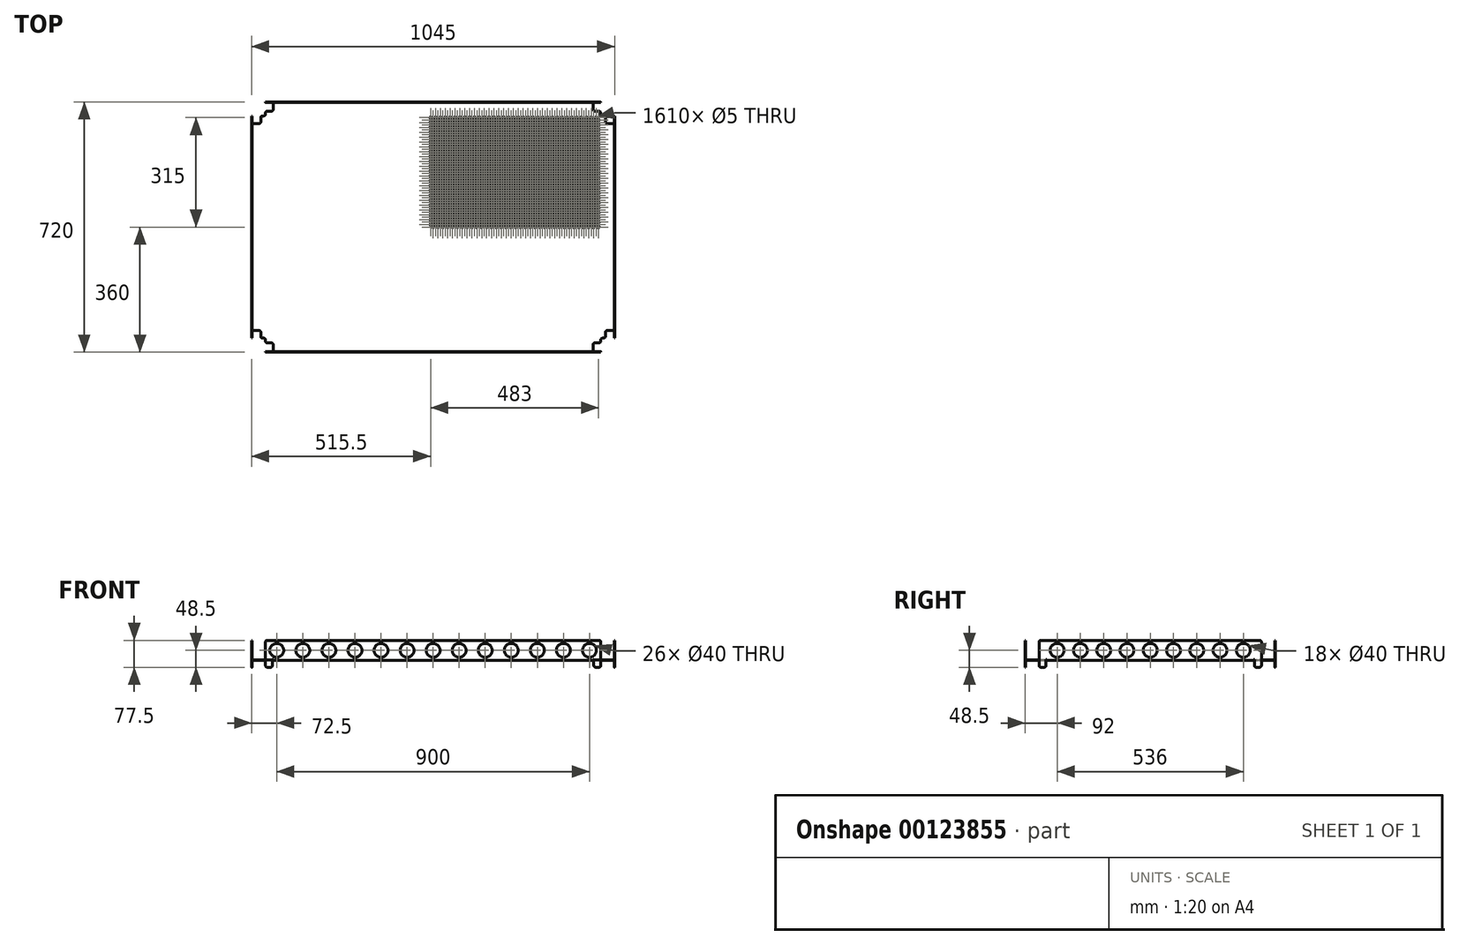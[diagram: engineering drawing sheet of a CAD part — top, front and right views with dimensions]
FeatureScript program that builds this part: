
annotation { "Feature Type Name" : "Feature", "Feature Type Description" : "" }
export const myFeature = defineFeature(function(context is Context, id is Id, definition is map)
    precondition{}
    {
        {
            var Q0;
            Q0=qCreatedBy(makeId("Front.planeOp"),FACE);
            var sketch = newSketch(context, id + "F0", { "sketchPlane" : qUnion([Q0])});
            skLineSegment(sketch, "E0", {"start": v(-520.5, 0) * mm, "end": v(520.5, 0) * mm});
            skLineSegment(sketch, "E1", {"start": v(-522.5, 2) * mm, "end": v(-522.5, 58) * mm});
            skLineSegment(sketch, "E2", {"start": v(0, 0) * mm, "end": v(0, 134.53) * mm, "construction": true});
            skLineSegment(sketch, "E3.MirrorCS", {"start": v(522.5, 2) * mm, "end": v(522.5, 58) * mm});
            skLineSegment(sketch, "E4.0", {"start": v(-521, 2.5) * mm, "end": v(-521, 58) * mm});
            skLineSegment(sketch, "E4.1", {"start": v(-520, 1.5) * mm, "end": v(520, 1.5) * mm});
            skLineSegment(sketch, "E4.2", {"start": v(521, 2.5) * mm, "end": v(521, 58) * mm});
            skLineSegment(sketch, "E5", {"start": v(-522.5, 58) * mm, "end": v(-521, 58) * mm});
            skLineSegment(sketch, "E6", {"start": v(521, 58) * mm, "end": v(522.5, 58) * mm});
            skPoint(sketch, "E7.visualSharp", {"position": v(521, 1.5) * mm});
            skArc(sketch, "E7.filletArc", {"start": v(520, 1.5) * mm, "mid": v(520.7, 1.8) * mm, "end": v(521, 2.5) * mm});
            skPoint(sketch, "E8.visualSharp", {"position": v(522.5, 0) * mm});
            skArc(sketch, "E8.filletArc", {"start": v(520.5, 0) * mm, "mid": v(521.91, 0.59) * mm, "end": v(522.5, 2) * mm});
            skPoint(sketch, "E9.visualSharp", {"position": v(-521, 1.5) * mm});
            skArc(sketch, "E9.filletArc", {"start": v(-521, 2.5) * mm, "mid": v(-520.7, 1.8) * mm, "end": v(-520, 1.5) * mm});
            skPoint(sketch, "E10.visualSharp", {"position": v(-522.5, 0) * mm});
            skArc(sketch, "E10.filletArc", {"start": v(-522.5, 2) * mm, "mid": v(-521.91, 0.59) * mm, "end": v(-520.5, 0) * mm});
            skSolve(sketch);
        }
        {
            var Q0;
            Q0 = qSketchRegion(id + "F0", true);
            extrude(context, id + "F1", {"entities" : qUnion([Q0]), "depth" : 360 * mm, "hasSecondDirection" : true, "secondDirectionOppositeDirection" : true, "secondDirectionDepth" : 360 * mm});
        }
        {
            var Q0;
            Q0=makeQuery(id+"F1.opExtrude","SWEPT_FACE",FACE,{"disambiguationData":[OSD([sQuery(id+"F0.wireOp",EDGE,"E4.2")])]});
            var sketch = newSketch(context, id + "F2", { "sketchPlane" : qUnion([Q0])});
            skLineSegment(sketch, "E11.bottom", {"start": v(-360, 58) * mm, "end": v(-358.5, 58) * mm});
            skLineSegment(sketch, "E11.top", {"start": v(-360, 0) * mm, "end": v(-358.5, 0) * mm});
            skLineSegment(sketch, "E11.left", {"start": v(-360, 58) * mm, "end": v(-360, 0) * mm});
            skLineSegment(sketch, "E11.right", {"start": v(-358.5, 58) * mm, "end": v(-358.5, 0) * mm});
            skLineSegment(sketch, "E12.bottom", {"start": v(360, 58) * mm, "end": v(358.5, 58) * mm});
            skLineSegment(sketch, "E12.top", {"start": v(360, 0) * mm, "end": v(358.5, 0) * mm});
            skLineSegment(sketch, "E12.left", {"start": v(360, 58) * mm, "end": v(360, 0) * mm});
            skLineSegment(sketch, "E12.right", {"start": v(358.5, 58) * mm, "end": v(358.5, 0) * mm});
            skSolve(sketch);
        }
        {
            var Q0;
            Q0 = qSketchRegion(id + "F2", true);
            var Q1;
            Q1=makeQuery(id+"F1.opExtrude","SWEPT_FACE",FACE,{"disambiguationData":[OSD([sQuery(id+"F0.wireOp",EDGE,"E4.0")])]});
            extrude(context, id + "F3", {"entities" : qUnion([Q0]), "operationType" : NewBodyOperationType.ADD, "endBound" : BoundingType.UP_TO_SURFACE, "endBoundEntityFace" : qUnion([Q1]), "depth" : 25 * mm});
        }
        {
            var Q0;
            Q0=makeQuery(id+"F1.opExtrude","CAP_EDGE",EDGE,{"disambiguationData":[OSD([sQuery(id+"F0.wireOp",EDGE,"E0")])],"isStart":true});
            var Q1;
            Q1=makeQuery(id+"F1.opExtrude","CAP_EDGE",EDGE,{"disambiguationData":[OSD([sQuery(id+"F0.wireOp",EDGE,"E0")])],"isStart":false});
            fillet(context, id + "F4", {"entities" : qUnion([Q0, Q1]), "radius" : 2 * mm, "tangentPropagation" : true, "allowEdgeOverflow" : false});
        }
        {
            var Q0;
            Q0=makeQuery(id+"F3.boolean.opBoolean","INTERSECT",EDGE,{"derivedFrom":[makeQuery(id+"F1.opExtrude","SWEPT_FACE",FACE,{"disambiguationData":[OSD([sQuery(id+"F0.wireOp",EDGE,"E4.1")])]}),makeQuery(id+"F3.opExtrude","SWEPT_FACE",FACE,{"disambiguationData":[OSD([sQuery(id+"F2.wireOp",EDGE,"E11.right")])]})]});
            var Q1;
            Q1=makeQuery(id+"F3.boolean.opBoolean","INTERSECT",EDGE,{"derivedFrom":[makeQuery(id+"F1.opExtrude","SWEPT_FACE",FACE,{"disambiguationData":[OSD([sQuery(id+"F0.wireOp",EDGE,"E4.1")])]}),makeQuery(id+"F3.opExtrude","SWEPT_FACE",FACE,{"disambiguationData":[OSD([sQuery(id+"F2.wireOp",EDGE,"E12.right")])]})]});
            fillet(context, id + "F5", {"entities" : qUnion([Q0, Q1]), "radius" : 1 * mm, "tangentPropagation" : true, "allowEdgeOverflow" : false});
        }
        {
            var Q0;
            Q0=makeQuery(id+"F3.boolean.opBoolean","MERGE",FACE,{"derivedFrom":[makeQuery(id+"F1.opExtrude","SWEPT_FACE",FACE,{"disambiguationData":[OSD([sQuery(id+"F0.wireOp",EDGE,"E0")])]}),makeQuery(id+"F3.opExtrude","SWEPT_FACE",FACE,{"disambiguationData":[OSD([sQuery(id+"F2.wireOp",EDGE,"E11.top")])]}),makeQuery(id+"F3.opExtrude","SWEPT_FACE",FACE,{"disambiguationData":[OSD([sQuery(id+"F2.wireOp",EDGE,"E12.top")])]})]});
            var sketch = newSketch(context, id + "F6", { "sketchPlane" : qUnion([Q0])});
            skLineSegment(sketch, "E13.bottom", {"start": v(487.5, -320) * mm, "end": v(522.5, -320) * mm});
            skLineSegment(sketch, "E13.top", {"start": v(482.5, -360) * mm, "end": v(522.5, -360) * mm});
            skLineSegment(sketch, "E13.left", {"start": v(482.5, -325) * mm, "end": v(482.5, -360) * mm});
            skLineSegment(sketch, "E13.right", {"start": v(522.5, -320) * mm, "end": v(522.5, -360) * mm});
            skPoint(sketch, "E14.visualSharp", {"position": v(482.5, -320) * mm});
            skArc(sketch, "E14.filletArc", {"start": v(487.5, -320) * mm, "mid": v(483.96, -321.46) * mm, "end": v(482.5, -325) * mm});
            skLineSegment(sketch, "E15", {"start": v(0, 0) * mm, "end": v(0, -371.02) * mm, "construction": true});
            skLineSegment(sketch, "E16", {"start": v(0, 0) * mm, "end": v(599.15, 0) * mm, "construction": true});
            skArc(sketch, "E17.MirrorCS", {"start": v(-487.5, -320) * mm, "mid": v(-483.96, -321.46) * mm, "end": v(-482.5, -325) * mm});
            skLineSegment(sketch, "E18.MirrorCS", {"start": v(-487.5, -320) * mm, "end": v(-522.5, -320) * mm});
            skLineSegment(sketch, "E19.MirrorCS", {"start": v(-482.5, -360) * mm, "end": v(-522.5, -360) * mm});
            skLineSegment(sketch, "E20.MirrorCS", {"start": v(-482.5, -325) * mm, "end": v(-482.5, -360) * mm});
            skLineSegment(sketch, "E21.MirrorCS", {"start": v(-522.5, -320) * mm, "end": v(-522.5, -360) * mm});
            skPoint(sketch, "E22.MirrorP", {"position": v(-482.5, -320) * mm});
            skArc(sketch, "E23.MirrorCS", {"start": v(-487.5, 320) * mm, "mid": v(-483.96, 321.46) * mm, "end": v(-482.5, 325) * mm});
            skArc(sketch, "E24.MirrorCS", {"start": v(487.5, 320) * mm, "mid": v(483.96, 321.46) * mm, "end": v(482.5, 325) * mm});
            skLineSegment(sketch, "E25.MirrorCS", {"start": v(-522.5, 320) * mm, "end": v(-522.5, 360) * mm});
            skLineSegment(sketch, "E26.MirrorCS", {"start": v(-482.5, 325) * mm, "end": v(-482.5, 360) * mm});
            skLineSegment(sketch, "E27.MirrorCS", {"start": v(-482.5, 360) * mm, "end": v(-522.5, 360) * mm});
            skLineSegment(sketch, "E28.MirrorCS", {"start": v(-487.5, 320) * mm, "end": v(-522.5, 320) * mm});
            skPoint(sketch, "E29.MirrorP", {"position": v(482.5, 320) * mm});
            skPoint(sketch, "E30.MirrorP", {"position": v(-482.5, 320) * mm});
            skLineSegment(sketch, "E31.MirrorCS", {"start": v(0, 0) * mm, "end": v(0, 371.02) * mm, "construction": true});
            skLineSegment(sketch, "E32.MirrorCS", {"start": v(522.5, 320) * mm, "end": v(522.5, 360) * mm});
            skLineSegment(sketch, "E33.MirrorCS", {"start": v(482.5, 325) * mm, "end": v(482.5, 360) * mm});
            skLineSegment(sketch, "E34.MirrorCS", {"start": v(482.5, 360) * mm, "end": v(522.5, 360) * mm});
            skLineSegment(sketch, "E35.MirrorCS", {"start": v(487.5, 320) * mm, "end": v(522.5, 320) * mm});
            skLineSegment(sketch, "E36", {"start": v(15.17, -320) * mm, "end": v(-45.75, -320) * mm, "construction": true});
            skLineSegment(sketch, "E37", {"start": v(482.5, -65.6) * mm, "end": v(482.5, 37.37) * mm, "construction": true});
            skCircle(sketch, "E38", {"center": v(0, 0) * mm, "radius": 2.5 * mm});
            skLineSegment(sketch, "E39.bottom", {"start": v(0, 0) * mm, "end": v(-7, 0) * mm, "construction": true});
            skLineSegment(sketch, "E39.top", {"start": v(0, -7) * mm, "end": v(-7, -7) * mm, "construction": true});
            skLineSegment(sketch, "E39.left", {"start": v(0, 0) * mm, "end": v(0, -7) * mm, "construction": true});
            skLineSegment(sketch, "E39.right", {"start": v(-7, 0) * mm, "end": v(-7, -7) * mm, "construction": true});
            skCircle(sketch, "E40", {"center": v(-7, -7) * mm, "radius": 2.5 * mm});
            skCircle(sketch, "E41.0.1.0", {"center": v(-7, -21) * mm, "radius": 2.5 * mm});
            skCircle(sketch, "E41.0.1.1", {"center": v(0, -14) * mm, "radius": 2.5 * mm});
            skCircle(sketch, "E41.0.2.0", {"center": v(-7, -35) * mm, "radius": 2.5 * mm});
            skCircle(sketch, "E41.0.2.1", {"center": v(0, -28) * mm, "radius": 2.5 * mm});
            skCircle(sketch, "E41.0.3.0", {"center": v(-7, -49) * mm, "radius": 2.5 * mm});
            skCircle(sketch, "E41.0.3.1", {"center": v(0, -42) * mm, "radius": 2.5 * mm});
            skCircle(sketch, "E41.0.4.0", {"center": v(-7, -63) * mm, "radius": 2.5 * mm});
            skCircle(sketch, "E41.0.4.1", {"center": v(0, -56) * mm, "radius": 2.5 * mm});
            skCircle(sketch, "E41.0.5.0", {"center": v(-7, -77) * mm, "radius": 2.5 * mm});
            skCircle(sketch, "E41.0.5.1", {"center": v(0, -70) * mm, "radius": 2.5 * mm});
            skCircle(sketch, "E41.0.6.0", {"center": v(-7, -91) * mm, "radius": 2.5 * mm});
            skCircle(sketch, "E41.0.6.1", {"center": v(0, -84) * mm, "radius": 2.5 * mm});
            skCircle(sketch, "E41.0.7.0", {"center": v(-7, -105) * mm, "radius": 2.5 * mm});
            skCircle(sketch, "E41.0.7.1", {"center": v(0, -98) * mm, "radius": 2.5 * mm});
            skCircle(sketch, "E41.0.8.0", {"center": v(-7, -119) * mm, "radius": 2.5 * mm});
            skCircle(sketch, "E41.0.8.1", {"center": v(0, -112) * mm, "radius": 2.5 * mm});
            skCircle(sketch, "E41.0.9.0", {"center": v(-7, -133) * mm, "radius": 2.5 * mm});
            skCircle(sketch, "E41.0.9.1", {"center": v(0, -126) * mm, "radius": 2.5 * mm});
            skCircle(sketch, "E41.0.10.0", {"center": v(-7, -147) * mm, "radius": 2.5 * mm});
            skCircle(sketch, "E41.0.10.1", {"center": v(0, -140) * mm, "radius": 2.5 * mm});
            skCircle(sketch, "E41.0.11.0", {"center": v(-7, -161) * mm, "radius": 2.5 * mm});
            skCircle(sketch, "E41.0.11.1", {"center": v(0, -154) * mm, "radius": 2.5 * mm});
            skCircle(sketch, "E41.0.12.0", {"center": v(-7, -175) * mm, "radius": 2.5 * mm});
            skCircle(sketch, "E41.0.12.1", {"center": v(0, -168) * mm, "radius": 2.5 * mm});
            skCircle(sketch, "E41.0.13.0", {"center": v(-7, -189) * mm, "radius": 2.5 * mm});
            skCircle(sketch, "E41.0.13.1", {"center": v(0, -182) * mm, "radius": 2.5 * mm});
            skCircle(sketch, "E41.0.14.0", {"center": v(-7, -203) * mm, "radius": 2.5 * mm});
            skCircle(sketch, "E41.0.14.1", {"center": v(0, -196) * mm, "radius": 2.5 * mm});
            skCircle(sketch, "E41.0.15.0", {"center": v(-7, -217) * mm, "radius": 2.5 * mm});
            skCircle(sketch, "E41.0.15.1", {"center": v(0, -210) * mm, "radius": 2.5 * mm});
            skCircle(sketch, "E41.0.16.0", {"center": v(-7, -231) * mm, "radius": 2.5 * mm});
            skCircle(sketch, "E41.0.16.1", {"center": v(0, -224) * mm, "radius": 2.5 * mm});
            skCircle(sketch, "E41.0.17.0", {"center": v(-7, -245) * mm, "radius": 2.5 * mm});
            skCircle(sketch, "E41.0.17.1", {"center": v(0, -238) * mm, "radius": 2.5 * mm});
            skCircle(sketch, "E41.0.18.0", {"center": v(-7, -259) * mm, "radius": 2.5 * mm});
            skCircle(sketch, "E41.0.18.1", {"center": v(0, -252) * mm, "radius": 2.5 * mm});
            skCircle(sketch, "E41.0.19.0", {"center": v(-7, -273) * mm, "radius": 2.5 * mm});
            skCircle(sketch, "E41.0.19.1", {"center": v(0, -266) * mm, "radius": 2.5 * mm});
            skCircle(sketch, "E41.1.0.0", {"center": v(7, -7) * mm, "radius": 2.5 * mm});
            skCircle(sketch, "E41.1.0.1", {"center": v(14, 0) * mm, "radius": 2.5 * mm});
            skCircle(sketch, "E41.1.1.0", {"center": v(7, -21) * mm, "radius": 2.5 * mm});
            skCircle(sketch, "E41.1.1.1", {"center": v(14, -14) * mm, "radius": 2.5 * mm});
            skCircle(sketch, "E41.1.2.0", {"center": v(7, -35) * mm, "radius": 2.5 * mm});
            skCircle(sketch, "E41.1.2.1", {"center": v(14, -28) * mm, "radius": 2.5 * mm});
            skCircle(sketch, "E41.1.3.0", {"center": v(7, -49) * mm, "radius": 2.5 * mm});
            skCircle(sketch, "E41.1.3.1", {"center": v(14, -42) * mm, "radius": 2.5 * mm});
            skCircle(sketch, "E41.1.4.0", {"center": v(7, -63) * mm, "radius": 2.5 * mm});
            skCircle(sketch, "E41.1.4.1", {"center": v(14, -56) * mm, "radius": 2.5 * mm});
            skCircle(sketch, "E41.1.5.0", {"center": v(7, -77) * mm, "radius": 2.5 * mm});
            skCircle(sketch, "E41.1.5.1", {"center": v(14, -70) * mm, "radius": 2.5 * mm});
            skCircle(sketch, "E41.1.6.0", {"center": v(7, -91) * mm, "radius": 2.5 * mm});
            skCircle(sketch, "E41.1.6.1", {"center": v(14, -84) * mm, "radius": 2.5 * mm});
            skCircle(sketch, "E41.1.7.0", {"center": v(7, -105) * mm, "radius": 2.5 * mm});
            skCircle(sketch, "E41.1.7.1", {"center": v(14, -98) * mm, "radius": 2.5 * mm});
            skCircle(sketch, "E41.1.8.0", {"center": v(7, -119) * mm, "radius": 2.5 * mm});
            skCircle(sketch, "E41.1.8.1", {"center": v(14, -112) * mm, "radius": 2.5 * mm});
            skCircle(sketch, "E41.1.9.0", {"center": v(7, -133) * mm, "radius": 2.5 * mm});
            skCircle(sketch, "E41.1.9.1", {"center": v(14, -126) * mm, "radius": 2.5 * mm});
            skCircle(sketch, "E41.1.10.0", {"center": v(7, -147) * mm, "radius": 2.5 * mm});
            skCircle(sketch, "E41.1.10.1", {"center": v(14, -140) * mm, "radius": 2.5 * mm});
            skCircle(sketch, "E41.1.11.0", {"center": v(7, -161) * mm, "radius": 2.5 * mm});
            skCircle(sketch, "E41.1.11.1", {"center": v(14, -154) * mm, "radius": 2.5 * mm});
            skCircle(sketch, "E41.1.12.0", {"center": v(7, -175) * mm, "radius": 2.5 * mm});
            skCircle(sketch, "E41.1.12.1", {"center": v(14, -168) * mm, "radius": 2.5 * mm});
            skCircle(sketch, "E41.1.13.0", {"center": v(7, -189) * mm, "radius": 2.5 * mm});
            skCircle(sketch, "E41.1.13.1", {"center": v(14, -182) * mm, "radius": 2.5 * mm});
            skCircle(sketch, "E41.1.14.0", {"center": v(7, -203) * mm, "radius": 2.5 * mm});
            skCircle(sketch, "E41.1.14.1", {"center": v(14, -196) * mm, "radius": 2.5 * mm});
            skCircle(sketch, "E41.1.15.0", {"center": v(7, -217) * mm, "radius": 2.5 * mm});
            skCircle(sketch, "E41.1.15.1", {"center": v(14, -210) * mm, "radius": 2.5 * mm});
            skCircle(sketch, "E41.1.16.0", {"center": v(7, -231) * mm, "radius": 2.5 * mm});
            skCircle(sketch, "E41.1.16.1", {"center": v(14, -224) * mm, "radius": 2.5 * mm});
            skCircle(sketch, "E41.1.17.0", {"center": v(7, -245) * mm, "radius": 2.5 * mm});
            skCircle(sketch, "E41.1.17.1", {"center": v(14, -238) * mm, "radius": 2.5 * mm});
            skCircle(sketch, "E41.1.18.0", {"center": v(7, -259) * mm, "radius": 2.5 * mm});
            skCircle(sketch, "E41.1.18.1", {"center": v(14, -252) * mm, "radius": 2.5 * mm});
            skCircle(sketch, "E41.1.19.0", {"center": v(7, -273) * mm, "radius": 2.5 * mm});
            skCircle(sketch, "E41.1.19.1", {"center": v(14, -266) * mm, "radius": 2.5 * mm});
            skCircle(sketch, "E41.2.0.0", {"center": v(21, -7) * mm, "radius": 2.5 * mm});
            skCircle(sketch, "E41.2.0.1", {"center": v(28, 0) * mm, "radius": 2.5 * mm});
            skCircle(sketch, "E41.2.1.0", {"center": v(21, -21) * mm, "radius": 2.5 * mm});
            skCircle(sketch, "E41.2.1.1", {"center": v(28, -14) * mm, "radius": 2.5 * mm});
            skCircle(sketch, "E41.2.2.0", {"center": v(21, -35) * mm, "radius": 2.5 * mm});
            skCircle(sketch, "E41.2.2.1", {"center": v(28, -28) * mm, "radius": 2.5 * mm});
            skCircle(sketch, "E41.2.3.0", {"center": v(21, -49) * mm, "radius": 2.5 * mm});
            skCircle(sketch, "E41.2.3.1", {"center": v(28, -42) * mm, "radius": 2.5 * mm});
            skCircle(sketch, "E41.2.4.0", {"center": v(21, -63) * mm, "radius": 2.5 * mm});
            skCircle(sketch, "E41.2.4.1", {"center": v(28, -56) * mm, "radius": 2.5 * mm});
            skCircle(sketch, "E41.2.5.0", {"center": v(21, -77) * mm, "radius": 2.5 * mm});
            skCircle(sketch, "E41.2.5.1", {"center": v(28, -70) * mm, "radius": 2.5 * mm});
            skCircle(sketch, "E41.2.6.0", {"center": v(21, -91) * mm, "radius": 2.5 * mm});
            skCircle(sketch, "E41.2.6.1", {"center": v(28, -84) * mm, "radius": 2.5 * mm});
            skCircle(sketch, "E41.2.7.0", {"center": v(21, -105) * mm, "radius": 2.5 * mm});
            skCircle(sketch, "E41.2.7.1", {"center": v(28, -98) * mm, "radius": 2.5 * mm});
            skCircle(sketch, "E41.2.8.0", {"center": v(21, -119) * mm, "radius": 2.5 * mm});
            skCircle(sketch, "E41.2.8.1", {"center": v(28, -112) * mm, "radius": 2.5 * mm});
            skCircle(sketch, "E41.2.9.0", {"center": v(21, -133) * mm, "radius": 2.5 * mm});
            skCircle(sketch, "E41.2.9.1", {"center": v(28, -126) * mm, "radius": 2.5 * mm});
            skCircle(sketch, "E41.2.10.0", {"center": v(21, -147) * mm, "radius": 2.5 * mm});
            skCircle(sketch, "E41.2.10.1", {"center": v(28, -140) * mm, "radius": 2.5 * mm});
            skCircle(sketch, "E41.2.11.0", {"center": v(21, -161) * mm, "radius": 2.5 * mm});
            skCircle(sketch, "E41.2.11.1", {"center": v(28, -154) * mm, "radius": 2.5 * mm});
            skCircle(sketch, "E41.2.12.0", {"center": v(21, -175) * mm, "radius": 2.5 * mm});
            skCircle(sketch, "E41.2.12.1", {"center": v(28, -168) * mm, "radius": 2.5 * mm});
            skCircle(sketch, "E41.2.13.0", {"center": v(21, -189) * mm, "radius": 2.5 * mm});
            skCircle(sketch, "E41.2.13.1", {"center": v(28, -182) * mm, "radius": 2.5 * mm});
            skCircle(sketch, "E41.2.14.0", {"center": v(21, -203) * mm, "radius": 2.5 * mm});
            skCircle(sketch, "E41.2.14.1", {"center": v(28, -196) * mm, "radius": 2.5 * mm});
            skCircle(sketch, "E41.2.15.0", {"center": v(21, -217) * mm, "radius": 2.5 * mm});
            skCircle(sketch, "E41.2.15.1", {"center": v(28, -210) * mm, "radius": 2.5 * mm});
            skCircle(sketch, "E41.2.16.0", {"center": v(21, -231) * mm, "radius": 2.5 * mm});
            skCircle(sketch, "E41.2.16.1", {"center": v(28, -224) * mm, "radius": 2.5 * mm});
            skCircle(sketch, "E41.2.17.0", {"center": v(21, -245) * mm, "radius": 2.5 * mm});
            skCircle(sketch, "E41.2.17.1", {"center": v(28, -238) * mm, "radius": 2.5 * mm});
            skCircle(sketch, "E41.2.18.0", {"center": v(21, -259) * mm, "radius": 2.5 * mm});
            skCircle(sketch, "E41.2.18.1", {"center": v(28, -252) * mm, "radius": 2.5 * mm});
            skCircle(sketch, "E41.2.19.0", {"center": v(21, -273) * mm, "radius": 2.5 * mm});
            skCircle(sketch, "E41.2.19.1", {"center": v(28, -266) * mm, "radius": 2.5 * mm});
            skCircle(sketch, "E41.3.0.0", {"center": v(35, -7) * mm, "radius": 2.5 * mm});
            skCircle(sketch, "E41.3.0.1", {"center": v(42, 0) * mm, "radius": 2.5 * mm});
            skCircle(sketch, "E41.3.1.0", {"center": v(35, -21) * mm, "radius": 2.5 * mm});
            skCircle(sketch, "E41.3.1.1", {"center": v(42, -14) * mm, "radius": 2.5 * mm});
            skCircle(sketch, "E41.3.2.0", {"center": v(35, -35) * mm, "radius": 2.5 * mm});
            skCircle(sketch, "E41.3.2.1", {"center": v(42, -28) * mm, "radius": 2.5 * mm});
            skCircle(sketch, "E41.3.3.0", {"center": v(35, -49) * mm, "radius": 2.5 * mm});
            skCircle(sketch, "E41.3.3.1", {"center": v(42, -42) * mm, "radius": 2.5 * mm});
            skCircle(sketch, "E41.3.4.0", {"center": v(35, -63) * mm, "radius": 2.5 * mm});
            skCircle(sketch, "E41.3.4.1", {"center": v(42, -56) * mm, "radius": 2.5 * mm});
            skCircle(sketch, "E41.3.5.0", {"center": v(35, -77) * mm, "radius": 2.5 * mm});
            skCircle(sketch, "E41.3.5.1", {"center": v(42, -70) * mm, "radius": 2.5 * mm});
            skCircle(sketch, "E41.3.6.0", {"center": v(35, -91) * mm, "radius": 2.5 * mm});
            skCircle(sketch, "E41.3.6.1", {"center": v(42, -84) * mm, "radius": 2.5 * mm});
            skCircle(sketch, "E41.3.7.0", {"center": v(35, -105) * mm, "radius": 2.5 * mm});
            skCircle(sketch, "E41.3.7.1", {"center": v(42, -98) * mm, "radius": 2.5 * mm});
            skCircle(sketch, "E41.3.8.0", {"center": v(35, -119) * mm, "radius": 2.5 * mm});
            skCircle(sketch, "E41.3.8.1", {"center": v(42, -112) * mm, "radius": 2.5 * mm});
            skCircle(sketch, "E41.3.9.0", {"center": v(35, -133) * mm, "radius": 2.5 * mm});
            skCircle(sketch, "E41.3.9.1", {"center": v(42, -126) * mm, "radius": 2.5 * mm});
            skCircle(sketch, "E41.3.10.0", {"center": v(35, -147) * mm, "radius": 2.5 * mm});
            skCircle(sketch, "E41.3.10.1", {"center": v(42, -140) * mm, "radius": 2.5 * mm});
            skCircle(sketch, "E41.3.11.0", {"center": v(35, -161) * mm, "radius": 2.5 * mm});
            skCircle(sketch, "E41.3.11.1", {"center": v(42, -154) * mm, "radius": 2.5 * mm});
            skCircle(sketch, "E41.3.12.0", {"center": v(35, -175) * mm, "radius": 2.5 * mm});
            skCircle(sketch, "E41.3.12.1", {"center": v(42, -168) * mm, "radius": 2.5 * mm});
            skCircle(sketch, "E41.3.13.0", {"center": v(35, -189) * mm, "radius": 2.5 * mm});
            skCircle(sketch, "E41.3.13.1", {"center": v(42, -182) * mm, "radius": 2.5 * mm});
            skCircle(sketch, "E41.3.14.0", {"center": v(35, -203) * mm, "radius": 2.5 * mm});
            skCircle(sketch, "E41.3.14.1", {"center": v(42, -196) * mm, "radius": 2.5 * mm});
            skCircle(sketch, "E41.3.15.0", {"center": v(35, -217) * mm, "radius": 2.5 * mm});
            skCircle(sketch, "E41.3.15.1", {"center": v(42, -210) * mm, "radius": 2.5 * mm});
            skCircle(sketch, "E41.3.16.0", {"center": v(35, -231) * mm, "radius": 2.5 * mm});
            skCircle(sketch, "E41.3.16.1", {"center": v(42, -224) * mm, "radius": 2.5 * mm});
            skCircle(sketch, "E41.3.17.0", {"center": v(35, -245) * mm, "radius": 2.5 * mm});
            skCircle(sketch, "E41.3.17.1", {"center": v(42, -238) * mm, "radius": 2.5 * mm});
            skCircle(sketch, "E41.3.18.0", {"center": v(35, -259) * mm, "radius": 2.5 * mm});
            skCircle(sketch, "E41.3.18.1", {"center": v(42, -252) * mm, "radius": 2.5 * mm});
            skCircle(sketch, "E41.3.19.0", {"center": v(35, -273) * mm, "radius": 2.5 * mm});
            skCircle(sketch, "E41.3.19.1", {"center": v(42, -266) * mm, "radius": 2.5 * mm});
            skCircle(sketch, "E41.4.0.0", {"center": v(49, -7) * mm, "radius": 2.5 * mm});
            skCircle(sketch, "E41.4.0.1", {"center": v(56, 0) * mm, "radius": 2.5 * mm});
            skCircle(sketch, "E41.4.1.0", {"center": v(49, -21) * mm, "radius": 2.5 * mm});
            skCircle(sketch, "E41.4.1.1", {"center": v(56, -14) * mm, "radius": 2.5 * mm});
            skCircle(sketch, "E41.4.2.0", {"center": v(49, -35) * mm, "radius": 2.5 * mm});
            skCircle(sketch, "E41.4.2.1", {"center": v(56, -28) * mm, "radius": 2.5 * mm});
            skCircle(sketch, "E41.4.3.0", {"center": v(49, -49) * mm, "radius": 2.5 * mm});
            skCircle(sketch, "E41.4.3.1", {"center": v(56, -42) * mm, "radius": 2.5 * mm});
            skCircle(sketch, "E41.4.4.0", {"center": v(49, -63) * mm, "radius": 2.5 * mm});
            skCircle(sketch, "E41.4.4.1", {"center": v(56, -56) * mm, "radius": 2.5 * mm});
            skCircle(sketch, "E41.4.5.0", {"center": v(49, -77) * mm, "radius": 2.5 * mm});
            skCircle(sketch, "E41.4.5.1", {"center": v(56, -70) * mm, "radius": 2.5 * mm});
            skCircle(sketch, "E41.4.6.0", {"center": v(49, -91) * mm, "radius": 2.5 * mm});
            skCircle(sketch, "E41.4.6.1", {"center": v(56, -84) * mm, "radius": 2.5 * mm});
            skCircle(sketch, "E41.4.7.0", {"center": v(49, -105) * mm, "radius": 2.5 * mm});
            skCircle(sketch, "E41.4.7.1", {"center": v(56, -98) * mm, "radius": 2.5 * mm});
            skCircle(sketch, "E41.4.8.0", {"center": v(49, -119) * mm, "radius": 2.5 * mm});
            skCircle(sketch, "E41.4.8.1", {"center": v(56, -112) * mm, "radius": 2.5 * mm});
            skCircle(sketch, "E41.4.9.0", {"center": v(49, -133) * mm, "radius": 2.5 * mm});
            skCircle(sketch, "E41.4.9.1", {"center": v(56, -126) * mm, "radius": 2.5 * mm});
            skCircle(sketch, "E41.4.10.0", {"center": v(49, -147) * mm, "radius": 2.5 * mm});
            skCircle(sketch, "E41.4.10.1", {"center": v(56, -140) * mm, "radius": 2.5 * mm});
            skCircle(sketch, "E41.4.11.0", {"center": v(49, -161) * mm, "radius": 2.5 * mm});
            skCircle(sketch, "E41.4.11.1", {"center": v(56, -154) * mm, "radius": 2.5 * mm});
            skCircle(sketch, "E41.4.12.0", {"center": v(49, -175) * mm, "radius": 2.5 * mm});
            skCircle(sketch, "E41.4.12.1", {"center": v(56, -168) * mm, "radius": 2.5 * mm});
            skCircle(sketch, "E41.4.13.0", {"center": v(49, -189) * mm, "radius": 2.5 * mm});
            skCircle(sketch, "E41.4.13.1", {"center": v(56, -182) * mm, "radius": 2.5 * mm});
            skCircle(sketch, "E41.4.14.0", {"center": v(49, -203) * mm, "radius": 2.5 * mm});
            skCircle(sketch, "E41.4.14.1", {"center": v(56, -196) * mm, "radius": 2.5 * mm});
            skCircle(sketch, "E41.4.15.0", {"center": v(49, -217) * mm, "radius": 2.5 * mm});
            skCircle(sketch, "E41.4.15.1", {"center": v(56, -210) * mm, "radius": 2.5 * mm});
            skCircle(sketch, "E41.4.16.0", {"center": v(49, -231) * mm, "radius": 2.5 * mm});
            skCircle(sketch, "E41.4.16.1", {"center": v(56, -224) * mm, "radius": 2.5 * mm});
            skCircle(sketch, "E41.4.17.0", {"center": v(49, -245) * mm, "radius": 2.5 * mm});
            skCircle(sketch, "E41.4.17.1", {"center": v(56, -238) * mm, "radius": 2.5 * mm});
            skCircle(sketch, "E41.4.18.0", {"center": v(49, -259) * mm, "radius": 2.5 * mm});
            skCircle(sketch, "E41.4.18.1", {"center": v(56, -252) * mm, "radius": 2.5 * mm});
            skCircle(sketch, "E41.4.19.0", {"center": v(49, -273) * mm, "radius": 2.5 * mm});
            skCircle(sketch, "E41.4.19.1", {"center": v(56, -266) * mm, "radius": 2.5 * mm});
            skCircle(sketch, "E41.5.0.0", {"center": v(63, -7) * mm, "radius": 2.5 * mm});
            skCircle(sketch, "E41.5.0.1", {"center": v(70, 0) * mm, "radius": 2.5 * mm});
            skCircle(sketch, "E41.5.1.0", {"center": v(63, -21) * mm, "radius": 2.5 * mm});
            skCircle(sketch, "E41.5.1.1", {"center": v(70, -14) * mm, "radius": 2.5 * mm});
            skCircle(sketch, "E41.5.2.0", {"center": v(63, -35) * mm, "radius": 2.5 * mm});
            skCircle(sketch, "E41.5.2.1", {"center": v(70, -28) * mm, "radius": 2.5 * mm});
            skCircle(sketch, "E41.5.3.0", {"center": v(63, -49) * mm, "radius": 2.5 * mm});
            skCircle(sketch, "E41.5.3.1", {"center": v(70, -42) * mm, "radius": 2.5 * mm});
            skCircle(sketch, "E41.5.4.0", {"center": v(63, -63) * mm, "radius": 2.5 * mm});
            skCircle(sketch, "E41.5.4.1", {"center": v(70, -56) * mm, "radius": 2.5 * mm});
            skCircle(sketch, "E41.5.5.0", {"center": v(63, -77) * mm, "radius": 2.5 * mm});
            skCircle(sketch, "E41.5.5.1", {"center": v(70, -70) * mm, "radius": 2.5 * mm});
            skCircle(sketch, "E41.5.6.0", {"center": v(63, -91) * mm, "radius": 2.5 * mm});
            skCircle(sketch, "E41.5.6.1", {"center": v(70, -84) * mm, "radius": 2.5 * mm});
            skCircle(sketch, "E41.5.7.0", {"center": v(63, -105) * mm, "radius": 2.5 * mm});
            skCircle(sketch, "E41.5.7.1", {"center": v(70, -98) * mm, "radius": 2.5 * mm});
            skCircle(sketch, "E41.5.8.0", {"center": v(63, -119) * mm, "radius": 2.5 * mm});
            skCircle(sketch, "E41.5.8.1", {"center": v(70, -112) * mm, "radius": 2.5 * mm});
            skCircle(sketch, "E41.5.9.0", {"center": v(63, -133) * mm, "radius": 2.5 * mm});
            skCircle(sketch, "E41.5.9.1", {"center": v(70, -126) * mm, "radius": 2.5 * mm});
            skCircle(sketch, "E41.5.10.0", {"center": v(63, -147) * mm, "radius": 2.5 * mm});
            skCircle(sketch, "E41.5.10.1", {"center": v(70, -140) * mm, "radius": 2.5 * mm});
            skCircle(sketch, "E41.5.11.0", {"center": v(63, -161) * mm, "radius": 2.5 * mm});
            skCircle(sketch, "E41.5.11.1", {"center": v(70, -154) * mm, "radius": 2.5 * mm});
            skCircle(sketch, "E41.5.12.0", {"center": v(63, -175) * mm, "radius": 2.5 * mm});
            skCircle(sketch, "E41.5.12.1", {"center": v(70, -168) * mm, "radius": 2.5 * mm});
            skCircle(sketch, "E41.5.13.0", {"center": v(63, -189) * mm, "radius": 2.5 * mm});
            skCircle(sketch, "E41.5.13.1", {"center": v(70, -182) * mm, "radius": 2.5 * mm});
            skCircle(sketch, "E41.5.14.0", {"center": v(63, -203) * mm, "radius": 2.5 * mm});
            skCircle(sketch, "E41.5.14.1", {"center": v(70, -196) * mm, "radius": 2.5 * mm});
            skCircle(sketch, "E41.5.15.0", {"center": v(63, -217) * mm, "radius": 2.5 * mm});
            skCircle(sketch, "E41.5.15.1", {"center": v(70, -210) * mm, "radius": 2.5 * mm});
            skCircle(sketch, "E41.5.16.0", {"center": v(63, -231) * mm, "radius": 2.5 * mm});
            skCircle(sketch, "E41.5.16.1", {"center": v(70, -224) * mm, "radius": 2.5 * mm});
            skCircle(sketch, "E41.5.17.0", {"center": v(63, -245) * mm, "radius": 2.5 * mm});
            skCircle(sketch, "E41.5.17.1", {"center": v(70, -238) * mm, "radius": 2.5 * mm});
            skCircle(sketch, "E41.5.18.0", {"center": v(63, -259) * mm, "radius": 2.5 * mm});
            skCircle(sketch, "E41.5.18.1", {"center": v(70, -252) * mm, "radius": 2.5 * mm});
            skCircle(sketch, "E41.5.19.0", {"center": v(63, -273) * mm, "radius": 2.5 * mm});
            skCircle(sketch, "E41.5.19.1", {"center": v(70, -266) * mm, "radius": 2.5 * mm});
            skCircle(sketch, "E41.6.0.0", {"center": v(77, -7) * mm, "radius": 2.5 * mm});
            skCircle(sketch, "E41.6.0.1", {"center": v(84, 0) * mm, "radius": 2.5 * mm});
            skCircle(sketch, "E41.6.1.0", {"center": v(77, -21) * mm, "radius": 2.5 * mm});
            skCircle(sketch, "E41.6.1.1", {"center": v(84, -14) * mm, "radius": 2.5 * mm});
            skCircle(sketch, "E41.6.2.0", {"center": v(77, -35) * mm, "radius": 2.5 * mm});
            skCircle(sketch, "E41.6.2.1", {"center": v(84, -28) * mm, "radius": 2.5 * mm});
            skCircle(sketch, "E41.6.3.0", {"center": v(77, -49) * mm, "radius": 2.5 * mm});
            skCircle(sketch, "E41.6.3.1", {"center": v(84, -42) * mm, "radius": 2.5 * mm});
            skCircle(sketch, "E41.6.4.0", {"center": v(77, -63) * mm, "radius": 2.5 * mm});
            skCircle(sketch, "E41.6.4.1", {"center": v(84, -56) * mm, "radius": 2.5 * mm});
            skCircle(sketch, "E41.6.5.0", {"center": v(77, -77) * mm, "radius": 2.5 * mm});
            skCircle(sketch, "E41.6.5.1", {"center": v(84, -70) * mm, "radius": 2.5 * mm});
            skCircle(sketch, "E41.6.6.0", {"center": v(77, -91) * mm, "radius": 2.5 * mm});
            skCircle(sketch, "E41.6.6.1", {"center": v(84, -84) * mm, "radius": 2.5 * mm});
            skCircle(sketch, "E41.6.7.0", {"center": v(77, -105) * mm, "radius": 2.5 * mm});
            skCircle(sketch, "E41.6.7.1", {"center": v(84, -98) * mm, "radius": 2.5 * mm});
            skCircle(sketch, "E41.6.8.0", {"center": v(77, -119) * mm, "radius": 2.5 * mm});
            skCircle(sketch, "E41.6.8.1", {"center": v(84, -112) * mm, "radius": 2.5 * mm});
            skCircle(sketch, "E41.6.9.0", {"center": v(77, -133) * mm, "radius": 2.5 * mm});
            skCircle(sketch, "E41.6.9.1", {"center": v(84, -126) * mm, "radius": 2.5 * mm});
            skCircle(sketch, "E41.6.10.0", {"center": v(77, -147) * mm, "radius": 2.5 * mm});
            skCircle(sketch, "E41.6.10.1", {"center": v(84, -140) * mm, "radius": 2.5 * mm});
            skCircle(sketch, "E41.6.11.0", {"center": v(77, -161) * mm, "radius": 2.5 * mm});
            skCircle(sketch, "E41.6.11.1", {"center": v(84, -154) * mm, "radius": 2.5 * mm});
            skCircle(sketch, "E41.6.12.0", {"center": v(77, -175) * mm, "radius": 2.5 * mm});
            skCircle(sketch, "E41.6.12.1", {"center": v(84, -168) * mm, "radius": 2.5 * mm});
            skCircle(sketch, "E41.6.13.0", {"center": v(77, -189) * mm, "radius": 2.5 * mm});
            skCircle(sketch, "E41.6.13.1", {"center": v(84, -182) * mm, "radius": 2.5 * mm});
            skCircle(sketch, "E41.6.14.0", {"center": v(77, -203) * mm, "radius": 2.5 * mm});
            skCircle(sketch, "E41.6.14.1", {"center": v(84, -196) * mm, "radius": 2.5 * mm});
            skCircle(sketch, "E41.6.15.0", {"center": v(77, -217) * mm, "radius": 2.5 * mm});
            skCircle(sketch, "E41.6.15.1", {"center": v(84, -210) * mm, "radius": 2.5 * mm});
            skCircle(sketch, "E41.6.16.0", {"center": v(77, -231) * mm, "radius": 2.5 * mm});
            skCircle(sketch, "E41.6.16.1", {"center": v(84, -224) * mm, "radius": 2.5 * mm});
            skCircle(sketch, "E41.6.17.0", {"center": v(77, -245) * mm, "radius": 2.5 * mm});
            skCircle(sketch, "E41.6.17.1", {"center": v(84, -238) * mm, "radius": 2.5 * mm});
            skCircle(sketch, "E41.6.18.0", {"center": v(77, -259) * mm, "radius": 2.5 * mm});
            skCircle(sketch, "E41.6.18.1", {"center": v(84, -252) * mm, "radius": 2.5 * mm});
            skCircle(sketch, "E41.6.19.0", {"center": v(77, -273) * mm, "radius": 2.5 * mm});
            skCircle(sketch, "E41.6.19.1", {"center": v(84, -266) * mm, "radius": 2.5 * mm});
            skCircle(sketch, "E41.7.0.0", {"center": v(91, -7) * mm, "radius": 2.5 * mm});
            skCircle(sketch, "E41.7.0.1", {"center": v(98, 0) * mm, "radius": 2.5 * mm});
            skCircle(sketch, "E41.7.1.0", {"center": v(91, -21) * mm, "radius": 2.5 * mm});
            skCircle(sketch, "E41.7.1.1", {"center": v(98, -14) * mm, "radius": 2.5 * mm});
            skCircle(sketch, "E41.7.2.0", {"center": v(91, -35) * mm, "radius": 2.5 * mm});
            skCircle(sketch, "E41.7.2.1", {"center": v(98, -28) * mm, "radius": 2.5 * mm});
            skCircle(sketch, "E41.7.3.0", {"center": v(91, -49) * mm, "radius": 2.5 * mm});
            skCircle(sketch, "E41.7.3.1", {"center": v(98, -42) * mm, "radius": 2.5 * mm});
            skCircle(sketch, "E41.7.4.0", {"center": v(91, -63) * mm, "radius": 2.5 * mm});
            skCircle(sketch, "E41.7.4.1", {"center": v(98, -56) * mm, "radius": 2.5 * mm});
            skCircle(sketch, "E41.7.5.0", {"center": v(91, -77) * mm, "radius": 2.5 * mm});
            skCircle(sketch, "E41.7.5.1", {"center": v(98, -70) * mm, "radius": 2.5 * mm});
            skCircle(sketch, "E41.7.6.0", {"center": v(91, -91) * mm, "radius": 2.5 * mm});
            skCircle(sketch, "E41.7.6.1", {"center": v(98, -84) * mm, "radius": 2.5 * mm});
            skCircle(sketch, "E41.7.7.0", {"center": v(91, -105) * mm, "radius": 2.5 * mm});
            skCircle(sketch, "E41.7.7.1", {"center": v(98, -98) * mm, "radius": 2.5 * mm});
            skCircle(sketch, "E41.7.8.0", {"center": v(91, -119) * mm, "radius": 2.5 * mm});
            skCircle(sketch, "E41.7.8.1", {"center": v(98, -112) * mm, "radius": 2.5 * mm});
            skCircle(sketch, "E41.7.9.0", {"center": v(91, -133) * mm, "radius": 2.5 * mm});
            skCircle(sketch, "E41.7.9.1", {"center": v(98, -126) * mm, "radius": 2.5 * mm});
            skCircle(sketch, "E41.7.10.0", {"center": v(91, -147) * mm, "radius": 2.5 * mm});
            skCircle(sketch, "E41.7.10.1", {"center": v(98, -140) * mm, "radius": 2.5 * mm});
            skCircle(sketch, "E41.7.11.0", {"center": v(91, -161) * mm, "radius": 2.5 * mm});
            skCircle(sketch, "E41.7.11.1", {"center": v(98, -154) * mm, "radius": 2.5 * mm});
            skCircle(sketch, "E41.7.12.0", {"center": v(91, -175) * mm, "radius": 2.5 * mm});
            skCircle(sketch, "E41.7.12.1", {"center": v(98, -168) * mm, "radius": 2.5 * mm});
            skCircle(sketch, "E41.7.13.0", {"center": v(91, -189) * mm, "radius": 2.5 * mm});
            skCircle(sketch, "E41.7.13.1", {"center": v(98, -182) * mm, "radius": 2.5 * mm});
            skCircle(sketch, "E41.7.14.0", {"center": v(91, -203) * mm, "radius": 2.5 * mm});
            skCircle(sketch, "E41.7.14.1", {"center": v(98, -196) * mm, "radius": 2.5 * mm});
            skCircle(sketch, "E41.7.15.0", {"center": v(91, -217) * mm, "radius": 2.5 * mm});
            skCircle(sketch, "E41.7.15.1", {"center": v(98, -210) * mm, "radius": 2.5 * mm});
            skCircle(sketch, "E41.7.16.0", {"center": v(91, -231) * mm, "radius": 2.5 * mm});
            skCircle(sketch, "E41.7.16.1", {"center": v(98, -224) * mm, "radius": 2.5 * mm});
            skCircle(sketch, "E41.7.17.0", {"center": v(91, -245) * mm, "radius": 2.5 * mm});
            skCircle(sketch, "E41.7.17.1", {"center": v(98, -238) * mm, "radius": 2.5 * mm});
            skCircle(sketch, "E41.7.18.0", {"center": v(91, -259) * mm, "radius": 2.5 * mm});
            skCircle(sketch, "E41.7.18.1", {"center": v(98, -252) * mm, "radius": 2.5 * mm});
            skCircle(sketch, "E41.7.19.0", {"center": v(91, -273) * mm, "radius": 2.5 * mm});
            skCircle(sketch, "E41.7.19.1", {"center": v(98, -266) * mm, "radius": 2.5 * mm});
            skCircle(sketch, "E41.8.0.0", {"center": v(105, -7) * mm, "radius": 2.5 * mm});
            skCircle(sketch, "E41.8.0.1", {"center": v(112, 0) * mm, "radius": 2.5 * mm});
            skCircle(sketch, "E41.8.1.0", {"center": v(105, -21) * mm, "radius": 2.5 * mm});
            skCircle(sketch, "E41.8.1.1", {"center": v(112, -14) * mm, "radius": 2.5 * mm});
            skCircle(sketch, "E41.8.2.0", {"center": v(105, -35) * mm, "radius": 2.5 * mm});
            skCircle(sketch, "E41.8.2.1", {"center": v(112, -28) * mm, "radius": 2.5 * mm});
            skCircle(sketch, "E41.8.3.0", {"center": v(105, -49) * mm, "radius": 2.5 * mm});
            skCircle(sketch, "E41.8.3.1", {"center": v(112, -42) * mm, "radius": 2.5 * mm});
            skCircle(sketch, "E41.8.4.0", {"center": v(105, -63) * mm, "radius": 2.5 * mm});
            skCircle(sketch, "E41.8.4.1", {"center": v(112, -56) * mm, "radius": 2.5 * mm});
            skCircle(sketch, "E41.8.5.0", {"center": v(105, -77) * mm, "radius": 2.5 * mm});
            skCircle(sketch, "E41.8.5.1", {"center": v(112, -70) * mm, "radius": 2.5 * mm});
            skCircle(sketch, "E41.8.6.0", {"center": v(105, -91) * mm, "radius": 2.5 * mm});
            skCircle(sketch, "E41.8.6.1", {"center": v(112, -84) * mm, "radius": 2.5 * mm});
            skCircle(sketch, "E41.8.7.0", {"center": v(105, -105) * mm, "radius": 2.5 * mm});
            skCircle(sketch, "E41.8.7.1", {"center": v(112, -98) * mm, "radius": 2.5 * mm});
            skCircle(sketch, "E41.8.8.0", {"center": v(105, -119) * mm, "radius": 2.5 * mm});
            skCircle(sketch, "E41.8.8.1", {"center": v(112, -112) * mm, "radius": 2.5 * mm});
            skCircle(sketch, "E41.8.9.0", {"center": v(105, -133) * mm, "radius": 2.5 * mm});
            skCircle(sketch, "E41.8.9.1", {"center": v(112, -126) * mm, "radius": 2.5 * mm});
            skCircle(sketch, "E41.8.10.0", {"center": v(105, -147) * mm, "radius": 2.5 * mm});
            skCircle(sketch, "E41.8.10.1", {"center": v(112, -140) * mm, "radius": 2.5 * mm});
            skCircle(sketch, "E41.8.11.0", {"center": v(105, -161) * mm, "radius": 2.5 * mm});
            skCircle(sketch, "E41.8.11.1", {"center": v(112, -154) * mm, "radius": 2.5 * mm});
            skCircle(sketch, "E41.8.12.0", {"center": v(105, -175) * mm, "radius": 2.5 * mm});
            skCircle(sketch, "E41.8.12.1", {"center": v(112, -168) * mm, "radius": 2.5 * mm});
            skCircle(sketch, "E41.8.13.0", {"center": v(105, -189) * mm, "radius": 2.5 * mm});
            skCircle(sketch, "E41.8.13.1", {"center": v(112, -182) * mm, "radius": 2.5 * mm});
            skCircle(sketch, "E41.8.14.0", {"center": v(105, -203) * mm, "radius": 2.5 * mm});
            skCircle(sketch, "E41.8.14.1", {"center": v(112, -196) * mm, "radius": 2.5 * mm});
            skCircle(sketch, "E41.8.15.0", {"center": v(105, -217) * mm, "radius": 2.5 * mm});
            skCircle(sketch, "E41.8.15.1", {"center": v(112, -210) * mm, "radius": 2.5 * mm});
            skCircle(sketch, "E41.8.16.0", {"center": v(105, -231) * mm, "radius": 2.5 * mm});
            skCircle(sketch, "E41.8.16.1", {"center": v(112, -224) * mm, "radius": 2.5 * mm});
            skCircle(sketch, "E41.8.17.0", {"center": v(105, -245) * mm, "radius": 2.5 * mm});
            skCircle(sketch, "E41.8.17.1", {"center": v(112, -238) * mm, "radius": 2.5 * mm});
            skCircle(sketch, "E41.8.18.0", {"center": v(105, -259) * mm, "radius": 2.5 * mm});
            skCircle(sketch, "E41.8.18.1", {"center": v(112, -252) * mm, "radius": 2.5 * mm});
            skCircle(sketch, "E41.8.19.0", {"center": v(105, -273) * mm, "radius": 2.5 * mm});
            skCircle(sketch, "E41.8.19.1", {"center": v(112, -266) * mm, "radius": 2.5 * mm});
            skCircle(sketch, "E41.9.0.0", {"center": v(119, -7) * mm, "radius": 2.5 * mm});
            skCircle(sketch, "E41.9.0.1", {"center": v(126, 0) * mm, "radius": 2.5 * mm});
            skCircle(sketch, "E41.9.1.0", {"center": v(119, -21) * mm, "radius": 2.5 * mm});
            skCircle(sketch, "E41.9.1.1", {"center": v(126, -14) * mm, "radius": 2.5 * mm});
            skCircle(sketch, "E41.9.2.0", {"center": v(119, -35) * mm, "radius": 2.5 * mm});
            skCircle(sketch, "E41.9.2.1", {"center": v(126, -28) * mm, "radius": 2.5 * mm});
            skCircle(sketch, "E41.9.3.0", {"center": v(119, -49) * mm, "radius": 2.5 * mm});
            skCircle(sketch, "E41.9.3.1", {"center": v(126, -42) * mm, "radius": 2.5 * mm});
            skCircle(sketch, "E41.9.4.0", {"center": v(119, -63) * mm, "radius": 2.5 * mm});
            skCircle(sketch, "E41.9.4.1", {"center": v(126, -56) * mm, "radius": 2.5 * mm});
            skCircle(sketch, "E41.9.5.0", {"center": v(119, -77) * mm, "radius": 2.5 * mm});
            skCircle(sketch, "E41.9.5.1", {"center": v(126, -70) * mm, "radius": 2.5 * mm});
            skCircle(sketch, "E41.9.6.0", {"center": v(119, -91) * mm, "radius": 2.5 * mm});
            skCircle(sketch, "E41.9.6.1", {"center": v(126, -84) * mm, "radius": 2.5 * mm});
            skCircle(sketch, "E41.9.7.0", {"center": v(119, -105) * mm, "radius": 2.5 * mm});
            skCircle(sketch, "E41.9.7.1", {"center": v(126, -98) * mm, "radius": 2.5 * mm});
            skCircle(sketch, "E41.9.8.0", {"center": v(119, -119) * mm, "radius": 2.5 * mm});
            skCircle(sketch, "E41.9.8.1", {"center": v(126, -112) * mm, "radius": 2.5 * mm});
            skCircle(sketch, "E41.9.9.0", {"center": v(119, -133) * mm, "radius": 2.5 * mm});
            skCircle(sketch, "E41.9.9.1", {"center": v(126, -126) * mm, "radius": 2.5 * mm});
            skCircle(sketch, "E41.9.10.0", {"center": v(119, -147) * mm, "radius": 2.5 * mm});
            skCircle(sketch, "E41.9.10.1", {"center": v(126, -140) * mm, "radius": 2.5 * mm});
            skCircle(sketch, "E41.9.11.0", {"center": v(119, -161) * mm, "radius": 2.5 * mm});
            skCircle(sketch, "E41.9.11.1", {"center": v(126, -154) * mm, "radius": 2.5 * mm});
            skCircle(sketch, "E41.9.12.0", {"center": v(119, -175) * mm, "radius": 2.5 * mm});
            skCircle(sketch, "E41.9.12.1", {"center": v(126, -168) * mm, "radius": 2.5 * mm});
            skCircle(sketch, "E41.9.13.0", {"center": v(119, -189) * mm, "radius": 2.5 * mm});
            skCircle(sketch, "E41.9.13.1", {"center": v(126, -182) * mm, "radius": 2.5 * mm});
            skCircle(sketch, "E41.9.14.0", {"center": v(119, -203) * mm, "radius": 2.5 * mm});
            skCircle(sketch, "E41.9.14.1", {"center": v(126, -196) * mm, "radius": 2.5 * mm});
            skCircle(sketch, "E41.9.15.0", {"center": v(119, -217) * mm, "radius": 2.5 * mm});
            skCircle(sketch, "E41.9.15.1", {"center": v(126, -210) * mm, "radius": 2.5 * mm});
            skCircle(sketch, "E41.9.16.0", {"center": v(119, -231) * mm, "radius": 2.5 * mm});
            skCircle(sketch, "E41.9.16.1", {"center": v(126, -224) * mm, "radius": 2.5 * mm});
            skCircle(sketch, "E41.9.17.0", {"center": v(119, -245) * mm, "radius": 2.5 * mm});
            skCircle(sketch, "E41.9.17.1", {"center": v(126, -238) * mm, "radius": 2.5 * mm});
            skCircle(sketch, "E41.9.18.0", {"center": v(119, -259) * mm, "radius": 2.5 * mm});
            skCircle(sketch, "E41.9.18.1", {"center": v(126, -252) * mm, "radius": 2.5 * mm});
            skCircle(sketch, "E41.9.19.0", {"center": v(119, -273) * mm, "radius": 2.5 * mm});
            skCircle(sketch, "E41.9.19.1", {"center": v(126, -266) * mm, "radius": 2.5 * mm});
            skCircle(sketch, "E41.10.0.0", {"center": v(133, -7) * mm, "radius": 2.5 * mm});
            skCircle(sketch, "E41.10.0.1", {"center": v(140, 0) * mm, "radius": 2.5 * mm});
            skCircle(sketch, "E41.10.1.0", {"center": v(133, -21) * mm, "radius": 2.5 * mm});
            skCircle(sketch, "E41.10.1.1", {"center": v(140, -14) * mm, "radius": 2.5 * mm});
            skCircle(sketch, "E41.10.2.0", {"center": v(133, -35) * mm, "radius": 2.5 * mm});
            skCircle(sketch, "E41.10.2.1", {"center": v(140, -28) * mm, "radius": 2.5 * mm});
            skCircle(sketch, "E41.10.3.0", {"center": v(133, -49) * mm, "radius": 2.5 * mm});
            skCircle(sketch, "E41.10.3.1", {"center": v(140, -42) * mm, "radius": 2.5 * mm});
            skCircle(sketch, "E41.10.4.0", {"center": v(133, -63) * mm, "radius": 2.5 * mm});
            skCircle(sketch, "E41.10.4.1", {"center": v(140, -56) * mm, "radius": 2.5 * mm});
            skCircle(sketch, "E41.10.5.0", {"center": v(133, -77) * mm, "radius": 2.5 * mm});
            skCircle(sketch, "E41.10.5.1", {"center": v(140, -70) * mm, "radius": 2.5 * mm});
            skCircle(sketch, "E41.10.6.0", {"center": v(133, -91) * mm, "radius": 2.5 * mm});
            skCircle(sketch, "E41.10.6.1", {"center": v(140, -84) * mm, "radius": 2.5 * mm});
            skCircle(sketch, "E41.10.7.0", {"center": v(133, -105) * mm, "radius": 2.5 * mm});
            skCircle(sketch, "E41.10.7.1", {"center": v(140, -98) * mm, "radius": 2.5 * mm});
            skCircle(sketch, "E41.10.8.0", {"center": v(133, -119) * mm, "radius": 2.5 * mm});
            skCircle(sketch, "E41.10.8.1", {"center": v(140, -112) * mm, "radius": 2.5 * mm});
            skCircle(sketch, "E41.10.9.0", {"center": v(133, -133) * mm, "radius": 2.5 * mm});
            skCircle(sketch, "E41.10.9.1", {"center": v(140, -126) * mm, "radius": 2.5 * mm});
            skCircle(sketch, "E41.10.10.0", {"center": v(133, -147) * mm, "radius": 2.5 * mm});
            skCircle(sketch, "E41.10.10.1", {"center": v(140, -140) * mm, "radius": 2.5 * mm});
            skCircle(sketch, "E41.10.11.0", {"center": v(133, -161) * mm, "radius": 2.5 * mm});
            skCircle(sketch, "E41.10.11.1", {"center": v(140, -154) * mm, "radius": 2.5 * mm});
            skCircle(sketch, "E41.10.12.0", {"center": v(133, -175) * mm, "radius": 2.5 * mm});
            skCircle(sketch, "E41.10.12.1", {"center": v(140, -168) * mm, "radius": 2.5 * mm});
            skCircle(sketch, "E41.10.13.0", {"center": v(133, -189) * mm, "radius": 2.5 * mm});
            skCircle(sketch, "E41.10.13.1", {"center": v(140, -182) * mm, "radius": 2.5 * mm});
            skCircle(sketch, "E41.10.14.0", {"center": v(133, -203) * mm, "radius": 2.5 * mm});
            skCircle(sketch, "E41.10.14.1", {"center": v(140, -196) * mm, "radius": 2.5 * mm});
            skCircle(sketch, "E41.10.15.0", {"center": v(133, -217) * mm, "radius": 2.5 * mm});
            skCircle(sketch, "E41.10.15.1", {"center": v(140, -210) * mm, "radius": 2.5 * mm});
            skCircle(sketch, "E41.10.16.0", {"center": v(133, -231) * mm, "radius": 2.5 * mm});
            skCircle(sketch, "E41.10.16.1", {"center": v(140, -224) * mm, "radius": 2.5 * mm});
            skCircle(sketch, "E41.10.17.0", {"center": v(133, -245) * mm, "radius": 2.5 * mm});
            skCircle(sketch, "E41.10.17.1", {"center": v(140, -238) * mm, "radius": 2.5 * mm});
            skCircle(sketch, "E41.10.18.0", {"center": v(133, -259) * mm, "radius": 2.5 * mm});
            skCircle(sketch, "E41.10.18.1", {"center": v(140, -252) * mm, "radius": 2.5 * mm});
            skCircle(sketch, "E41.10.19.0", {"center": v(133, -273) * mm, "radius": 2.5 * mm});
            skCircle(sketch, "E41.10.19.1", {"center": v(140, -266) * mm, "radius": 2.5 * mm});
            skCircle(sketch, "E41.11.0.0", {"center": v(147, -7) * mm, "radius": 2.5 * mm});
            skCircle(sketch, "E41.11.0.1", {"center": v(154, 0) * mm, "radius": 2.5 * mm});
            skCircle(sketch, "E41.11.1.0", {"center": v(147, -21) * mm, "radius": 2.5 * mm});
            skCircle(sketch, "E41.11.1.1", {"center": v(154, -14) * mm, "radius": 2.5 * mm});
            skCircle(sketch, "E41.11.2.0", {"center": v(147, -35) * mm, "radius": 2.5 * mm});
            skCircle(sketch, "E41.11.2.1", {"center": v(154, -28) * mm, "radius": 2.5 * mm});
            skCircle(sketch, "E41.11.3.0", {"center": v(147, -49) * mm, "radius": 2.5 * mm});
            skCircle(sketch, "E41.11.3.1", {"center": v(154, -42) * mm, "radius": 2.5 * mm});
            skCircle(sketch, "E41.11.4.0", {"center": v(147, -63) * mm, "radius": 2.5 * mm});
            skCircle(sketch, "E41.11.4.1", {"center": v(154, -56) * mm, "radius": 2.5 * mm});
            skCircle(sketch, "E41.11.5.0", {"center": v(147, -77) * mm, "radius": 2.5 * mm});
            skCircle(sketch, "E41.11.5.1", {"center": v(154, -70) * mm, "radius": 2.5 * mm});
            skCircle(sketch, "E41.11.6.0", {"center": v(147, -91) * mm, "radius": 2.5 * mm});
            skCircle(sketch, "E41.11.6.1", {"center": v(154, -84) * mm, "radius": 2.5 * mm});
            skCircle(sketch, "E41.11.7.0", {"center": v(147, -105) * mm, "radius": 2.5 * mm});
            skCircle(sketch, "E41.11.7.1", {"center": v(154, -98) * mm, "radius": 2.5 * mm});
            skCircle(sketch, "E41.11.8.0", {"center": v(147, -119) * mm, "radius": 2.5 * mm});
            skCircle(sketch, "E41.11.8.1", {"center": v(154, -112) * mm, "radius": 2.5 * mm});
            skCircle(sketch, "E41.11.9.0", {"center": v(147, -133) * mm, "radius": 2.5 * mm});
            skCircle(sketch, "E41.11.9.1", {"center": v(154, -126) * mm, "radius": 2.5 * mm});
            skCircle(sketch, "E41.11.10.0", {"center": v(147, -147) * mm, "radius": 2.5 * mm});
            skCircle(sketch, "E41.11.10.1", {"center": v(154, -140) * mm, "radius": 2.5 * mm});
            skCircle(sketch, "E41.11.11.0", {"center": v(147, -161) * mm, "radius": 2.5 * mm});
            skCircle(sketch, "E41.11.11.1", {"center": v(154, -154) * mm, "radius": 2.5 * mm});
            skCircle(sketch, "E41.11.12.0", {"center": v(147, -175) * mm, "radius": 2.5 * mm});
            skCircle(sketch, "E41.11.12.1", {"center": v(154, -168) * mm, "radius": 2.5 * mm});
            skCircle(sketch, "E41.11.13.0", {"center": v(147, -189) * mm, "radius": 2.5 * mm});
            skCircle(sketch, "E41.11.13.1", {"center": v(154, -182) * mm, "radius": 2.5 * mm});
            skCircle(sketch, "E41.11.14.0", {"center": v(147, -203) * mm, "radius": 2.5 * mm});
            skCircle(sketch, "E41.11.14.1", {"center": v(154, -196) * mm, "radius": 2.5 * mm});
            skCircle(sketch, "E41.11.15.0", {"center": v(147, -217) * mm, "radius": 2.5 * mm});
            skCircle(sketch, "E41.11.15.1", {"center": v(154, -210) * mm, "radius": 2.5 * mm});
            skCircle(sketch, "E41.11.16.0", {"center": v(147, -231) * mm, "radius": 2.5 * mm});
            skCircle(sketch, "E41.11.16.1", {"center": v(154, -224) * mm, "radius": 2.5 * mm});
            skCircle(sketch, "E41.11.17.0", {"center": v(147, -245) * mm, "radius": 2.5 * mm});
            skCircle(sketch, "E41.11.17.1", {"center": v(154, -238) * mm, "radius": 2.5 * mm});
            skCircle(sketch, "E41.11.18.0", {"center": v(147, -259) * mm, "radius": 2.5 * mm});
            skCircle(sketch, "E41.11.18.1", {"center": v(154, -252) * mm, "radius": 2.5 * mm});
            skCircle(sketch, "E41.11.19.0", {"center": v(147, -273) * mm, "radius": 2.5 * mm});
            skCircle(sketch, "E41.11.19.1", {"center": v(154, -266) * mm, "radius": 2.5 * mm});
            skCircle(sketch, "E41.12.0.0", {"center": v(161, -7) * mm, "radius": 2.5 * mm});
            skCircle(sketch, "E41.12.0.1", {"center": v(168, 0) * mm, "radius": 2.5 * mm});
            skCircle(sketch, "E41.12.1.0", {"center": v(161, -21) * mm, "radius": 2.5 * mm});
            skCircle(sketch, "E41.12.1.1", {"center": v(168, -14) * mm, "radius": 2.5 * mm});
            skCircle(sketch, "E41.12.2.0", {"center": v(161, -35) * mm, "radius": 2.5 * mm});
            skCircle(sketch, "E41.12.2.1", {"center": v(168, -28) * mm, "radius": 2.5 * mm});
            skCircle(sketch, "E41.12.3.0", {"center": v(161, -49) * mm, "radius": 2.5 * mm});
            skCircle(sketch, "E41.12.3.1", {"center": v(168, -42) * mm, "radius": 2.5 * mm});
            skCircle(sketch, "E41.12.4.0", {"center": v(161, -63) * mm, "radius": 2.5 * mm});
            skCircle(sketch, "E41.12.4.1", {"center": v(168, -56) * mm, "radius": 2.5 * mm});
            skCircle(sketch, "E41.12.5.0", {"center": v(161, -77) * mm, "radius": 2.5 * mm});
            skCircle(sketch, "E41.12.5.1", {"center": v(168, -70) * mm, "radius": 2.5 * mm});
            skCircle(sketch, "E41.12.6.0", {"center": v(161, -91) * mm, "radius": 2.5 * mm});
            skCircle(sketch, "E41.12.6.1", {"center": v(168, -84) * mm, "radius": 2.5 * mm});
            skCircle(sketch, "E41.12.7.0", {"center": v(161, -105) * mm, "radius": 2.5 * mm});
            skCircle(sketch, "E41.12.7.1", {"center": v(168, -98) * mm, "radius": 2.5 * mm});
            skCircle(sketch, "E41.12.8.0", {"center": v(161, -119) * mm, "radius": 2.5 * mm});
            skCircle(sketch, "E41.12.8.1", {"center": v(168, -112) * mm, "radius": 2.5 * mm});
            skCircle(sketch, "E41.12.9.0", {"center": v(161, -133) * mm, "radius": 2.5 * mm});
            skCircle(sketch, "E41.12.9.1", {"center": v(168, -126) * mm, "radius": 2.5 * mm});
            skCircle(sketch, "E41.12.10.0", {"center": v(161, -147) * mm, "radius": 2.5 * mm});
            skCircle(sketch, "E41.12.10.1", {"center": v(168, -140) * mm, "radius": 2.5 * mm});
            skCircle(sketch, "E41.12.11.0", {"center": v(161, -161) * mm, "radius": 2.5 * mm});
            skCircle(sketch, "E41.12.11.1", {"center": v(168, -154) * mm, "radius": 2.5 * mm});
            skCircle(sketch, "E41.12.12.0", {"center": v(161, -175) * mm, "radius": 2.5 * mm});
            skCircle(sketch, "E41.12.12.1", {"center": v(168, -168) * mm, "radius": 2.5 * mm});
            skCircle(sketch, "E41.12.13.0", {"center": v(161, -189) * mm, "radius": 2.5 * mm});
            skCircle(sketch, "E41.12.13.1", {"center": v(168, -182) * mm, "radius": 2.5 * mm});
            skCircle(sketch, "E41.12.14.0", {"center": v(161, -203) * mm, "radius": 2.5 * mm});
            skCircle(sketch, "E41.12.14.1", {"center": v(168, -196) * mm, "radius": 2.5 * mm});
            skCircle(sketch, "E41.12.15.0", {"center": v(161, -217) * mm, "radius": 2.5 * mm});
            skCircle(sketch, "E41.12.15.1", {"center": v(168, -210) * mm, "radius": 2.5 * mm});
            skCircle(sketch, "E41.12.16.0", {"center": v(161, -231) * mm, "radius": 2.5 * mm});
            skCircle(sketch, "E41.12.16.1", {"center": v(168, -224) * mm, "radius": 2.5 * mm});
            skCircle(sketch, "E41.12.17.0", {"center": v(161, -245) * mm, "radius": 2.5 * mm});
            skCircle(sketch, "E41.12.17.1", {"center": v(168, -238) * mm, "radius": 2.5 * mm});
            skCircle(sketch, "E41.12.18.0", {"center": v(161, -259) * mm, "radius": 2.5 * mm});
            skCircle(sketch, "E41.12.18.1", {"center": v(168, -252) * mm, "radius": 2.5 * mm});
            skCircle(sketch, "E41.12.19.0", {"center": v(161, -273) * mm, "radius": 2.5 * mm});
            skCircle(sketch, "E41.12.19.1", {"center": v(168, -266) * mm, "radius": 2.5 * mm});
            skCircle(sketch, "E41.13.0.0", {"center": v(175, -7) * mm, "radius": 2.5 * mm});
            skCircle(sketch, "E41.13.0.1", {"center": v(182, 0) * mm, "radius": 2.5 * mm});
            skCircle(sketch, "E41.13.1.0", {"center": v(175, -21) * mm, "radius": 2.5 * mm});
            skCircle(sketch, "E41.13.1.1", {"center": v(182, -14) * mm, "radius": 2.5 * mm});
            skCircle(sketch, "E41.13.2.0", {"center": v(175, -35) * mm, "radius": 2.5 * mm});
            skCircle(sketch, "E41.13.2.1", {"center": v(182, -28) * mm, "radius": 2.5 * mm});
            skCircle(sketch, "E41.13.3.0", {"center": v(175, -49) * mm, "radius": 2.5 * mm});
            skCircle(sketch, "E41.13.3.1", {"center": v(182, -42) * mm, "radius": 2.5 * mm});
            skCircle(sketch, "E41.13.4.0", {"center": v(175, -63) * mm, "radius": 2.5 * mm});
            skCircle(sketch, "E41.13.4.1", {"center": v(182, -56) * mm, "radius": 2.5 * mm});
            skCircle(sketch, "E41.13.5.0", {"center": v(175, -77) * mm, "radius": 2.5 * mm});
            skCircle(sketch, "E41.13.5.1", {"center": v(182, -70) * mm, "radius": 2.5 * mm});
            skCircle(sketch, "E41.13.6.0", {"center": v(175, -91) * mm, "radius": 2.5 * mm});
            skCircle(sketch, "E41.13.6.1", {"center": v(182, -84) * mm, "radius": 2.5 * mm});
            skCircle(sketch, "E41.13.7.0", {"center": v(175, -105) * mm, "radius": 2.5 * mm});
            skCircle(sketch, "E41.13.7.1", {"center": v(182, -98) * mm, "radius": 2.5 * mm});
            skCircle(sketch, "E41.13.8.0", {"center": v(175, -119) * mm, "radius": 2.5 * mm});
            skCircle(sketch, "E41.13.8.1", {"center": v(182, -112) * mm, "radius": 2.5 * mm});
            skCircle(sketch, "E41.13.9.0", {"center": v(175, -133) * mm, "radius": 2.5 * mm});
            skCircle(sketch, "E41.13.9.1", {"center": v(182, -126) * mm, "radius": 2.5 * mm});
            skCircle(sketch, "E41.13.10.0", {"center": v(175, -147) * mm, "radius": 2.5 * mm});
            skCircle(sketch, "E41.13.10.1", {"center": v(182, -140) * mm, "radius": 2.5 * mm});
            skCircle(sketch, "E41.13.11.0", {"center": v(175, -161) * mm, "radius": 2.5 * mm});
            skCircle(sketch, "E41.13.11.1", {"center": v(182, -154) * mm, "radius": 2.5 * mm});
            skCircle(sketch, "E41.13.12.0", {"center": v(175, -175) * mm, "radius": 2.5 * mm});
            skCircle(sketch, "E41.13.12.1", {"center": v(182, -168) * mm, "radius": 2.5 * mm});
            skCircle(sketch, "E41.13.13.0", {"center": v(175, -189) * mm, "radius": 2.5 * mm});
            skCircle(sketch, "E41.13.13.1", {"center": v(182, -182) * mm, "radius": 2.5 * mm});
            skCircle(sketch, "E41.13.14.0", {"center": v(175, -203) * mm, "radius": 2.5 * mm});
            skCircle(sketch, "E41.13.14.1", {"center": v(182, -196) * mm, "radius": 2.5 * mm});
            skCircle(sketch, "E41.13.15.0", {"center": v(175, -217) * mm, "radius": 2.5 * mm});
            skCircle(sketch, "E41.13.15.1", {"center": v(182, -210) * mm, "radius": 2.5 * mm});
            skCircle(sketch, "E41.13.16.0", {"center": v(175, -231) * mm, "radius": 2.5 * mm});
            skCircle(sketch, "E41.13.16.1", {"center": v(182, -224) * mm, "radius": 2.5 * mm});
            skCircle(sketch, "E41.13.17.0", {"center": v(175, -245) * mm, "radius": 2.5 * mm});
            skCircle(sketch, "E41.13.17.1", {"center": v(182, -238) * mm, "radius": 2.5 * mm});
            skCircle(sketch, "E41.13.18.0", {"center": v(175, -259) * mm, "radius": 2.5 * mm});
            skCircle(sketch, "E41.13.18.1", {"center": v(182, -252) * mm, "radius": 2.5 * mm});
            skCircle(sketch, "E41.13.19.0", {"center": v(175, -273) * mm, "radius": 2.5 * mm});
            skCircle(sketch, "E41.13.19.1", {"center": v(182, -266) * mm, "radius": 2.5 * mm});
            skCircle(sketch, "E41.14.0.0", {"center": v(189, -7) * mm, "radius": 2.5 * mm});
            skCircle(sketch, "E41.14.0.1", {"center": v(196, 0) * mm, "radius": 2.5 * mm});
            skCircle(sketch, "E41.14.1.0", {"center": v(189, -21) * mm, "radius": 2.5 * mm});
            skCircle(sketch, "E41.14.1.1", {"center": v(196, -14) * mm, "radius": 2.5 * mm});
            skCircle(sketch, "E41.14.2.0", {"center": v(189, -35) * mm, "radius": 2.5 * mm});
            skCircle(sketch, "E41.14.2.1", {"center": v(196, -28) * mm, "radius": 2.5 * mm});
            skCircle(sketch, "E41.14.3.0", {"center": v(189, -49) * mm, "radius": 2.5 * mm});
            skCircle(sketch, "E41.14.3.1", {"center": v(196, -42) * mm, "radius": 2.5 * mm});
            skCircle(sketch, "E41.14.4.0", {"center": v(189, -63) * mm, "radius": 2.5 * mm});
            skCircle(sketch, "E41.14.4.1", {"center": v(196, -56) * mm, "radius": 2.5 * mm});
            skCircle(sketch, "E41.14.5.0", {"center": v(189, -77) * mm, "radius": 2.5 * mm});
            skCircle(sketch, "E41.14.5.1", {"center": v(196, -70) * mm, "radius": 2.5 * mm});
            skCircle(sketch, "E41.14.6.0", {"center": v(189, -91) * mm, "radius": 2.5 * mm});
            skCircle(sketch, "E41.14.6.1", {"center": v(196, -84) * mm, "radius": 2.5 * mm});
            skCircle(sketch, "E41.14.7.0", {"center": v(189, -105) * mm, "radius": 2.5 * mm});
            skCircle(sketch, "E41.14.7.1", {"center": v(196, -98) * mm, "radius": 2.5 * mm});
            skCircle(sketch, "E41.14.8.0", {"center": v(189, -119) * mm, "radius": 2.5 * mm});
            skCircle(sketch, "E41.14.8.1", {"center": v(196, -112) * mm, "radius": 2.5 * mm});
            skCircle(sketch, "E41.14.9.0", {"center": v(189, -133) * mm, "radius": 2.5 * mm});
            skCircle(sketch, "E41.14.9.1", {"center": v(196, -126) * mm, "radius": 2.5 * mm});
            skCircle(sketch, "E41.14.10.0", {"center": v(189, -147) * mm, "radius": 2.5 * mm});
            skCircle(sketch, "E41.14.10.1", {"center": v(196, -140) * mm, "radius": 2.5 * mm});
            skCircle(sketch, "E41.14.11.0", {"center": v(189, -161) * mm, "radius": 2.5 * mm});
            skCircle(sketch, "E41.14.11.1", {"center": v(196, -154) * mm, "radius": 2.5 * mm});
            skCircle(sketch, "E41.14.12.0", {"center": v(189, -175) * mm, "radius": 2.5 * mm});
            skCircle(sketch, "E41.14.12.1", {"center": v(196, -168) * mm, "radius": 2.5 * mm});
            skCircle(sketch, "E41.14.13.0", {"center": v(189, -189) * mm, "radius": 2.5 * mm});
            skCircle(sketch, "E41.14.13.1", {"center": v(196, -182) * mm, "radius": 2.5 * mm});
            skCircle(sketch, "E41.14.14.0", {"center": v(189, -203) * mm, "radius": 2.5 * mm});
            skCircle(sketch, "E41.14.14.1", {"center": v(196, -196) * mm, "radius": 2.5 * mm});
            skCircle(sketch, "E41.14.15.0", {"center": v(189, -217) * mm, "radius": 2.5 * mm});
            skCircle(sketch, "E41.14.15.1", {"center": v(196, -210) * mm, "radius": 2.5 * mm});
            skCircle(sketch, "E41.14.16.0", {"center": v(189, -231) * mm, "radius": 2.5 * mm});
            skCircle(sketch, "E41.14.16.1", {"center": v(196, -224) * mm, "radius": 2.5 * mm});
            skCircle(sketch, "E41.14.17.0", {"center": v(189, -245) * mm, "radius": 2.5 * mm});
            skCircle(sketch, "E41.14.17.1", {"center": v(196, -238) * mm, "radius": 2.5 * mm});
            skCircle(sketch, "E41.14.18.0", {"center": v(189, -259) * mm, "radius": 2.5 * mm});
            skCircle(sketch, "E41.14.18.1", {"center": v(196, -252) * mm, "radius": 2.5 * mm});
            skCircle(sketch, "E41.14.19.0", {"center": v(189, -273) * mm, "radius": 2.5 * mm});
            skCircle(sketch, "E41.14.19.1", {"center": v(196, -266) * mm, "radius": 2.5 * mm});
            skCircle(sketch, "E41.15.0.0", {"center": v(203, -7) * mm, "radius": 2.5 * mm});
            skCircle(sketch, "E41.15.0.1", {"center": v(210, 0) * mm, "radius": 2.5 * mm});
            skCircle(sketch, "E41.15.1.0", {"center": v(203, -21) * mm, "radius": 2.5 * mm});
            skCircle(sketch, "E41.15.1.1", {"center": v(210, -14) * mm, "radius": 2.5 * mm});
            skCircle(sketch, "E41.15.2.0", {"center": v(203, -35) * mm, "radius": 2.5 * mm});
            skCircle(sketch, "E41.15.2.1", {"center": v(210, -28) * mm, "radius": 2.5 * mm});
            skCircle(sketch, "E41.15.3.0", {"center": v(203, -49) * mm, "radius": 2.5 * mm});
            skCircle(sketch, "E41.15.3.1", {"center": v(210, -42) * mm, "radius": 2.5 * mm});
            skCircle(sketch, "E41.15.4.0", {"center": v(203, -63) * mm, "radius": 2.5 * mm});
            skCircle(sketch, "E41.15.4.1", {"center": v(210, -56) * mm, "radius": 2.5 * mm});
            skCircle(sketch, "E41.15.5.0", {"center": v(203, -77) * mm, "radius": 2.5 * mm});
            skCircle(sketch, "E41.15.5.1", {"center": v(210, -70) * mm, "radius": 2.5 * mm});
            skCircle(sketch, "E41.15.6.0", {"center": v(203, -91) * mm, "radius": 2.5 * mm});
            skCircle(sketch, "E41.15.6.1", {"center": v(210, -84) * mm, "radius": 2.5 * mm});
            skCircle(sketch, "E41.15.7.0", {"center": v(203, -105) * mm, "radius": 2.5 * mm});
            skCircle(sketch, "E41.15.7.1", {"center": v(210, -98) * mm, "radius": 2.5 * mm});
            skCircle(sketch, "E41.15.8.0", {"center": v(203, -119) * mm, "radius": 2.5 * mm});
            skCircle(sketch, "E41.15.8.1", {"center": v(210, -112) * mm, "radius": 2.5 * mm});
            skCircle(sketch, "E41.15.9.0", {"center": v(203, -133) * mm, "radius": 2.5 * mm});
            skCircle(sketch, "E41.15.9.1", {"center": v(210, -126) * mm, "radius": 2.5 * mm});
            skCircle(sketch, "E41.15.10.0", {"center": v(203, -147) * mm, "radius": 2.5 * mm});
            skCircle(sketch, "E41.15.10.1", {"center": v(210, -140) * mm, "radius": 2.5 * mm});
            skCircle(sketch, "E41.15.11.0", {"center": v(203, -161) * mm, "radius": 2.5 * mm});
            skCircle(sketch, "E41.15.11.1", {"center": v(210, -154) * mm, "radius": 2.5 * mm});
            skCircle(sketch, "E41.15.12.0", {"center": v(203, -175) * mm, "radius": 2.5 * mm});
            skCircle(sketch, "E41.15.12.1", {"center": v(210, -168) * mm, "radius": 2.5 * mm});
            skCircle(sketch, "E41.15.13.0", {"center": v(203, -189) * mm, "radius": 2.5 * mm});
            skCircle(sketch, "E41.15.13.1", {"center": v(210, -182) * mm, "radius": 2.5 * mm});
            skCircle(sketch, "E41.15.14.0", {"center": v(203, -203) * mm, "radius": 2.5 * mm});
            skCircle(sketch, "E41.15.14.1", {"center": v(210, -196) * mm, "radius": 2.5 * mm});
            skCircle(sketch, "E41.15.15.0", {"center": v(203, -217) * mm, "radius": 2.5 * mm});
            skCircle(sketch, "E41.15.15.1", {"center": v(210, -210) * mm, "radius": 2.5 * mm});
            skCircle(sketch, "E41.15.16.0", {"center": v(203, -231) * mm, "radius": 2.5 * mm});
            skCircle(sketch, "E41.15.16.1", {"center": v(210, -224) * mm, "radius": 2.5 * mm});
            skCircle(sketch, "E41.15.17.0", {"center": v(203, -245) * mm, "radius": 2.5 * mm});
            skCircle(sketch, "E41.15.17.1", {"center": v(210, -238) * mm, "radius": 2.5 * mm});
            skCircle(sketch, "E41.15.18.0", {"center": v(203, -259) * mm, "radius": 2.5 * mm});
            skCircle(sketch, "E41.15.18.1", {"center": v(210, -252) * mm, "radius": 2.5 * mm});
            skCircle(sketch, "E41.15.19.0", {"center": v(203, -273) * mm, "radius": 2.5 * mm});
            skCircle(sketch, "E41.15.19.1", {"center": v(210, -266) * mm, "radius": 2.5 * mm});
            skCircle(sketch, "E41.16.0.0", {"center": v(217, -7) * mm, "radius": 2.5 * mm});
            skCircle(sketch, "E41.16.0.1", {"center": v(224, 0) * mm, "radius": 2.5 * mm});
            skCircle(sketch, "E41.16.1.0", {"center": v(217, -21) * mm, "radius": 2.5 * mm});
            skCircle(sketch, "E41.16.1.1", {"center": v(224, -14) * mm, "radius": 2.5 * mm});
            skCircle(sketch, "E41.16.2.0", {"center": v(217, -35) * mm, "radius": 2.5 * mm});
            skCircle(sketch, "E41.16.2.1", {"center": v(224, -28) * mm, "radius": 2.5 * mm});
            skCircle(sketch, "E41.16.3.0", {"center": v(217, -49) * mm, "radius": 2.5 * mm});
            skCircle(sketch, "E41.16.3.1", {"center": v(224, -42) * mm, "radius": 2.5 * mm});
            skCircle(sketch, "E41.16.4.0", {"center": v(217, -63) * mm, "radius": 2.5 * mm});
            skCircle(sketch, "E41.16.4.1", {"center": v(224, -56) * mm, "radius": 2.5 * mm});
            skCircle(sketch, "E41.16.5.0", {"center": v(217, -77) * mm, "radius": 2.5 * mm});
            skCircle(sketch, "E41.16.5.1", {"center": v(224, -70) * mm, "radius": 2.5 * mm});
            skCircle(sketch, "E41.16.6.0", {"center": v(217, -91) * mm, "radius": 2.5 * mm});
            skCircle(sketch, "E41.16.6.1", {"center": v(224, -84) * mm, "radius": 2.5 * mm});
            skCircle(sketch, "E41.16.7.0", {"center": v(217, -105) * mm, "radius": 2.5 * mm});
            skCircle(sketch, "E41.16.7.1", {"center": v(224, -98) * mm, "radius": 2.5 * mm});
            skCircle(sketch, "E41.16.8.0", {"center": v(217, -119) * mm, "radius": 2.5 * mm});
            skCircle(sketch, "E41.16.8.1", {"center": v(224, -112) * mm, "radius": 2.5 * mm});
            skCircle(sketch, "E41.16.9.0", {"center": v(217, -133) * mm, "radius": 2.5 * mm});
            skCircle(sketch, "E41.16.9.1", {"center": v(224, -126) * mm, "radius": 2.5 * mm});
            skCircle(sketch, "E41.16.10.0", {"center": v(217, -147) * mm, "radius": 2.5 * mm});
            skCircle(sketch, "E41.16.10.1", {"center": v(224, -140) * mm, "radius": 2.5 * mm});
            skCircle(sketch, "E41.16.11.0", {"center": v(217, -161) * mm, "radius": 2.5 * mm});
            skCircle(sketch, "E41.16.11.1", {"center": v(224, -154) * mm, "radius": 2.5 * mm});
            skCircle(sketch, "E41.16.12.0", {"center": v(217, -175) * mm, "radius": 2.5 * mm});
            skCircle(sketch, "E41.16.12.1", {"center": v(224, -168) * mm, "radius": 2.5 * mm});
            skCircle(sketch, "E41.16.13.0", {"center": v(217, -189) * mm, "radius": 2.5 * mm});
            skCircle(sketch, "E41.16.13.1", {"center": v(224, -182) * mm, "radius": 2.5 * mm});
            skCircle(sketch, "E41.16.14.0", {"center": v(217, -203) * mm, "radius": 2.5 * mm});
            skCircle(sketch, "E41.16.14.1", {"center": v(224, -196) * mm, "radius": 2.5 * mm});
            skCircle(sketch, "E41.16.15.0", {"center": v(217, -217) * mm, "radius": 2.5 * mm});
            skCircle(sketch, "E41.16.15.1", {"center": v(224, -210) * mm, "radius": 2.5 * mm});
            skCircle(sketch, "E41.16.16.0", {"center": v(217, -231) * mm, "radius": 2.5 * mm});
            skCircle(sketch, "E41.16.16.1", {"center": v(224, -224) * mm, "radius": 2.5 * mm});
            skCircle(sketch, "E41.16.17.0", {"center": v(217, -245) * mm, "radius": 2.5 * mm});
            skCircle(sketch, "E41.16.17.1", {"center": v(224, -238) * mm, "radius": 2.5 * mm});
            skCircle(sketch, "E41.16.18.0", {"center": v(217, -259) * mm, "radius": 2.5 * mm});
            skCircle(sketch, "E41.16.18.1", {"center": v(224, -252) * mm, "radius": 2.5 * mm});
            skCircle(sketch, "E41.16.19.0", {"center": v(217, -273) * mm, "radius": 2.5 * mm});
            skCircle(sketch, "E41.16.19.1", {"center": v(224, -266) * mm, "radius": 2.5 * mm});
            skCircle(sketch, "E41.17.0.0", {"center": v(231, -7) * mm, "radius": 2.5 * mm});
            skCircle(sketch, "E41.17.0.1", {"center": v(238, 0) * mm, "radius": 2.5 * mm});
            skCircle(sketch, "E41.17.1.0", {"center": v(231, -21) * mm, "radius": 2.5 * mm});
            skCircle(sketch, "E41.17.1.1", {"center": v(238, -14) * mm, "radius": 2.5 * mm});
            skCircle(sketch, "E41.17.2.0", {"center": v(231, -35) * mm, "radius": 2.5 * mm});
            skCircle(sketch, "E41.17.2.1", {"center": v(238, -28) * mm, "radius": 2.5 * mm});
            skCircle(sketch, "E41.17.3.0", {"center": v(231, -49) * mm, "radius": 2.5 * mm});
            skCircle(sketch, "E41.17.3.1", {"center": v(238, -42) * mm, "radius": 2.5 * mm});
            skCircle(sketch, "E41.17.4.0", {"center": v(231, -63) * mm, "radius": 2.5 * mm});
            skCircle(sketch, "E41.17.4.1", {"center": v(238, -56) * mm, "radius": 2.5 * mm});
            skCircle(sketch, "E41.17.5.0", {"center": v(231, -77) * mm, "radius": 2.5 * mm});
            skCircle(sketch, "E41.17.5.1", {"center": v(238, -70) * mm, "radius": 2.5 * mm});
            skCircle(sketch, "E41.17.6.0", {"center": v(231, -91) * mm, "radius": 2.5 * mm});
            skCircle(sketch, "E41.17.6.1", {"center": v(238, -84) * mm, "radius": 2.5 * mm});
            skCircle(sketch, "E41.17.7.0", {"center": v(231, -105) * mm, "radius": 2.5 * mm});
            skCircle(sketch, "E41.17.7.1", {"center": v(238, -98) * mm, "radius": 2.5 * mm});
            skCircle(sketch, "E41.17.8.0", {"center": v(231, -119) * mm, "radius": 2.5 * mm});
            skCircle(sketch, "E41.17.8.1", {"center": v(238, -112) * mm, "radius": 2.5 * mm});
            skCircle(sketch, "E41.17.9.0", {"center": v(231, -133) * mm, "radius": 2.5 * mm});
            skCircle(sketch, "E41.17.9.1", {"center": v(238, -126) * mm, "radius": 2.5 * mm});
            skCircle(sketch, "E41.17.10.0", {"center": v(231, -147) * mm, "radius": 2.5 * mm});
            skCircle(sketch, "E41.17.10.1", {"center": v(238, -140) * mm, "radius": 2.5 * mm});
            skCircle(sketch, "E41.17.11.0", {"center": v(231, -161) * mm, "radius": 2.5 * mm});
            skCircle(sketch, "E41.17.11.1", {"center": v(238, -154) * mm, "radius": 2.5 * mm});
            skCircle(sketch, "E41.17.12.0", {"center": v(231, -175) * mm, "radius": 2.5 * mm});
            skCircle(sketch, "E41.17.12.1", {"center": v(238, -168) * mm, "radius": 2.5 * mm});
            skCircle(sketch, "E41.17.13.0", {"center": v(231, -189) * mm, "radius": 2.5 * mm});
            skCircle(sketch, "E41.17.13.1", {"center": v(238, -182) * mm, "radius": 2.5 * mm});
            skCircle(sketch, "E41.17.14.0", {"center": v(231, -203) * mm, "radius": 2.5 * mm});
            skCircle(sketch, "E41.17.14.1", {"center": v(238, -196) * mm, "radius": 2.5 * mm});
            skCircle(sketch, "E41.17.15.0", {"center": v(231, -217) * mm, "radius": 2.5 * mm});
            skCircle(sketch, "E41.17.15.1", {"center": v(238, -210) * mm, "radius": 2.5 * mm});
            skCircle(sketch, "E41.17.16.0", {"center": v(231, -231) * mm, "radius": 2.5 * mm});
            skCircle(sketch, "E41.17.16.1", {"center": v(238, -224) * mm, "radius": 2.5 * mm});
            skCircle(sketch, "E41.17.17.0", {"center": v(231, -245) * mm, "radius": 2.5 * mm});
            skCircle(sketch, "E41.17.17.1", {"center": v(238, -238) * mm, "radius": 2.5 * mm});
            skCircle(sketch, "E41.17.18.0", {"center": v(231, -259) * mm, "radius": 2.5 * mm});
            skCircle(sketch, "E41.17.18.1", {"center": v(238, -252) * mm, "radius": 2.5 * mm});
            skCircle(sketch, "E41.17.19.0", {"center": v(231, -273) * mm, "radius": 2.5 * mm});
            skCircle(sketch, "E41.17.19.1", {"center": v(238, -266) * mm, "radius": 2.5 * mm});
            skCircle(sketch, "E41.18.0.0", {"center": v(245, -7) * mm, "radius": 2.5 * mm});
            skCircle(sketch, "E41.18.0.1", {"center": v(252, 0) * mm, "radius": 2.5 * mm});
            skCircle(sketch, "E41.18.1.0", {"center": v(245, -21) * mm, "radius": 2.5 * mm});
            skCircle(sketch, "E41.18.1.1", {"center": v(252, -14) * mm, "radius": 2.5 * mm});
            skCircle(sketch, "E41.18.2.0", {"center": v(245, -35) * mm, "radius": 2.5 * mm});
            skCircle(sketch, "E41.18.2.1", {"center": v(252, -28) * mm, "radius": 2.5 * mm});
            skCircle(sketch, "E41.18.3.0", {"center": v(245, -49) * mm, "radius": 2.5 * mm});
            skCircle(sketch, "E41.18.3.1", {"center": v(252, -42) * mm, "radius": 2.5 * mm});
            skCircle(sketch, "E41.18.4.0", {"center": v(245, -63) * mm, "radius": 2.5 * mm});
            skCircle(sketch, "E41.18.4.1", {"center": v(252, -56) * mm, "radius": 2.5 * mm});
            skCircle(sketch, "E41.18.5.0", {"center": v(245, -77) * mm, "radius": 2.5 * mm});
            skCircle(sketch, "E41.18.5.1", {"center": v(252, -70) * mm, "radius": 2.5 * mm});
            skCircle(sketch, "E41.18.6.0", {"center": v(245, -91) * mm, "radius": 2.5 * mm});
            skCircle(sketch, "E41.18.6.1", {"center": v(252, -84) * mm, "radius": 2.5 * mm});
            skCircle(sketch, "E41.18.7.0", {"center": v(245, -105) * mm, "radius": 2.5 * mm});
            skCircle(sketch, "E41.18.7.1", {"center": v(252, -98) * mm, "radius": 2.5 * mm});
            skCircle(sketch, "E41.18.8.0", {"center": v(245, -119) * mm, "radius": 2.5 * mm});
            skCircle(sketch, "E41.18.8.1", {"center": v(252, -112) * mm, "radius": 2.5 * mm});
            skCircle(sketch, "E41.18.9.0", {"center": v(245, -133) * mm, "radius": 2.5 * mm});
            skCircle(sketch, "E41.18.9.1", {"center": v(252, -126) * mm, "radius": 2.5 * mm});
            skCircle(sketch, "E41.18.10.0", {"center": v(245, -147) * mm, "radius": 2.5 * mm});
            skCircle(sketch, "E41.18.10.1", {"center": v(252, -140) * mm, "radius": 2.5 * mm});
            skCircle(sketch, "E41.18.11.0", {"center": v(245, -161) * mm, "radius": 2.5 * mm});
            skCircle(sketch, "E41.18.11.1", {"center": v(252, -154) * mm, "radius": 2.5 * mm});
            skCircle(sketch, "E41.18.12.0", {"center": v(245, -175) * mm, "radius": 2.5 * mm});
            skCircle(sketch, "E41.18.12.1", {"center": v(252, -168) * mm, "radius": 2.5 * mm});
            skCircle(sketch, "E41.18.13.0", {"center": v(245, -189) * mm, "radius": 2.5 * mm});
            skCircle(sketch, "E41.18.13.1", {"center": v(252, -182) * mm, "radius": 2.5 * mm});
            skCircle(sketch, "E41.18.14.0", {"center": v(245, -203) * mm, "radius": 2.5 * mm});
            skCircle(sketch, "E41.18.14.1", {"center": v(252, -196) * mm, "radius": 2.5 * mm});
            skCircle(sketch, "E41.18.15.0", {"center": v(245, -217) * mm, "radius": 2.5 * mm});
            skCircle(sketch, "E41.18.15.1", {"center": v(252, -210) * mm, "radius": 2.5 * mm});
            skCircle(sketch, "E41.18.16.0", {"center": v(245, -231) * mm, "radius": 2.5 * mm});
            skCircle(sketch, "E41.18.16.1", {"center": v(252, -224) * mm, "radius": 2.5 * mm});
            skCircle(sketch, "E41.18.17.0", {"center": v(245, -245) * mm, "radius": 2.5 * mm});
            skCircle(sketch, "E41.18.17.1", {"center": v(252, -238) * mm, "radius": 2.5 * mm});
            skCircle(sketch, "E41.18.18.0", {"center": v(245, -259) * mm, "radius": 2.5 * mm});
            skCircle(sketch, "E41.18.18.1", {"center": v(252, -252) * mm, "radius": 2.5 * mm});
            skCircle(sketch, "E41.18.19.0", {"center": v(245, -273) * mm, "radius": 2.5 * mm});
            skCircle(sketch, "E41.18.19.1", {"center": v(252, -266) * mm, "radius": 2.5 * mm});
            skCircle(sketch, "E41.19.0.0", {"center": v(259, -7) * mm, "radius": 2.5 * mm});
            skCircle(sketch, "E41.19.0.1", {"center": v(266, 0) * mm, "radius": 2.5 * mm});
            skCircle(sketch, "E41.19.1.0", {"center": v(259, -21) * mm, "radius": 2.5 * mm});
            skCircle(sketch, "E41.19.1.1", {"center": v(266, -14) * mm, "radius": 2.5 * mm});
            skCircle(sketch, "E41.19.2.0", {"center": v(259, -35) * mm, "radius": 2.5 * mm});
            skCircle(sketch, "E41.19.2.1", {"center": v(266, -28) * mm, "radius": 2.5 * mm});
            skCircle(sketch, "E41.19.3.0", {"center": v(259, -49) * mm, "radius": 2.5 * mm});
            skCircle(sketch, "E41.19.3.1", {"center": v(266, -42) * mm, "radius": 2.5 * mm});
            skCircle(sketch, "E41.19.4.0", {"center": v(259, -63) * mm, "radius": 2.5 * mm});
            skCircle(sketch, "E41.19.4.1", {"center": v(266, -56) * mm, "radius": 2.5 * mm});
            skCircle(sketch, "E41.19.5.0", {"center": v(259, -77) * mm, "radius": 2.5 * mm});
            skCircle(sketch, "E41.19.5.1", {"center": v(266, -70) * mm, "radius": 2.5 * mm});
            skCircle(sketch, "E41.19.6.0", {"center": v(259, -91) * mm, "radius": 2.5 * mm});
            skCircle(sketch, "E41.19.6.1", {"center": v(266, -84) * mm, "radius": 2.5 * mm});
            skCircle(sketch, "E41.19.7.0", {"center": v(259, -105) * mm, "radius": 2.5 * mm});
            skCircle(sketch, "E41.19.7.1", {"center": v(266, -98) * mm, "radius": 2.5 * mm});
            skCircle(sketch, "E41.19.8.0", {"center": v(259, -119) * mm, "radius": 2.5 * mm});
            skCircle(sketch, "E41.19.8.1", {"center": v(266, -112) * mm, "radius": 2.5 * mm});
            skCircle(sketch, "E41.19.9.0", {"center": v(259, -133) * mm, "radius": 2.5 * mm});
            skCircle(sketch, "E41.19.9.1", {"center": v(266, -126) * mm, "radius": 2.5 * mm});
            skCircle(sketch, "E41.19.10.0", {"center": v(259, -147) * mm, "radius": 2.5 * mm});
            skCircle(sketch, "E41.19.10.1", {"center": v(266, -140) * mm, "radius": 2.5 * mm});
            skCircle(sketch, "E41.19.11.0", {"center": v(259, -161) * mm, "radius": 2.5 * mm});
            skCircle(sketch, "E41.19.11.1", {"center": v(266, -154) * mm, "radius": 2.5 * mm});
            skCircle(sketch, "E41.19.12.0", {"center": v(259, -175) * mm, "radius": 2.5 * mm});
            skCircle(sketch, "E41.19.12.1", {"center": v(266, -168) * mm, "radius": 2.5 * mm});
            skCircle(sketch, "E41.19.13.0", {"center": v(259, -189) * mm, "radius": 2.5 * mm});
            skCircle(sketch, "E41.19.13.1", {"center": v(266, -182) * mm, "radius": 2.5 * mm});
            skCircle(sketch, "E41.19.14.0", {"center": v(259, -203) * mm, "radius": 2.5 * mm});
            skCircle(sketch, "E41.19.14.1", {"center": v(266, -196) * mm, "radius": 2.5 * mm});
            skCircle(sketch, "E41.19.15.0", {"center": v(259, -217) * mm, "radius": 2.5 * mm});
            skCircle(sketch, "E41.19.15.1", {"center": v(266, -210) * mm, "radius": 2.5 * mm});
            skCircle(sketch, "E41.19.16.0", {"center": v(259, -231) * mm, "radius": 2.5 * mm});
            skCircle(sketch, "E41.19.16.1", {"center": v(266, -224) * mm, "radius": 2.5 * mm});
            skCircle(sketch, "E41.19.17.0", {"center": v(259, -245) * mm, "radius": 2.5 * mm});
            skCircle(sketch, "E41.19.17.1", {"center": v(266, -238) * mm, "radius": 2.5 * mm});
            skCircle(sketch, "E41.19.18.0", {"center": v(259, -259) * mm, "radius": 2.5 * mm});
            skCircle(sketch, "E41.19.18.1", {"center": v(266, -252) * mm, "radius": 2.5 * mm});
            skCircle(sketch, "E41.19.19.0", {"center": v(259, -273) * mm, "radius": 2.5 * mm});
            skCircle(sketch, "E41.19.19.1", {"center": v(266, -266) * mm, "radius": 2.5 * mm});
            skCircle(sketch, "E41.20.0.0", {"center": v(273, -7) * mm, "radius": 2.5 * mm});
            skCircle(sketch, "E41.20.0.1", {"center": v(280, 0) * mm, "radius": 2.5 * mm});
            skCircle(sketch, "E41.20.1.0", {"center": v(273, -21) * mm, "radius": 2.5 * mm});
            skCircle(sketch, "E41.20.1.1", {"center": v(280, -14) * mm, "radius": 2.5 * mm});
            skCircle(sketch, "E41.20.2.0", {"center": v(273, -35) * mm, "radius": 2.5 * mm});
            skCircle(sketch, "E41.20.2.1", {"center": v(280, -28) * mm, "radius": 2.5 * mm});
            skCircle(sketch, "E41.20.3.0", {"center": v(273, -49) * mm, "radius": 2.5 * mm});
            skCircle(sketch, "E41.20.3.1", {"center": v(280, -42) * mm, "radius": 2.5 * mm});
            skCircle(sketch, "E41.20.4.0", {"center": v(273, -63) * mm, "radius": 2.5 * mm});
            skCircle(sketch, "E41.20.4.1", {"center": v(280, -56) * mm, "radius": 2.5 * mm});
            skCircle(sketch, "E41.20.5.0", {"center": v(273, -77) * mm, "radius": 2.5 * mm});
            skCircle(sketch, "E41.20.5.1", {"center": v(280, -70) * mm, "radius": 2.5 * mm});
            skCircle(sketch, "E41.20.6.0", {"center": v(273, -91) * mm, "radius": 2.5 * mm});
            skCircle(sketch, "E41.20.6.1", {"center": v(280, -84) * mm, "radius": 2.5 * mm});
            skCircle(sketch, "E41.20.7.0", {"center": v(273, -105) * mm, "radius": 2.5 * mm});
            skCircle(sketch, "E41.20.7.1", {"center": v(280, -98) * mm, "radius": 2.5 * mm});
            skCircle(sketch, "E41.20.8.0", {"center": v(273, -119) * mm, "radius": 2.5 * mm});
            skCircle(sketch, "E41.20.8.1", {"center": v(280, -112) * mm, "radius": 2.5 * mm});
            skCircle(sketch, "E41.20.9.0", {"center": v(273, -133) * mm, "radius": 2.5 * mm});
            skCircle(sketch, "E41.20.9.1", {"center": v(280, -126) * mm, "radius": 2.5 * mm});
            skCircle(sketch, "E41.20.10.0", {"center": v(273, -147) * mm, "radius": 2.5 * mm});
            skCircle(sketch, "E41.20.10.1", {"center": v(280, -140) * mm, "radius": 2.5 * mm});
            skCircle(sketch, "E41.20.11.0", {"center": v(273, -161) * mm, "radius": 2.5 * mm});
            skCircle(sketch, "E41.20.11.1", {"center": v(280, -154) * mm, "radius": 2.5 * mm});
            skCircle(sketch, "E41.20.12.0", {"center": v(273, -175) * mm, "radius": 2.5 * mm});
            skCircle(sketch, "E41.20.12.1", {"center": v(280, -168) * mm, "radius": 2.5 * mm});
            skCircle(sketch, "E41.20.13.0", {"center": v(273, -189) * mm, "radius": 2.5 * mm});
            skCircle(sketch, "E41.20.13.1", {"center": v(280, -182) * mm, "radius": 2.5 * mm});
            skCircle(sketch, "E41.20.14.0", {"center": v(273, -203) * mm, "radius": 2.5 * mm});
            skCircle(sketch, "E41.20.14.1", {"center": v(280, -196) * mm, "radius": 2.5 * mm});
            skCircle(sketch, "E41.20.15.0", {"center": v(273, -217) * mm, "radius": 2.5 * mm});
            skCircle(sketch, "E41.20.15.1", {"center": v(280, -210) * mm, "radius": 2.5 * mm});
            skCircle(sketch, "E41.20.16.0", {"center": v(273, -231) * mm, "radius": 2.5 * mm});
            skCircle(sketch, "E41.20.16.1", {"center": v(280, -224) * mm, "radius": 2.5 * mm});
            skCircle(sketch, "E41.20.17.0", {"center": v(273, -245) * mm, "radius": 2.5 * mm});
            skCircle(sketch, "E41.20.17.1", {"center": v(280, -238) * mm, "radius": 2.5 * mm});
            skCircle(sketch, "E41.20.18.0", {"center": v(273, -259) * mm, "radius": 2.5 * mm});
            skCircle(sketch, "E41.20.18.1", {"center": v(280, -252) * mm, "radius": 2.5 * mm});
            skCircle(sketch, "E41.20.19.0", {"center": v(273, -273) * mm, "radius": 2.5 * mm});
            skCircle(sketch, "E41.20.19.1", {"center": v(280, -266) * mm, "radius": 2.5 * mm});
            skCircle(sketch, "E41.21.0.0", {"center": v(287, -7) * mm, "radius": 2.5 * mm});
            skCircle(sketch, "E41.21.0.1", {"center": v(294, 0) * mm, "radius": 2.5 * mm});
            skCircle(sketch, "E41.21.1.0", {"center": v(287, -21) * mm, "radius": 2.5 * mm});
            skCircle(sketch, "E41.21.1.1", {"center": v(294, -14) * mm, "radius": 2.5 * mm});
            skCircle(sketch, "E41.21.2.0", {"center": v(287, -35) * mm, "radius": 2.5 * mm});
            skCircle(sketch, "E41.21.2.1", {"center": v(294, -28) * mm, "radius": 2.5 * mm});
            skCircle(sketch, "E41.21.3.0", {"center": v(287, -49) * mm, "radius": 2.5 * mm});
            skCircle(sketch, "E41.21.3.1", {"center": v(294, -42) * mm, "radius": 2.5 * mm});
            skCircle(sketch, "E41.21.4.0", {"center": v(287, -63) * mm, "radius": 2.5 * mm});
            skCircle(sketch, "E41.21.4.1", {"center": v(294, -56) * mm, "radius": 2.5 * mm});
            skCircle(sketch, "E41.21.5.0", {"center": v(287, -77) * mm, "radius": 2.5 * mm});
            skCircle(sketch, "E41.21.5.1", {"center": v(294, -70) * mm, "radius": 2.5 * mm});
            skCircle(sketch, "E41.21.6.0", {"center": v(287, -91) * mm, "radius": 2.5 * mm});
            skCircle(sketch, "E41.21.6.1", {"center": v(294, -84) * mm, "radius": 2.5 * mm});
            skCircle(sketch, "E41.21.7.0", {"center": v(287, -105) * mm, "radius": 2.5 * mm});
            skCircle(sketch, "E41.21.7.1", {"center": v(294, -98) * mm, "radius": 2.5 * mm});
            skCircle(sketch, "E41.21.8.0", {"center": v(287, -119) * mm, "radius": 2.5 * mm});
            skCircle(sketch, "E41.21.8.1", {"center": v(294, -112) * mm, "radius": 2.5 * mm});
            skCircle(sketch, "E41.21.9.0", {"center": v(287, -133) * mm, "radius": 2.5 * mm});
            skCircle(sketch, "E41.21.9.1", {"center": v(294, -126) * mm, "radius": 2.5 * mm});
            skCircle(sketch, "E41.21.10.0", {"center": v(287, -147) * mm, "radius": 2.5 * mm});
            skCircle(sketch, "E41.21.10.1", {"center": v(294, -140) * mm, "radius": 2.5 * mm});
            skCircle(sketch, "E41.21.11.0", {"center": v(287, -161) * mm, "radius": 2.5 * mm});
            skCircle(sketch, "E41.21.11.1", {"center": v(294, -154) * mm, "radius": 2.5 * mm});
            skCircle(sketch, "E41.21.12.0", {"center": v(287, -175) * mm, "radius": 2.5 * mm});
            skCircle(sketch, "E41.21.12.1", {"center": v(294, -168) * mm, "radius": 2.5 * mm});
            skCircle(sketch, "E41.21.13.0", {"center": v(287, -189) * mm, "radius": 2.5 * mm});
            skCircle(sketch, "E41.21.13.1", {"center": v(294, -182) * mm, "radius": 2.5 * mm});
            skCircle(sketch, "E41.21.14.0", {"center": v(287, -203) * mm, "radius": 2.5 * mm});
            skCircle(sketch, "E41.21.14.1", {"center": v(294, -196) * mm, "radius": 2.5 * mm});
            skCircle(sketch, "E41.21.15.0", {"center": v(287, -217) * mm, "radius": 2.5 * mm});
            skCircle(sketch, "E41.21.15.1", {"center": v(294, -210) * mm, "radius": 2.5 * mm});
            skCircle(sketch, "E41.21.16.0", {"center": v(287, -231) * mm, "radius": 2.5 * mm});
            skCircle(sketch, "E41.21.16.1", {"center": v(294, -224) * mm, "radius": 2.5 * mm});
            skCircle(sketch, "E41.21.17.0", {"center": v(287, -245) * mm, "radius": 2.5 * mm});
            skCircle(sketch, "E41.21.17.1", {"center": v(294, -238) * mm, "radius": 2.5 * mm});
            skCircle(sketch, "E41.21.18.0", {"center": v(287, -259) * mm, "radius": 2.5 * mm});
            skCircle(sketch, "E41.21.18.1", {"center": v(294, -252) * mm, "radius": 2.5 * mm});
            skCircle(sketch, "E41.21.19.0", {"center": v(287, -273) * mm, "radius": 2.5 * mm});
            skCircle(sketch, "E41.21.19.1", {"center": v(294, -266) * mm, "radius": 2.5 * mm});
            skCircle(sketch, "E41.22.0.0", {"center": v(301, -7) * mm, "radius": 2.5 * mm});
            skCircle(sketch, "E41.22.0.1", {"center": v(308, 0) * mm, "radius": 2.5 * mm});
            skCircle(sketch, "E41.22.1.0", {"center": v(301, -21) * mm, "radius": 2.5 * mm});
            skCircle(sketch, "E41.22.1.1", {"center": v(308, -14) * mm, "radius": 2.5 * mm});
            skCircle(sketch, "E41.22.2.0", {"center": v(301, -35) * mm, "radius": 2.5 * mm});
            skCircle(sketch, "E41.22.2.1", {"center": v(308, -28) * mm, "radius": 2.5 * mm});
            skCircle(sketch, "E41.22.3.0", {"center": v(301, -49) * mm, "radius": 2.5 * mm});
            skCircle(sketch, "E41.22.3.1", {"center": v(308, -42) * mm, "radius": 2.5 * mm});
            skCircle(sketch, "E41.22.4.0", {"center": v(301, -63) * mm, "radius": 2.5 * mm});
            skCircle(sketch, "E41.22.4.1", {"center": v(308, -56) * mm, "radius": 2.5 * mm});
            skCircle(sketch, "E41.22.5.0", {"center": v(301, -77) * mm, "radius": 2.5 * mm});
            skCircle(sketch, "E41.22.5.1", {"center": v(308, -70) * mm, "radius": 2.5 * mm});
            skCircle(sketch, "E41.22.6.0", {"center": v(301, -91) * mm, "radius": 2.5 * mm});
            skCircle(sketch, "E41.22.6.1", {"center": v(308, -84) * mm, "radius": 2.5 * mm});
            skCircle(sketch, "E41.22.7.0", {"center": v(301, -105) * mm, "radius": 2.5 * mm});
            skCircle(sketch, "E41.22.7.1", {"center": v(308, -98) * mm, "radius": 2.5 * mm});
            skCircle(sketch, "E41.22.8.0", {"center": v(301, -119) * mm, "radius": 2.5 * mm});
            skCircle(sketch, "E41.22.8.1", {"center": v(308, -112) * mm, "radius": 2.5 * mm});
            skCircle(sketch, "E41.22.9.0", {"center": v(301, -133) * mm, "radius": 2.5 * mm});
            skCircle(sketch, "E41.22.9.1", {"center": v(308, -126) * mm, "radius": 2.5 * mm});
            skCircle(sketch, "E41.22.10.0", {"center": v(301, -147) * mm, "radius": 2.5 * mm});
            skCircle(sketch, "E41.22.10.1", {"center": v(308, -140) * mm, "radius": 2.5 * mm});
            skCircle(sketch, "E41.22.11.0", {"center": v(301, -161) * mm, "radius": 2.5 * mm});
            skCircle(sketch, "E41.22.11.1", {"center": v(308, -154) * mm, "radius": 2.5 * mm});
            skCircle(sketch, "E41.22.12.0", {"center": v(301, -175) * mm, "radius": 2.5 * mm});
            skCircle(sketch, "E41.22.12.1", {"center": v(308, -168) * mm, "radius": 2.5 * mm});
            skCircle(sketch, "E41.22.13.0", {"center": v(301, -189) * mm, "radius": 2.5 * mm});
            skCircle(sketch, "E41.22.13.1", {"center": v(308, -182) * mm, "radius": 2.5 * mm});
            skCircle(sketch, "E41.22.14.0", {"center": v(301, -203) * mm, "radius": 2.5 * mm});
            skCircle(sketch, "E41.22.14.1", {"center": v(308, -196) * mm, "radius": 2.5 * mm});
            skCircle(sketch, "E41.22.15.0", {"center": v(301, -217) * mm, "radius": 2.5 * mm});
            skCircle(sketch, "E41.22.15.1", {"center": v(308, -210) * mm, "radius": 2.5 * mm});
            skCircle(sketch, "E41.22.16.0", {"center": v(301, -231) * mm, "radius": 2.5 * mm});
            skCircle(sketch, "E41.22.16.1", {"center": v(308, -224) * mm, "radius": 2.5 * mm});
            skCircle(sketch, "E41.22.17.0", {"center": v(301, -245) * mm, "radius": 2.5 * mm});
            skCircle(sketch, "E41.22.17.1", {"center": v(308, -238) * mm, "radius": 2.5 * mm});
            skCircle(sketch, "E41.22.18.0", {"center": v(301, -259) * mm, "radius": 2.5 * mm});
            skCircle(sketch, "E41.22.18.1", {"center": v(308, -252) * mm, "radius": 2.5 * mm});
            skCircle(sketch, "E41.22.19.0", {"center": v(301, -273) * mm, "radius": 2.5 * mm});
            skCircle(sketch, "E41.22.19.1", {"center": v(308, -266) * mm, "radius": 2.5 * mm});
            skCircle(sketch, "E41.23.0.0", {"center": v(315, -7) * mm, "radius": 2.5 * mm});
            skCircle(sketch, "E41.23.0.1", {"center": v(322, 0) * mm, "radius": 2.5 * mm});
            skCircle(sketch, "E41.23.1.0", {"center": v(315, -21) * mm, "radius": 2.5 * mm});
            skCircle(sketch, "E41.23.1.1", {"center": v(322, -14) * mm, "radius": 2.5 * mm});
            skCircle(sketch, "E41.23.2.0", {"center": v(315, -35) * mm, "radius": 2.5 * mm});
            skCircle(sketch, "E41.23.2.1", {"center": v(322, -28) * mm, "radius": 2.5 * mm});
            skCircle(sketch, "E41.23.3.0", {"center": v(315, -49) * mm, "radius": 2.5 * mm});
            skCircle(sketch, "E41.23.3.1", {"center": v(322, -42) * mm, "radius": 2.5 * mm});
            skCircle(sketch, "E41.23.4.0", {"center": v(315, -63) * mm, "radius": 2.5 * mm});
            skCircle(sketch, "E41.23.4.1", {"center": v(322, -56) * mm, "radius": 2.5 * mm});
            skCircle(sketch, "E41.23.5.0", {"center": v(315, -77) * mm, "radius": 2.5 * mm});
            skCircle(sketch, "E41.23.5.1", {"center": v(322, -70) * mm, "radius": 2.5 * mm});
            skCircle(sketch, "E41.23.6.0", {"center": v(315, -91) * mm, "radius": 2.5 * mm});
            skCircle(sketch, "E41.23.6.1", {"center": v(322, -84) * mm, "radius": 2.5 * mm});
            skCircle(sketch, "E41.23.7.0", {"center": v(315, -105) * mm, "radius": 2.5 * mm});
            skCircle(sketch, "E41.23.7.1", {"center": v(322, -98) * mm, "radius": 2.5 * mm});
            skCircle(sketch, "E41.23.8.0", {"center": v(315, -119) * mm, "radius": 2.5 * mm});
            skCircle(sketch, "E41.23.8.1", {"center": v(322, -112) * mm, "radius": 2.5 * mm});
            skCircle(sketch, "E41.23.9.0", {"center": v(315, -133) * mm, "radius": 2.5 * mm});
            skCircle(sketch, "E41.23.9.1", {"center": v(322, -126) * mm, "radius": 2.5 * mm});
            skCircle(sketch, "E41.23.10.0", {"center": v(315, -147) * mm, "radius": 2.5 * mm});
            skCircle(sketch, "E41.23.10.1", {"center": v(322, -140) * mm, "radius": 2.5 * mm});
            skCircle(sketch, "E41.23.11.0", {"center": v(315, -161) * mm, "radius": 2.5 * mm});
            skCircle(sketch, "E41.23.11.1", {"center": v(322, -154) * mm, "radius": 2.5 * mm});
            skCircle(sketch, "E41.23.12.0", {"center": v(315, -175) * mm, "radius": 2.5 * mm});
            skCircle(sketch, "E41.23.12.1", {"center": v(322, -168) * mm, "radius": 2.5 * mm});
            skCircle(sketch, "E41.23.13.0", {"center": v(315, -189) * mm, "radius": 2.5 * mm});
            skCircle(sketch, "E41.23.13.1", {"center": v(322, -182) * mm, "radius": 2.5 * mm});
            skCircle(sketch, "E41.23.14.0", {"center": v(315, -203) * mm, "radius": 2.5 * mm});
            skCircle(sketch, "E41.23.14.1", {"center": v(322, -196) * mm, "radius": 2.5 * mm});
            skCircle(sketch, "E41.23.15.0", {"center": v(315, -217) * mm, "radius": 2.5 * mm});
            skCircle(sketch, "E41.23.15.1", {"center": v(322, -210) * mm, "radius": 2.5 * mm});
            skCircle(sketch, "E41.23.16.0", {"center": v(315, -231) * mm, "radius": 2.5 * mm});
            skCircle(sketch, "E41.23.16.1", {"center": v(322, -224) * mm, "radius": 2.5 * mm});
            skCircle(sketch, "E41.23.17.0", {"center": v(315, -245) * mm, "radius": 2.5 * mm});
            skCircle(sketch, "E41.23.17.1", {"center": v(322, -238) * mm, "radius": 2.5 * mm});
            skCircle(sketch, "E41.23.18.0", {"center": v(315, -259) * mm, "radius": 2.5 * mm});
            skCircle(sketch, "E41.23.18.1", {"center": v(322, -252) * mm, "radius": 2.5 * mm});
            skCircle(sketch, "E41.23.19.0", {"center": v(315, -273) * mm, "radius": 2.5 * mm});
            skCircle(sketch, "E41.23.19.1", {"center": v(322, -266) * mm, "radius": 2.5 * mm});
            skCircle(sketch, "E41.24.0.0", {"center": v(329, -7) * mm, "radius": 2.5 * mm});
            skCircle(sketch, "E41.24.0.1", {"center": v(336, 0) * mm, "radius": 2.5 * mm});
            skCircle(sketch, "E41.24.1.0", {"center": v(329, -21) * mm, "radius": 2.5 * mm});
            skCircle(sketch, "E41.24.1.1", {"center": v(336, -14) * mm, "radius": 2.5 * mm});
            skCircle(sketch, "E41.24.2.0", {"center": v(329, -35) * mm, "radius": 2.5 * mm});
            skCircle(sketch, "E41.24.2.1", {"center": v(336, -28) * mm, "radius": 2.5 * mm});
            skCircle(sketch, "E41.24.3.0", {"center": v(329, -49) * mm, "radius": 2.5 * mm});
            skCircle(sketch, "E41.24.3.1", {"center": v(336, -42) * mm, "radius": 2.5 * mm});
            skCircle(sketch, "E41.24.4.0", {"center": v(329, -63) * mm, "radius": 2.5 * mm});
            skCircle(sketch, "E41.24.4.1", {"center": v(336, -56) * mm, "radius": 2.5 * mm});
            skCircle(sketch, "E41.24.5.0", {"center": v(329, -77) * mm, "radius": 2.5 * mm});
            skCircle(sketch, "E41.24.5.1", {"center": v(336, -70) * mm, "radius": 2.5 * mm});
            skCircle(sketch, "E41.24.6.0", {"center": v(329, -91) * mm, "radius": 2.5 * mm});
            skCircle(sketch, "E41.24.6.1", {"center": v(336, -84) * mm, "radius": 2.5 * mm});
            skCircle(sketch, "E41.24.7.0", {"center": v(329, -105) * mm, "radius": 2.5 * mm});
            skCircle(sketch, "E41.24.7.1", {"center": v(336, -98) * mm, "radius": 2.5 * mm});
            skCircle(sketch, "E41.24.8.0", {"center": v(329, -119) * mm, "radius": 2.5 * mm});
            skCircle(sketch, "E41.24.8.1", {"center": v(336, -112) * mm, "radius": 2.5 * mm});
            skCircle(sketch, "E41.24.9.0", {"center": v(329, -133) * mm, "radius": 2.5 * mm});
            skCircle(sketch, "E41.24.9.1", {"center": v(336, -126) * mm, "radius": 2.5 * mm});
            skCircle(sketch, "E41.24.10.0", {"center": v(329, -147) * mm, "radius": 2.5 * mm});
            skCircle(sketch, "E41.24.10.1", {"center": v(336, -140) * mm, "radius": 2.5 * mm});
            skCircle(sketch, "E41.24.11.0", {"center": v(329, -161) * mm, "radius": 2.5 * mm});
            skCircle(sketch, "E41.24.11.1", {"center": v(336, -154) * mm, "radius": 2.5 * mm});
            skCircle(sketch, "E41.24.12.0", {"center": v(329, -175) * mm, "radius": 2.5 * mm});
            skCircle(sketch, "E41.24.12.1", {"center": v(336, -168) * mm, "radius": 2.5 * mm});
            skCircle(sketch, "E41.24.13.0", {"center": v(329, -189) * mm, "radius": 2.5 * mm});
            skCircle(sketch, "E41.24.13.1", {"center": v(336, -182) * mm, "radius": 2.5 * mm});
            skCircle(sketch, "E41.24.14.0", {"center": v(329, -203) * mm, "radius": 2.5 * mm});
            skCircle(sketch, "E41.24.14.1", {"center": v(336, -196) * mm, "radius": 2.5 * mm});
            skCircle(sketch, "E41.24.15.0", {"center": v(329, -217) * mm, "radius": 2.5 * mm});
            skCircle(sketch, "E41.24.15.1", {"center": v(336, -210) * mm, "radius": 2.5 * mm});
            skCircle(sketch, "E41.24.16.0", {"center": v(329, -231) * mm, "radius": 2.5 * mm});
            skCircle(sketch, "E41.24.16.1", {"center": v(336, -224) * mm, "radius": 2.5 * mm});
            skCircle(sketch, "E41.24.17.0", {"center": v(329, -245) * mm, "radius": 2.5 * mm});
            skCircle(sketch, "E41.24.17.1", {"center": v(336, -238) * mm, "radius": 2.5 * mm});
            skCircle(sketch, "E41.24.18.0", {"center": v(329, -259) * mm, "radius": 2.5 * mm});
            skCircle(sketch, "E41.24.18.1", {"center": v(336, -252) * mm, "radius": 2.5 * mm});
            skCircle(sketch, "E41.24.19.0", {"center": v(329, -273) * mm, "radius": 2.5 * mm});
            skCircle(sketch, "E41.24.19.1", {"center": v(336, -266) * mm, "radius": 2.5 * mm});
            skCircle(sketch, "E41.25.0.0", {"center": v(343, -7) * mm, "radius": 2.5 * mm});
            skCircle(sketch, "E41.25.0.1", {"center": v(350, 0) * mm, "radius": 2.5 * mm});
            skCircle(sketch, "E41.25.1.0", {"center": v(343, -21) * mm, "radius": 2.5 * mm});
            skCircle(sketch, "E41.25.1.1", {"center": v(350, -14) * mm, "radius": 2.5 * mm});
            skCircle(sketch, "E41.25.2.0", {"center": v(343, -35) * mm, "radius": 2.5 * mm});
            skCircle(sketch, "E41.25.2.1", {"center": v(350, -28) * mm, "radius": 2.5 * mm});
            skCircle(sketch, "E41.25.3.0", {"center": v(343, -49) * mm, "radius": 2.5 * mm});
            skCircle(sketch, "E41.25.3.1", {"center": v(350, -42) * mm, "radius": 2.5 * mm});
            skCircle(sketch, "E41.25.4.0", {"center": v(343, -63) * mm, "radius": 2.5 * mm});
            skCircle(sketch, "E41.25.4.1", {"center": v(350, -56) * mm, "radius": 2.5 * mm});
            skCircle(sketch, "E41.25.5.0", {"center": v(343, -77) * mm, "radius": 2.5 * mm});
            skCircle(sketch, "E41.25.5.1", {"center": v(350, -70) * mm, "radius": 2.5 * mm});
            skCircle(sketch, "E41.25.6.0", {"center": v(343, -91) * mm, "radius": 2.5 * mm});
            skCircle(sketch, "E41.25.6.1", {"center": v(350, -84) * mm, "radius": 2.5 * mm});
            skCircle(sketch, "E41.25.7.0", {"center": v(343, -105) * mm, "radius": 2.5 * mm});
            skCircle(sketch, "E41.25.7.1", {"center": v(350, -98) * mm, "radius": 2.5 * mm});
            skCircle(sketch, "E41.25.8.0", {"center": v(343, -119) * mm, "radius": 2.5 * mm});
            skCircle(sketch, "E41.25.8.1", {"center": v(350, -112) * mm, "radius": 2.5 * mm});
            skCircle(sketch, "E41.25.9.0", {"center": v(343, -133) * mm, "radius": 2.5 * mm});
            skCircle(sketch, "E41.25.9.1", {"center": v(350, -126) * mm, "radius": 2.5 * mm});
            skCircle(sketch, "E41.25.10.0", {"center": v(343, -147) * mm, "radius": 2.5 * mm});
            skCircle(sketch, "E41.25.10.1", {"center": v(350, -140) * mm, "radius": 2.5 * mm});
            skCircle(sketch, "E41.25.11.0", {"center": v(343, -161) * mm, "radius": 2.5 * mm});
            skCircle(sketch, "E41.25.11.1", {"center": v(350, -154) * mm, "radius": 2.5 * mm});
            skCircle(sketch, "E41.25.12.0", {"center": v(343, -175) * mm, "radius": 2.5 * mm});
            skCircle(sketch, "E41.25.12.1", {"center": v(350, -168) * mm, "radius": 2.5 * mm});
            skCircle(sketch, "E41.25.13.0", {"center": v(343, -189) * mm, "radius": 2.5 * mm});
            skCircle(sketch, "E41.25.13.1", {"center": v(350, -182) * mm, "radius": 2.5 * mm});
            skCircle(sketch, "E41.25.14.0", {"center": v(343, -203) * mm, "radius": 2.5 * mm});
            skCircle(sketch, "E41.25.14.1", {"center": v(350, -196) * mm, "radius": 2.5 * mm});
            skCircle(sketch, "E41.25.15.0", {"center": v(343, -217) * mm, "radius": 2.5 * mm});
            skCircle(sketch, "E41.25.15.1", {"center": v(350, -210) * mm, "radius": 2.5 * mm});
            skCircle(sketch, "E41.25.16.0", {"center": v(343, -231) * mm, "radius": 2.5 * mm});
            skCircle(sketch, "E41.25.16.1", {"center": v(350, -224) * mm, "radius": 2.5 * mm});
            skCircle(sketch, "E41.25.17.0", {"center": v(343, -245) * mm, "radius": 2.5 * mm});
            skCircle(sketch, "E41.25.17.1", {"center": v(350, -238) * mm, "radius": 2.5 * mm});
            skCircle(sketch, "E41.25.18.0", {"center": v(343, -259) * mm, "radius": 2.5 * mm});
            skCircle(sketch, "E41.25.18.1", {"center": v(350, -252) * mm, "radius": 2.5 * mm});
            skCircle(sketch, "E41.25.19.0", {"center": v(343, -273) * mm, "radius": 2.5 * mm});
            skCircle(sketch, "E41.25.19.1", {"center": v(350, -266) * mm, "radius": 2.5 * mm});
            skCircle(sketch, "E41.26.0.0", {"center": v(357, -7) * mm, "radius": 2.5 * mm});
            skCircle(sketch, "E41.26.0.1", {"center": v(364, 0) * mm, "radius": 2.5 * mm});
            skCircle(sketch, "E41.26.1.0", {"center": v(357, -21) * mm, "radius": 2.5 * mm});
            skCircle(sketch, "E41.26.1.1", {"center": v(364, -14) * mm, "radius": 2.5 * mm});
            skCircle(sketch, "E41.26.2.0", {"center": v(357, -35) * mm, "radius": 2.5 * mm});
            skCircle(sketch, "E41.26.2.1", {"center": v(364, -28) * mm, "radius": 2.5 * mm});
            skCircle(sketch, "E41.26.3.0", {"center": v(357, -49) * mm, "radius": 2.5 * mm});
            skCircle(sketch, "E41.26.3.1", {"center": v(364, -42) * mm, "radius": 2.5 * mm});
            skCircle(sketch, "E41.26.4.0", {"center": v(357, -63) * mm, "radius": 2.5 * mm});
            skCircle(sketch, "E41.26.4.1", {"center": v(364, -56) * mm, "radius": 2.5 * mm});
            skCircle(sketch, "E41.26.5.0", {"center": v(357, -77) * mm, "radius": 2.5 * mm});
            skCircle(sketch, "E41.26.5.1", {"center": v(364, -70) * mm, "radius": 2.5 * mm});
            skCircle(sketch, "E41.26.6.0", {"center": v(357, -91) * mm, "radius": 2.5 * mm});
            skCircle(sketch, "E41.26.6.1", {"center": v(364, -84) * mm, "radius": 2.5 * mm});
            skCircle(sketch, "E41.26.7.0", {"center": v(357, -105) * mm, "radius": 2.5 * mm});
            skCircle(sketch, "E41.26.7.1", {"center": v(364, -98) * mm, "radius": 2.5 * mm});
            skCircle(sketch, "E41.26.8.0", {"center": v(357, -119) * mm, "radius": 2.5 * mm});
            skCircle(sketch, "E41.26.8.1", {"center": v(364, -112) * mm, "radius": 2.5 * mm});
            skCircle(sketch, "E41.26.9.0", {"center": v(357, -133) * mm, "radius": 2.5 * mm});
            skCircle(sketch, "E41.26.9.1", {"center": v(364, -126) * mm, "radius": 2.5 * mm});
            skCircle(sketch, "E41.26.10.0", {"center": v(357, -147) * mm, "radius": 2.5 * mm});
            skCircle(sketch, "E41.26.10.1", {"center": v(364, -140) * mm, "radius": 2.5 * mm});
            skCircle(sketch, "E41.26.11.0", {"center": v(357, -161) * mm, "radius": 2.5 * mm});
            skCircle(sketch, "E41.26.11.1", {"center": v(364, -154) * mm, "radius": 2.5 * mm});
            skCircle(sketch, "E41.26.12.0", {"center": v(357, -175) * mm, "radius": 2.5 * mm});
            skCircle(sketch, "E41.26.12.1", {"center": v(364, -168) * mm, "radius": 2.5 * mm});
            skCircle(sketch, "E41.26.13.0", {"center": v(357, -189) * mm, "radius": 2.5 * mm});
            skCircle(sketch, "E41.26.13.1", {"center": v(364, -182) * mm, "radius": 2.5 * mm});
            skCircle(sketch, "E41.26.14.0", {"center": v(357, -203) * mm, "radius": 2.5 * mm});
            skCircle(sketch, "E41.26.14.1", {"center": v(364, -196) * mm, "radius": 2.5 * mm});
            skCircle(sketch, "E41.26.15.0", {"center": v(357, -217) * mm, "radius": 2.5 * mm});
            skCircle(sketch, "E41.26.15.1", {"center": v(364, -210) * mm, "radius": 2.5 * mm});
            skCircle(sketch, "E41.26.16.0", {"center": v(357, -231) * mm, "radius": 2.5 * mm});
            skCircle(sketch, "E41.26.16.1", {"center": v(364, -224) * mm, "radius": 2.5 * mm});
            skCircle(sketch, "E41.26.17.0", {"center": v(357, -245) * mm, "radius": 2.5 * mm});
            skCircle(sketch, "E41.26.17.1", {"center": v(364, -238) * mm, "radius": 2.5 * mm});
            skCircle(sketch, "E41.26.18.0", {"center": v(357, -259) * mm, "radius": 2.5 * mm});
            skCircle(sketch, "E41.26.18.1", {"center": v(364, -252) * mm, "radius": 2.5 * mm});
            skCircle(sketch, "E41.26.19.0", {"center": v(357, -273) * mm, "radius": 2.5 * mm});
            skCircle(sketch, "E41.26.19.1", {"center": v(364, -266) * mm, "radius": 2.5 * mm});
            skCircle(sketch, "E41.27.0.0", {"center": v(371, -7) * mm, "radius": 2.5 * mm});
            skCircle(sketch, "E41.27.0.1", {"center": v(378, 0) * mm, "radius": 2.5 * mm});
            skCircle(sketch, "E41.27.1.0", {"center": v(371, -21) * mm, "radius": 2.5 * mm});
            skCircle(sketch, "E41.27.1.1", {"center": v(378, -14) * mm, "radius": 2.5 * mm});
            skCircle(sketch, "E41.27.2.0", {"center": v(371, -35) * mm, "radius": 2.5 * mm});
            skCircle(sketch, "E41.27.2.1", {"center": v(378, -28) * mm, "radius": 2.5 * mm});
            skCircle(sketch, "E41.27.3.0", {"center": v(371, -49) * mm, "radius": 2.5 * mm});
            skCircle(sketch, "E41.27.3.1", {"center": v(378, -42) * mm, "radius": 2.5 * mm});
            skCircle(sketch, "E41.27.4.0", {"center": v(371, -63) * mm, "radius": 2.5 * mm});
            skCircle(sketch, "E41.27.4.1", {"center": v(378, -56) * mm, "radius": 2.5 * mm});
            skCircle(sketch, "E41.27.5.0", {"center": v(371, -77) * mm, "radius": 2.5 * mm});
            skCircle(sketch, "E41.27.5.1", {"center": v(378, -70) * mm, "radius": 2.5 * mm});
            skCircle(sketch, "E41.27.6.0", {"center": v(371, -91) * mm, "radius": 2.5 * mm});
            skCircle(sketch, "E41.27.6.1", {"center": v(378, -84) * mm, "radius": 2.5 * mm});
            skCircle(sketch, "E41.27.7.0", {"center": v(371, -105) * mm, "radius": 2.5 * mm});
            skCircle(sketch, "E41.27.7.1", {"center": v(378, -98) * mm, "radius": 2.5 * mm});
            skCircle(sketch, "E41.27.8.0", {"center": v(371, -119) * mm, "radius": 2.5 * mm});
            skCircle(sketch, "E41.27.8.1", {"center": v(378, -112) * mm, "radius": 2.5 * mm});
            skCircle(sketch, "E41.27.9.0", {"center": v(371, -133) * mm, "radius": 2.5 * mm});
            skCircle(sketch, "E41.27.9.1", {"center": v(378, -126) * mm, "radius": 2.5 * mm});
            skCircle(sketch, "E41.27.10.0", {"center": v(371, -147) * mm, "radius": 2.5 * mm});
            skCircle(sketch, "E41.27.10.1", {"center": v(378, -140) * mm, "radius": 2.5 * mm});
            skCircle(sketch, "E41.27.11.0", {"center": v(371, -161) * mm, "radius": 2.5 * mm});
            skCircle(sketch, "E41.27.11.1", {"center": v(378, -154) * mm, "radius": 2.5 * mm});
            skCircle(sketch, "E41.27.12.0", {"center": v(371, -175) * mm, "radius": 2.5 * mm});
            skCircle(sketch, "E41.27.12.1", {"center": v(378, -168) * mm, "radius": 2.5 * mm});
            skCircle(sketch, "E41.27.13.0", {"center": v(371, -189) * mm, "radius": 2.5 * mm});
            skCircle(sketch, "E41.27.13.1", {"center": v(378, -182) * mm, "radius": 2.5 * mm});
            skCircle(sketch, "E41.27.14.0", {"center": v(371, -203) * mm, "radius": 2.5 * mm});
            skCircle(sketch, "E41.27.14.1", {"center": v(378, -196) * mm, "radius": 2.5 * mm});
            skCircle(sketch, "E41.27.15.0", {"center": v(371, -217) * mm, "radius": 2.5 * mm});
            skCircle(sketch, "E41.27.15.1", {"center": v(378, -210) * mm, "radius": 2.5 * mm});
            skCircle(sketch, "E41.27.16.0", {"center": v(371, -231) * mm, "radius": 2.5 * mm});
            skCircle(sketch, "E41.27.16.1", {"center": v(378, -224) * mm, "radius": 2.5 * mm});
            skCircle(sketch, "E41.27.17.0", {"center": v(371, -245) * mm, "radius": 2.5 * mm});
            skCircle(sketch, "E41.27.17.1", {"center": v(378, -238) * mm, "radius": 2.5 * mm});
            skCircle(sketch, "E41.27.18.0", {"center": v(371, -259) * mm, "radius": 2.5 * mm});
            skCircle(sketch, "E41.27.18.1", {"center": v(378, -252) * mm, "radius": 2.5 * mm});
            skCircle(sketch, "E41.27.19.0", {"center": v(371, -273) * mm, "radius": 2.5 * mm});
            skCircle(sketch, "E41.27.19.1", {"center": v(378, -266) * mm, "radius": 2.5 * mm});
            skCircle(sketch, "E41.28.0.0", {"center": v(385, -7) * mm, "radius": 2.5 * mm});
            skCircle(sketch, "E41.28.0.1", {"center": v(392, 0) * mm, "radius": 2.5 * mm});
            skCircle(sketch, "E41.28.1.0", {"center": v(385, -21) * mm, "radius": 2.5 * mm});
            skCircle(sketch, "E41.28.1.1", {"center": v(392, -14) * mm, "radius": 2.5 * mm});
            skCircle(sketch, "E41.28.2.0", {"center": v(385, -35) * mm, "radius": 2.5 * mm});
            skCircle(sketch, "E41.28.2.1", {"center": v(392, -28) * mm, "radius": 2.5 * mm});
            skCircle(sketch, "E41.28.3.0", {"center": v(385, -49) * mm, "radius": 2.5 * mm});
            skCircle(sketch, "E41.28.3.1", {"center": v(392, -42) * mm, "radius": 2.5 * mm});
            skCircle(sketch, "E41.28.4.0", {"center": v(385, -63) * mm, "radius": 2.5 * mm});
            skCircle(sketch, "E41.28.4.1", {"center": v(392, -56) * mm, "radius": 2.5 * mm});
            skCircle(sketch, "E41.28.5.0", {"center": v(385, -77) * mm, "radius": 2.5 * mm});
            skCircle(sketch, "E41.28.5.1", {"center": v(392, -70) * mm, "radius": 2.5 * mm});
            skCircle(sketch, "E41.28.6.0", {"center": v(385, -91) * mm, "radius": 2.5 * mm});
            skCircle(sketch, "E41.28.6.1", {"center": v(392, -84) * mm, "radius": 2.5 * mm});
            skCircle(sketch, "E41.28.7.0", {"center": v(385, -105) * mm, "radius": 2.5 * mm});
            skCircle(sketch, "E41.28.7.1", {"center": v(392, -98) * mm, "radius": 2.5 * mm});
            skCircle(sketch, "E41.28.8.0", {"center": v(385, -119) * mm, "radius": 2.5 * mm});
            skCircle(sketch, "E41.28.8.1", {"center": v(392, -112) * mm, "radius": 2.5 * mm});
            skCircle(sketch, "E41.28.9.0", {"center": v(385, -133) * mm, "radius": 2.5 * mm});
            skCircle(sketch, "E41.28.9.1", {"center": v(392, -126) * mm, "radius": 2.5 * mm});
            skCircle(sketch, "E41.28.10.0", {"center": v(385, -147) * mm, "radius": 2.5 * mm});
            skCircle(sketch, "E41.28.10.1", {"center": v(392, -140) * mm, "radius": 2.5 * mm});
            skCircle(sketch, "E41.28.11.0", {"center": v(385, -161) * mm, "radius": 2.5 * mm});
            skCircle(sketch, "E41.28.11.1", {"center": v(392, -154) * mm, "radius": 2.5 * mm});
            skCircle(sketch, "E41.28.12.0", {"center": v(385, -175) * mm, "radius": 2.5 * mm});
            skCircle(sketch, "E41.28.12.1", {"center": v(392, -168) * mm, "radius": 2.5 * mm});
            skCircle(sketch, "E41.28.13.0", {"center": v(385, -189) * mm, "radius": 2.5 * mm});
            skCircle(sketch, "E41.28.13.1", {"center": v(392, -182) * mm, "radius": 2.5 * mm});
            skCircle(sketch, "E41.28.14.0", {"center": v(385, -203) * mm, "radius": 2.5 * mm});
            skCircle(sketch, "E41.28.14.1", {"center": v(392, -196) * mm, "radius": 2.5 * mm});
            skCircle(sketch, "E41.28.15.0", {"center": v(385, -217) * mm, "radius": 2.5 * mm});
            skCircle(sketch, "E41.28.15.1", {"center": v(392, -210) * mm, "radius": 2.5 * mm});
            skCircle(sketch, "E41.28.16.0", {"center": v(385, -231) * mm, "radius": 2.5 * mm});
            skCircle(sketch, "E41.28.16.1", {"center": v(392, -224) * mm, "radius": 2.5 * mm});
            skCircle(sketch, "E41.28.17.0", {"center": v(385, -245) * mm, "radius": 2.5 * mm});
            skCircle(sketch, "E41.28.17.1", {"center": v(392, -238) * mm, "radius": 2.5 * mm});
            skCircle(sketch, "E41.28.18.0", {"center": v(385, -259) * mm, "radius": 2.5 * mm});
            skCircle(sketch, "E41.28.18.1", {"center": v(392, -252) * mm, "radius": 2.5 * mm});
            skCircle(sketch, "E41.28.19.0", {"center": v(385, -273) * mm, "radius": 2.5 * mm});
            skCircle(sketch, "E41.28.19.1", {"center": v(392, -266) * mm, "radius": 2.5 * mm});
            skCircle(sketch, "E41.29.0.0", {"center": v(399, -7) * mm, "radius": 2.5 * mm});
            skCircle(sketch, "E41.29.0.1", {"center": v(406, 0) * mm, "radius": 2.5 * mm});
            skCircle(sketch, "E41.29.1.0", {"center": v(399, -21) * mm, "radius": 2.5 * mm});
            skCircle(sketch, "E41.29.1.1", {"center": v(406, -14) * mm, "radius": 2.5 * mm});
            skCircle(sketch, "E41.29.2.0", {"center": v(399, -35) * mm, "radius": 2.5 * mm});
            skCircle(sketch, "E41.29.2.1", {"center": v(406, -28) * mm, "radius": 2.5 * mm});
            skCircle(sketch, "E41.29.3.0", {"center": v(399, -49) * mm, "radius": 2.5 * mm});
            skCircle(sketch, "E41.29.3.1", {"center": v(406, -42) * mm, "radius": 2.5 * mm});
            skCircle(sketch, "E41.29.4.0", {"center": v(399, -63) * mm, "radius": 2.5 * mm});
            skCircle(sketch, "E41.29.4.1", {"center": v(406, -56) * mm, "radius": 2.5 * mm});
            skCircle(sketch, "E41.29.5.0", {"center": v(399, -77) * mm, "radius": 2.5 * mm});
            skCircle(sketch, "E41.29.5.1", {"center": v(406, -70) * mm, "radius": 2.5 * mm});
            skCircle(sketch, "E41.29.6.0", {"center": v(399, -91) * mm, "radius": 2.5 * mm});
            skCircle(sketch, "E41.29.6.1", {"center": v(406, -84) * mm, "radius": 2.5 * mm});
            skCircle(sketch, "E41.29.7.0", {"center": v(399, -105) * mm, "radius": 2.5 * mm});
            skCircle(sketch, "E41.29.7.1", {"center": v(406, -98) * mm, "radius": 2.5 * mm});
            skCircle(sketch, "E41.29.8.0", {"center": v(399, -119) * mm, "radius": 2.5 * mm});
            skCircle(sketch, "E41.29.8.1", {"center": v(406, -112) * mm, "radius": 2.5 * mm});
            skCircle(sketch, "E41.29.9.0", {"center": v(399, -133) * mm, "radius": 2.5 * mm});
            skCircle(sketch, "E41.29.9.1", {"center": v(406, -126) * mm, "radius": 2.5 * mm});
            skCircle(sketch, "E41.29.10.0", {"center": v(399, -147) * mm, "radius": 2.5 * mm});
            skCircle(sketch, "E41.29.10.1", {"center": v(406, -140) * mm, "radius": 2.5 * mm});
            skCircle(sketch, "E41.29.11.0", {"center": v(399, -161) * mm, "radius": 2.5 * mm});
            skCircle(sketch, "E41.29.11.1", {"center": v(406, -154) * mm, "radius": 2.5 * mm});
            skCircle(sketch, "E41.29.12.0", {"center": v(399, -175) * mm, "radius": 2.5 * mm});
            skCircle(sketch, "E41.29.12.1", {"center": v(406, -168) * mm, "radius": 2.5 * mm});
            skCircle(sketch, "E41.29.13.0", {"center": v(399, -189) * mm, "radius": 2.5 * mm});
            skCircle(sketch, "E41.29.13.1", {"center": v(406, -182) * mm, "radius": 2.5 * mm});
            skCircle(sketch, "E41.29.14.0", {"center": v(399, -203) * mm, "radius": 2.5 * mm});
            skCircle(sketch, "E41.29.14.1", {"center": v(406, -196) * mm, "radius": 2.5 * mm});
            skCircle(sketch, "E41.29.15.0", {"center": v(399, -217) * mm, "radius": 2.5 * mm});
            skCircle(sketch, "E41.29.15.1", {"center": v(406, -210) * mm, "radius": 2.5 * mm});
            skCircle(sketch, "E41.29.16.0", {"center": v(399, -231) * mm, "radius": 2.5 * mm});
            skCircle(sketch, "E41.29.16.1", {"center": v(406, -224) * mm, "radius": 2.5 * mm});
            skCircle(sketch, "E41.29.17.0", {"center": v(399, -245) * mm, "radius": 2.5 * mm});
            skCircle(sketch, "E41.29.17.1", {"center": v(406, -238) * mm, "radius": 2.5 * mm});
            skCircle(sketch, "E41.29.18.0", {"center": v(399, -259) * mm, "radius": 2.5 * mm});
            skCircle(sketch, "E41.29.18.1", {"center": v(406, -252) * mm, "radius": 2.5 * mm});
            skCircle(sketch, "E41.29.19.0", {"center": v(399, -273) * mm, "radius": 2.5 * mm});
            skCircle(sketch, "E41.29.19.1", {"center": v(406, -266) * mm, "radius": 2.5 * mm});
            skCircle(sketch, "E41.30.0.0", {"center": v(413, -7) * mm, "radius": 2.5 * mm});
            skCircle(sketch, "E41.30.0.1", {"center": v(420, 0) * mm, "radius": 2.5 * mm});
            skCircle(sketch, "E41.30.1.0", {"center": v(413, -21) * mm, "radius": 2.5 * mm});
            skCircle(sketch, "E41.30.1.1", {"center": v(420, -14) * mm, "radius": 2.5 * mm});
            skCircle(sketch, "E41.30.2.0", {"center": v(413, -35) * mm, "radius": 2.5 * mm});
            skCircle(sketch, "E41.30.2.1", {"center": v(420, -28) * mm, "radius": 2.5 * mm});
            skCircle(sketch, "E41.30.3.0", {"center": v(413, -49) * mm, "radius": 2.5 * mm});
            skCircle(sketch, "E41.30.3.1", {"center": v(420, -42) * mm, "radius": 2.5 * mm});
            skCircle(sketch, "E41.30.4.0", {"center": v(413, -63) * mm, "radius": 2.5 * mm});
            skCircle(sketch, "E41.30.4.1", {"center": v(420, -56) * mm, "radius": 2.5 * mm});
            skCircle(sketch, "E41.30.5.0", {"center": v(413, -77) * mm, "radius": 2.5 * mm});
            skCircle(sketch, "E41.30.5.1", {"center": v(420, -70) * mm, "radius": 2.5 * mm});
            skCircle(sketch, "E41.30.6.0", {"center": v(413, -91) * mm, "radius": 2.5 * mm});
            skCircle(sketch, "E41.30.6.1", {"center": v(420, -84) * mm, "radius": 2.5 * mm});
            skCircle(sketch, "E41.30.7.0", {"center": v(413, -105) * mm, "radius": 2.5 * mm});
            skCircle(sketch, "E41.30.7.1", {"center": v(420, -98) * mm, "radius": 2.5 * mm});
            skCircle(sketch, "E41.30.8.0", {"center": v(413, -119) * mm, "radius": 2.5 * mm});
            skCircle(sketch, "E41.30.8.1", {"center": v(420, -112) * mm, "radius": 2.5 * mm});
            skCircle(sketch, "E41.30.9.0", {"center": v(413, -133) * mm, "radius": 2.5 * mm});
            skCircle(sketch, "E41.30.9.1", {"center": v(420, -126) * mm, "radius": 2.5 * mm});
            skCircle(sketch, "E41.30.10.0", {"center": v(413, -147) * mm, "radius": 2.5 * mm});
            skCircle(sketch, "E41.30.10.1", {"center": v(420, -140) * mm, "radius": 2.5 * mm});
            skCircle(sketch, "E41.30.11.0", {"center": v(413, -161) * mm, "radius": 2.5 * mm});
            skCircle(sketch, "E41.30.11.1", {"center": v(420, -154) * mm, "radius": 2.5 * mm});
            skCircle(sketch, "E41.30.12.0", {"center": v(413, -175) * mm, "radius": 2.5 * mm});
            skCircle(sketch, "E41.30.12.1", {"center": v(420, -168) * mm, "radius": 2.5 * mm});
            skCircle(sketch, "E41.30.13.0", {"center": v(413, -189) * mm, "radius": 2.5 * mm});
            skCircle(sketch, "E41.30.13.1", {"center": v(420, -182) * mm, "radius": 2.5 * mm});
            skCircle(sketch, "E41.30.14.0", {"center": v(413, -203) * mm, "radius": 2.5 * mm});
            skCircle(sketch, "E41.30.14.1", {"center": v(420, -196) * mm, "radius": 2.5 * mm});
            skCircle(sketch, "E41.30.15.0", {"center": v(413, -217) * mm, "radius": 2.5 * mm});
            skCircle(sketch, "E41.30.15.1", {"center": v(420, -210) * mm, "radius": 2.5 * mm});
            skCircle(sketch, "E41.30.16.0", {"center": v(413, -231) * mm, "radius": 2.5 * mm});
            skCircle(sketch, "E41.30.16.1", {"center": v(420, -224) * mm, "radius": 2.5 * mm});
            skCircle(sketch, "E41.30.17.0", {"center": v(413, -245) * mm, "radius": 2.5 * mm});
            skCircle(sketch, "E41.30.17.1", {"center": v(420, -238) * mm, "radius": 2.5 * mm});
            skCircle(sketch, "E41.30.18.0", {"center": v(413, -259) * mm, "radius": 2.5 * mm});
            skCircle(sketch, "E41.30.18.1", {"center": v(420, -252) * mm, "radius": 2.5 * mm});
            skCircle(sketch, "E41.30.19.0", {"center": v(413, -273) * mm, "radius": 2.5 * mm});
            skCircle(sketch, "E41.30.19.1", {"center": v(420, -266) * mm, "radius": 2.5 * mm});
            skCircle(sketch, "E41.31.0.0", {"center": v(427, -7) * mm, "radius": 2.5 * mm});
            skCircle(sketch, "E41.31.0.1", {"center": v(434, 0) * mm, "radius": 2.5 * mm});
            skCircle(sketch, "E41.31.1.0", {"center": v(427, -21) * mm, "radius": 2.5 * mm});
            skCircle(sketch, "E41.31.1.1", {"center": v(434, -14) * mm, "radius": 2.5 * mm});
            skCircle(sketch, "E41.31.2.0", {"center": v(427, -35) * mm, "radius": 2.5 * mm});
            skCircle(sketch, "E41.31.2.1", {"center": v(434, -28) * mm, "radius": 2.5 * mm});
            skCircle(sketch, "E41.31.3.0", {"center": v(427, -49) * mm, "radius": 2.5 * mm});
            skCircle(sketch, "E41.31.3.1", {"center": v(434, -42) * mm, "radius": 2.5 * mm});
            skCircle(sketch, "E41.31.4.0", {"center": v(427, -63) * mm, "radius": 2.5 * mm});
            skCircle(sketch, "E41.31.4.1", {"center": v(434, -56) * mm, "radius": 2.5 * mm});
            skCircle(sketch, "E41.31.5.0", {"center": v(427, -77) * mm, "radius": 2.5 * mm});
            skCircle(sketch, "E41.31.5.1", {"center": v(434, -70) * mm, "radius": 2.5 * mm});
            skCircle(sketch, "E41.31.6.0", {"center": v(427, -91) * mm, "radius": 2.5 * mm});
            skCircle(sketch, "E41.31.6.1", {"center": v(434, -84) * mm, "radius": 2.5 * mm});
            skCircle(sketch, "E41.31.7.0", {"center": v(427, -105) * mm, "radius": 2.5 * mm});
            skCircle(sketch, "E41.31.7.1", {"center": v(434, -98) * mm, "radius": 2.5 * mm});
            skCircle(sketch, "E41.31.8.0", {"center": v(427, -119) * mm, "radius": 2.5 * mm});
            skCircle(sketch, "E41.31.8.1", {"center": v(434, -112) * mm, "radius": 2.5 * mm});
            skCircle(sketch, "E41.31.9.0", {"center": v(427, -133) * mm, "radius": 2.5 * mm});
            skCircle(sketch, "E41.31.9.1", {"center": v(434, -126) * mm, "radius": 2.5 * mm});
            skCircle(sketch, "E41.31.10.0", {"center": v(427, -147) * mm, "radius": 2.5 * mm});
            skCircle(sketch, "E41.31.10.1", {"center": v(434, -140) * mm, "radius": 2.5 * mm});
            skCircle(sketch, "E41.31.11.0", {"center": v(427, -161) * mm, "radius": 2.5 * mm});
            skCircle(sketch, "E41.31.11.1", {"center": v(434, -154) * mm, "radius": 2.5 * mm});
            skCircle(sketch, "E41.31.12.0", {"center": v(427, -175) * mm, "radius": 2.5 * mm});
            skCircle(sketch, "E41.31.12.1", {"center": v(434, -168) * mm, "radius": 2.5 * mm});
            skCircle(sketch, "E41.31.13.0", {"center": v(427, -189) * mm, "radius": 2.5 * mm});
            skCircle(sketch, "E41.31.13.1", {"center": v(434, -182) * mm, "radius": 2.5 * mm});
            skCircle(sketch, "E41.31.14.0", {"center": v(427, -203) * mm, "radius": 2.5 * mm});
            skCircle(sketch, "E41.31.14.1", {"center": v(434, -196) * mm, "radius": 2.5 * mm});
            skCircle(sketch, "E41.31.15.0", {"center": v(427, -217) * mm, "radius": 2.5 * mm});
            skCircle(sketch, "E41.31.15.1", {"center": v(434, -210) * mm, "radius": 2.5 * mm});
            skCircle(sketch, "E41.31.16.0", {"center": v(427, -231) * mm, "radius": 2.5 * mm});
            skCircle(sketch, "E41.31.16.1", {"center": v(434, -224) * mm, "radius": 2.5 * mm});
            skCircle(sketch, "E41.31.17.0", {"center": v(427, -245) * mm, "radius": 2.5 * mm});
            skCircle(sketch, "E41.31.17.1", {"center": v(434, -238) * mm, "radius": 2.5 * mm});
            skCircle(sketch, "E41.31.18.0", {"center": v(427, -259) * mm, "radius": 2.5 * mm});
            skCircle(sketch, "E41.31.18.1", {"center": v(434, -252) * mm, "radius": 2.5 * mm});
            skCircle(sketch, "E41.31.19.0", {"center": v(427, -273) * mm, "radius": 2.5 * mm});
            skCircle(sketch, "E41.31.19.1", {"center": v(434, -266) * mm, "radius": 2.5 * mm});
            skCircle(sketch, "E41.32.0.0", {"center": v(441, -7) * mm, "radius": 2.5 * mm});
            skCircle(sketch, "E41.32.0.1", {"center": v(448, 0) * mm, "radius": 2.5 * mm});
            skCircle(sketch, "E41.32.1.0", {"center": v(441, -21) * mm, "radius": 2.5 * mm});
            skCircle(sketch, "E41.32.1.1", {"center": v(448, -14) * mm, "radius": 2.5 * mm});
            skCircle(sketch, "E41.32.2.0", {"center": v(441, -35) * mm, "radius": 2.5 * mm});
            skCircle(sketch, "E41.32.2.1", {"center": v(448, -28) * mm, "radius": 2.5 * mm});
            skCircle(sketch, "E41.32.3.0", {"center": v(441, -49) * mm, "radius": 2.5 * mm});
            skCircle(sketch, "E41.32.3.1", {"center": v(448, -42) * mm, "radius": 2.5 * mm});
            skCircle(sketch, "E41.32.4.0", {"center": v(441, -63) * mm, "radius": 2.5 * mm});
            skCircle(sketch, "E41.32.4.1", {"center": v(448, -56) * mm, "radius": 2.5 * mm});
            skCircle(sketch, "E41.32.5.0", {"center": v(441, -77) * mm, "radius": 2.5 * mm});
            skCircle(sketch, "E41.32.5.1", {"center": v(448, -70) * mm, "radius": 2.5 * mm});
            skCircle(sketch, "E41.32.6.0", {"center": v(441, -91) * mm, "radius": 2.5 * mm});
            skCircle(sketch, "E41.32.6.1", {"center": v(448, -84) * mm, "radius": 2.5 * mm});
            skCircle(sketch, "E41.32.7.0", {"center": v(441, -105) * mm, "radius": 2.5 * mm});
            skCircle(sketch, "E41.32.7.1", {"center": v(448, -98) * mm, "radius": 2.5 * mm});
            skCircle(sketch, "E41.32.8.0", {"center": v(441, -119) * mm, "radius": 2.5 * mm});
            skCircle(sketch, "E41.32.8.1", {"center": v(448, -112) * mm, "radius": 2.5 * mm});
            skCircle(sketch, "E41.32.9.0", {"center": v(441, -133) * mm, "radius": 2.5 * mm});
            skCircle(sketch, "E41.32.9.1", {"center": v(448, -126) * mm, "radius": 2.5 * mm});
            skCircle(sketch, "E41.32.10.0", {"center": v(441, -147) * mm, "radius": 2.5 * mm});
            skCircle(sketch, "E41.32.10.1", {"center": v(448, -140) * mm, "radius": 2.5 * mm});
            skCircle(sketch, "E41.32.11.0", {"center": v(441, -161) * mm, "radius": 2.5 * mm});
            skCircle(sketch, "E41.32.11.1", {"center": v(448, -154) * mm, "radius": 2.5 * mm});
            skCircle(sketch, "E41.32.12.0", {"center": v(441, -175) * mm, "radius": 2.5 * mm});
            skCircle(sketch, "E41.32.12.1", {"center": v(448, -168) * mm, "radius": 2.5 * mm});
            skCircle(sketch, "E41.32.13.0", {"center": v(441, -189) * mm, "radius": 2.5 * mm});
            skCircle(sketch, "E41.32.13.1", {"center": v(448, -182) * mm, "radius": 2.5 * mm});
            skCircle(sketch, "E41.32.14.0", {"center": v(441, -203) * mm, "radius": 2.5 * mm});
            skCircle(sketch, "E41.32.14.1", {"center": v(448, -196) * mm, "radius": 2.5 * mm});
            skCircle(sketch, "E41.32.15.0", {"center": v(441, -217) * mm, "radius": 2.5 * mm});
            skCircle(sketch, "E41.32.15.1", {"center": v(448, -210) * mm, "radius": 2.5 * mm});
            skCircle(sketch, "E41.32.16.0", {"center": v(441, -231) * mm, "radius": 2.5 * mm});
            skCircle(sketch, "E41.32.16.1", {"center": v(448, -224) * mm, "radius": 2.5 * mm});
            skCircle(sketch, "E41.32.17.0", {"center": v(441, -245) * mm, "radius": 2.5 * mm});
            skCircle(sketch, "E41.32.17.1", {"center": v(448, -238) * mm, "radius": 2.5 * mm});
            skCircle(sketch, "E41.32.18.0", {"center": v(441, -259) * mm, "radius": 2.5 * mm});
            skCircle(sketch, "E41.32.18.1", {"center": v(448, -252) * mm, "radius": 2.5 * mm});
            skCircle(sketch, "E41.32.19.0", {"center": v(441, -273) * mm, "radius": 2.5 * mm});
            skCircle(sketch, "E41.32.19.1", {"center": v(448, -266) * mm, "radius": 2.5 * mm});
            skCircle(sketch, "E41.33.0.0", {"center": v(455, -7) * mm, "radius": 2.5 * mm});
            skCircle(sketch, "E41.33.0.1", {"center": v(462, 0) * mm, "radius": 2.5 * mm});
            skCircle(sketch, "E41.33.1.0", {"center": v(455, -21) * mm, "radius": 2.5 * mm});
            skCircle(sketch, "E41.33.1.1", {"center": v(462, -14) * mm, "radius": 2.5 * mm});
            skCircle(sketch, "E41.33.2.0", {"center": v(455, -35) * mm, "radius": 2.5 * mm});
            skCircle(sketch, "E41.33.2.1", {"center": v(462, -28) * mm, "radius": 2.5 * mm});
            skCircle(sketch, "E41.33.3.0", {"center": v(455, -49) * mm, "radius": 2.5 * mm});
            skCircle(sketch, "E41.33.3.1", {"center": v(462, -42) * mm, "radius": 2.5 * mm});
            skCircle(sketch, "E41.33.4.0", {"center": v(455, -63) * mm, "radius": 2.5 * mm});
            skCircle(sketch, "E41.33.4.1", {"center": v(462, -56) * mm, "radius": 2.5 * mm});
            skCircle(sketch, "E41.33.5.0", {"center": v(455, -77) * mm, "radius": 2.5 * mm});
            skCircle(sketch, "E41.33.5.1", {"center": v(462, -70) * mm, "radius": 2.5 * mm});
            skCircle(sketch, "E41.33.6.0", {"center": v(455, -91) * mm, "radius": 2.5 * mm});
            skCircle(sketch, "E41.33.6.1", {"center": v(462, -84) * mm, "radius": 2.5 * mm});
            skCircle(sketch, "E41.33.7.0", {"center": v(455, -105) * mm, "radius": 2.5 * mm});
            skCircle(sketch, "E41.33.7.1", {"center": v(462, -98) * mm, "radius": 2.5 * mm});
            skCircle(sketch, "E41.33.8.0", {"center": v(455, -119) * mm, "radius": 2.5 * mm});
            skCircle(sketch, "E41.33.8.1", {"center": v(462, -112) * mm, "radius": 2.5 * mm});
            skCircle(sketch, "E41.33.9.0", {"center": v(455, -133) * mm, "radius": 2.5 * mm});
            skCircle(sketch, "E41.33.9.1", {"center": v(462, -126) * mm, "radius": 2.5 * mm});
            skCircle(sketch, "E41.33.10.0", {"center": v(455, -147) * mm, "radius": 2.5 * mm});
            skCircle(sketch, "E41.33.10.1", {"center": v(462, -140) * mm, "radius": 2.5 * mm});
            skCircle(sketch, "E41.33.11.0", {"center": v(455, -161) * mm, "radius": 2.5 * mm});
            skCircle(sketch, "E41.33.11.1", {"center": v(462, -154) * mm, "radius": 2.5 * mm});
            skCircle(sketch, "E41.33.12.0", {"center": v(455, -175) * mm, "radius": 2.5 * mm});
            skCircle(sketch, "E41.33.12.1", {"center": v(462, -168) * mm, "radius": 2.5 * mm});
            skCircle(sketch, "E41.33.13.0", {"center": v(455, -189) * mm, "radius": 2.5 * mm});
            skCircle(sketch, "E41.33.13.1", {"center": v(462, -182) * mm, "radius": 2.5 * mm});
            skCircle(sketch, "E41.33.14.0", {"center": v(455, -203) * mm, "radius": 2.5 * mm});
            skCircle(sketch, "E41.33.14.1", {"center": v(462, -196) * mm, "radius": 2.5 * mm});
            skCircle(sketch, "E41.33.15.0", {"center": v(455, -217) * mm, "radius": 2.5 * mm});
            skCircle(sketch, "E41.33.15.1", {"center": v(462, -210) * mm, "radius": 2.5 * mm});
            skCircle(sketch, "E41.33.16.0", {"center": v(455, -231) * mm, "radius": 2.5 * mm});
            skCircle(sketch, "E41.33.16.1", {"center": v(462, -224) * mm, "radius": 2.5 * mm});
            skCircle(sketch, "E41.33.17.0", {"center": v(455, -245) * mm, "radius": 2.5 * mm});
            skCircle(sketch, "E41.33.17.1", {"center": v(462, -238) * mm, "radius": 2.5 * mm});
            skCircle(sketch, "E41.33.18.0", {"center": v(455, -259) * mm, "radius": 2.5 * mm});
            skCircle(sketch, "E41.33.18.1", {"center": v(462, -252) * mm, "radius": 2.5 * mm});
            skCircle(sketch, "E41.33.19.0", {"center": v(455, -273) * mm, "radius": 2.5 * mm});
            skCircle(sketch, "E41.33.19.1", {"center": v(462, -266) * mm, "radius": 2.5 * mm});
            skCircle(sketch, "E41.34.0.0", {"center": v(469, -7) * mm, "radius": 2.5 * mm});
            skCircle(sketch, "E41.34.0.1", {"center": v(476, 0) * mm, "radius": 2.5 * mm});
            skCircle(sketch, "E41.34.1.0", {"center": v(469, -21) * mm, "radius": 2.5 * mm});
            skCircle(sketch, "E41.34.1.1", {"center": v(476, -14) * mm, "radius": 2.5 * mm});
            skCircle(sketch, "E41.34.2.0", {"center": v(469, -35) * mm, "radius": 2.5 * mm});
            skCircle(sketch, "E41.34.2.1", {"center": v(476, -28) * mm, "radius": 2.5 * mm});
            skCircle(sketch, "E41.34.3.0", {"center": v(469, -49) * mm, "radius": 2.5 * mm});
            skCircle(sketch, "E41.34.3.1", {"center": v(476, -42) * mm, "radius": 2.5 * mm});
            skCircle(sketch, "E41.34.4.0", {"center": v(469, -63) * mm, "radius": 2.5 * mm});
            skCircle(sketch, "E41.34.4.1", {"center": v(476, -56) * mm, "radius": 2.5 * mm});
            skCircle(sketch, "E41.34.5.0", {"center": v(469, -77) * mm, "radius": 2.5 * mm});
            skCircle(sketch, "E41.34.5.1", {"center": v(476, -70) * mm, "radius": 2.5 * mm});
            skCircle(sketch, "E41.34.6.0", {"center": v(469, -91) * mm, "radius": 2.5 * mm});
            skCircle(sketch, "E41.34.6.1", {"center": v(476, -84) * mm, "radius": 2.5 * mm});
            skCircle(sketch, "E41.34.7.0", {"center": v(469, -105) * mm, "radius": 2.5 * mm});
            skCircle(sketch, "E41.34.7.1", {"center": v(476, -98) * mm, "radius": 2.5 * mm});
            skCircle(sketch, "E41.34.8.0", {"center": v(469, -119) * mm, "radius": 2.5 * mm});
            skCircle(sketch, "E41.34.8.1", {"center": v(476, -112) * mm, "radius": 2.5 * mm});
            skCircle(sketch, "E41.34.9.0", {"center": v(469, -133) * mm, "radius": 2.5 * mm});
            skCircle(sketch, "E41.34.9.1", {"center": v(476, -126) * mm, "radius": 2.5 * mm});
            skCircle(sketch, "E41.34.10.0", {"center": v(469, -147) * mm, "radius": 2.5 * mm});
            skCircle(sketch, "E41.34.10.1", {"center": v(476, -140) * mm, "radius": 2.5 * mm});
            skCircle(sketch, "E41.34.11.0", {"center": v(469, -161) * mm, "radius": 2.5 * mm});
            skCircle(sketch, "E41.34.11.1", {"center": v(476, -154) * mm, "radius": 2.5 * mm});
            skCircle(sketch, "E41.34.12.0", {"center": v(469, -175) * mm, "radius": 2.5 * mm});
            skCircle(sketch, "E41.34.12.1", {"center": v(476, -168) * mm, "radius": 2.5 * mm});
            skCircle(sketch, "E41.34.13.0", {"center": v(469, -189) * mm, "radius": 2.5 * mm});
            skCircle(sketch, "E41.34.13.1", {"center": v(476, -182) * mm, "radius": 2.5 * mm});
            skCircle(sketch, "E41.34.14.0", {"center": v(469, -203) * mm, "radius": 2.5 * mm});
            skCircle(sketch, "E41.34.14.1", {"center": v(476, -196) * mm, "radius": 2.5 * mm});
            skCircle(sketch, "E41.34.15.0", {"center": v(469, -217) * mm, "radius": 2.5 * mm});
            skCircle(sketch, "E41.34.15.1", {"center": v(476, -210) * mm, "radius": 2.5 * mm});
            skCircle(sketch, "E41.34.16.0", {"center": v(469, -231) * mm, "radius": 2.5 * mm});
            skCircle(sketch, "E41.34.16.1", {"center": v(476, -224) * mm, "radius": 2.5 * mm});
            skCircle(sketch, "E41.34.17.0", {"center": v(469, -245) * mm, "radius": 2.5 * mm});
            skCircle(sketch, "E41.34.17.1", {"center": v(476, -238) * mm, "radius": 2.5 * mm});
            skCircle(sketch, "E41.34.18.0", {"center": v(469, -259) * mm, "radius": 2.5 * mm});
            skCircle(sketch, "E41.34.18.1", {"center": v(476, -252) * mm, "radius": 2.5 * mm});
            skCircle(sketch, "E41.34.19.0", {"center": v(469, -273) * mm, "radius": 2.5 * mm});
            skCircle(sketch, "E41.34.19.1", {"center": v(476, -266) * mm, "radius": 2.5 * mm});
            skLineSegment(sketch, "E41.direction1", {"start": v(-7, -7) * mm, "end": v(7, -7) * mm, "construction": true});
            skLineSegment(sketch, "E41.direction2", {"start": v(-7, -7) * mm, "end": v(-7, -21) * mm, "construction": true});
            skCircle(sketch, "E42.0.0.20", {"center": v(-7, -287) * mm, "radius": 2.5 * mm});
            skCircle(sketch, "E42.2.0.20", {"center": v(0, -280) * mm, "radius": 2.5 * mm});
            skCircle(sketch, "E42.0.0.21", {"center": v(-7, -301) * mm, "radius": 2.5 * mm});
            skCircle(sketch, "E42.2.0.21", {"center": v(0, -294) * mm, "radius": 2.5 * mm});
            skCircle(sketch, "E42.0.0.22", {"center": v(-7, -315) * mm, "radius": 2.5 * mm});
            skCircle(sketch, "E42.2.0.22", {"center": v(0, -308) * mm, "radius": 2.5 * mm});
            skCircle(sketch, "E42.0.1.20", {"center": v(7, -287) * mm, "radius": 2.5 * mm});
            skCircle(sketch, "E42.2.1.20", {"center": v(14, -280) * mm, "radius": 2.5 * mm});
            skCircle(sketch, "E42.0.1.21", {"center": v(7, -301) * mm, "radius": 2.5 * mm});
            skCircle(sketch, "E42.2.1.21", {"center": v(14, -294) * mm, "radius": 2.5 * mm});
            skCircle(sketch, "E42.0.1.22", {"center": v(7, -315) * mm, "radius": 2.5 * mm});
            skCircle(sketch, "E42.2.1.22", {"center": v(14, -308) * mm, "radius": 2.5 * mm});
            skCircle(sketch, "E42.0.2.20", {"center": v(21, -287) * mm, "radius": 2.5 * mm});
            skCircle(sketch, "E42.2.2.20", {"center": v(28, -280) * mm, "radius": 2.5 * mm});
            skCircle(sketch, "E42.0.2.21", {"center": v(21, -301) * mm, "radius": 2.5 * mm});
            skCircle(sketch, "E42.2.2.21", {"center": v(28, -294) * mm, "radius": 2.5 * mm});
            skCircle(sketch, "E42.0.2.22", {"center": v(21, -315) * mm, "radius": 2.5 * mm});
            skCircle(sketch, "E42.2.2.22", {"center": v(28, -308) * mm, "radius": 2.5 * mm});
            skCircle(sketch, "E42.0.3.20", {"center": v(35, -287) * mm, "radius": 2.5 * mm});
            skCircle(sketch, "E42.2.3.20", {"center": v(42, -280) * mm, "radius": 2.5 * mm});
            skCircle(sketch, "E42.0.3.21", {"center": v(35, -301) * mm, "radius": 2.5 * mm});
            skCircle(sketch, "E42.2.3.21", {"center": v(42, -294) * mm, "radius": 2.5 * mm});
            skCircle(sketch, "E42.0.3.22", {"center": v(35, -315) * mm, "radius": 2.5 * mm});
            skCircle(sketch, "E42.2.3.22", {"center": v(42, -308) * mm, "radius": 2.5 * mm});
            skCircle(sketch, "E42.0.4.20", {"center": v(49, -287) * mm, "radius": 2.5 * mm});
            skCircle(sketch, "E42.2.4.20", {"center": v(56, -280) * mm, "radius": 2.5 * mm});
            skCircle(sketch, "E42.0.4.21", {"center": v(49, -301) * mm, "radius": 2.5 * mm});
            skCircle(sketch, "E42.2.4.21", {"center": v(56, -294) * mm, "radius": 2.5 * mm});
            skCircle(sketch, "E42.0.4.22", {"center": v(49, -315) * mm, "radius": 2.5 * mm});
            skCircle(sketch, "E42.2.4.22", {"center": v(56, -308) * mm, "radius": 2.5 * mm});
            skCircle(sketch, "E42.0.5.20", {"center": v(63, -287) * mm, "radius": 2.5 * mm});
            skCircle(sketch, "E42.2.5.20", {"center": v(70, -280) * mm, "radius": 2.5 * mm});
            skCircle(sketch, "E42.0.5.21", {"center": v(63, -301) * mm, "radius": 2.5 * mm});
            skCircle(sketch, "E42.2.5.21", {"center": v(70, -294) * mm, "radius": 2.5 * mm});
            skCircle(sketch, "E42.0.5.22", {"center": v(63, -315) * mm, "radius": 2.5 * mm});
            skCircle(sketch, "E42.2.5.22", {"center": v(70, -308) * mm, "radius": 2.5 * mm});
            skCircle(sketch, "E42.0.6.20", {"center": v(77, -287) * mm, "radius": 2.5 * mm});
            skCircle(sketch, "E42.2.6.20", {"center": v(84, -280) * mm, "radius": 2.5 * mm});
            skCircle(sketch, "E42.0.6.21", {"center": v(77, -301) * mm, "radius": 2.5 * mm});
            skCircle(sketch, "E42.2.6.21", {"center": v(84, -294) * mm, "radius": 2.5 * mm});
            skCircle(sketch, "E42.0.6.22", {"center": v(77, -315) * mm, "radius": 2.5 * mm});
            skCircle(sketch, "E42.2.6.22", {"center": v(84, -308) * mm, "radius": 2.5 * mm});
            skCircle(sketch, "E42.0.7.20", {"center": v(91, -287) * mm, "radius": 2.5 * mm});
            skCircle(sketch, "E42.2.7.20", {"center": v(98, -280) * mm, "radius": 2.5 * mm});
            skCircle(sketch, "E42.0.7.21", {"center": v(91, -301) * mm, "radius": 2.5 * mm});
            skCircle(sketch, "E42.2.7.21", {"center": v(98, -294) * mm, "radius": 2.5 * mm});
            skCircle(sketch, "E42.0.7.22", {"center": v(91, -315) * mm, "radius": 2.5 * mm});
            skCircle(sketch, "E42.2.7.22", {"center": v(98, -308) * mm, "radius": 2.5 * mm});
            skCircle(sketch, "E42.0.8.20", {"center": v(105, -287) * mm, "radius": 2.5 * mm});
            skCircle(sketch, "E42.2.8.20", {"center": v(112, -280) * mm, "radius": 2.5 * mm});
            skCircle(sketch, "E42.0.8.21", {"center": v(105, -301) * mm, "radius": 2.5 * mm});
            skCircle(sketch, "E42.2.8.21", {"center": v(112, -294) * mm, "radius": 2.5 * mm});
            skCircle(sketch, "E42.0.8.22", {"center": v(105, -315) * mm, "radius": 2.5 * mm});
            skCircle(sketch, "E42.2.8.22", {"center": v(112, -308) * mm, "radius": 2.5 * mm});
            skCircle(sketch, "E42.0.9.20", {"center": v(119, -287) * mm, "radius": 2.5 * mm});
            skCircle(sketch, "E42.2.9.20", {"center": v(126, -280) * mm, "radius": 2.5 * mm});
            skCircle(sketch, "E42.0.9.21", {"center": v(119, -301) * mm, "radius": 2.5 * mm});
            skCircle(sketch, "E42.2.9.21", {"center": v(126, -294) * mm, "radius": 2.5 * mm});
            skCircle(sketch, "E42.0.9.22", {"center": v(119, -315) * mm, "radius": 2.5 * mm});
            skCircle(sketch, "E42.2.9.22", {"center": v(126, -308) * mm, "radius": 2.5 * mm});
            skCircle(sketch, "E42.0.10.20", {"center": v(133, -287) * mm, "radius": 2.5 * mm});
            skCircle(sketch, "E42.2.10.20", {"center": v(140, -280) * mm, "radius": 2.5 * mm});
            skCircle(sketch, "E42.0.10.21", {"center": v(133, -301) * mm, "radius": 2.5 * mm});
            skCircle(sketch, "E42.2.10.21", {"center": v(140, -294) * mm, "radius": 2.5 * mm});
            skCircle(sketch, "E42.0.10.22", {"center": v(133, -315) * mm, "radius": 2.5 * mm});
            skCircle(sketch, "E42.2.10.22", {"center": v(140, -308) * mm, "radius": 2.5 * mm});
            skCircle(sketch, "E42.0.11.20", {"center": v(147, -287) * mm, "radius": 2.5 * mm});
            skCircle(sketch, "E42.2.11.20", {"center": v(154, -280) * mm, "radius": 2.5 * mm});
            skCircle(sketch, "E42.0.11.21", {"center": v(147, -301) * mm, "radius": 2.5 * mm});
            skCircle(sketch, "E42.2.11.21", {"center": v(154, -294) * mm, "radius": 2.5 * mm});
            skCircle(sketch, "E42.0.11.22", {"center": v(147, -315) * mm, "radius": 2.5 * mm});
            skCircle(sketch, "E42.2.11.22", {"center": v(154, -308) * mm, "radius": 2.5 * mm});
            skCircle(sketch, "E42.0.12.20", {"center": v(161, -287) * mm, "radius": 2.5 * mm});
            skCircle(sketch, "E42.2.12.20", {"center": v(168, -280) * mm, "radius": 2.5 * mm});
            skCircle(sketch, "E42.0.12.21", {"center": v(161, -301) * mm, "radius": 2.5 * mm});
            skCircle(sketch, "E42.2.12.21", {"center": v(168, -294) * mm, "radius": 2.5 * mm});
            skCircle(sketch, "E42.0.12.22", {"center": v(161, -315) * mm, "radius": 2.5 * mm});
            skCircle(sketch, "E42.2.12.22", {"center": v(168, -308) * mm, "radius": 2.5 * mm});
            skCircle(sketch, "E42.0.13.20", {"center": v(175, -287) * mm, "radius": 2.5 * mm});
            skCircle(sketch, "E42.2.13.20", {"center": v(182, -280) * mm, "radius": 2.5 * mm});
            skCircle(sketch, "E42.0.13.21", {"center": v(175, -301) * mm, "radius": 2.5 * mm});
            skCircle(sketch, "E42.2.13.21", {"center": v(182, -294) * mm, "radius": 2.5 * mm});
            skCircle(sketch, "E42.0.13.22", {"center": v(175, -315) * mm, "radius": 2.5 * mm});
            skCircle(sketch, "E42.2.13.22", {"center": v(182, -308) * mm, "radius": 2.5 * mm});
            skCircle(sketch, "E42.0.14.20", {"center": v(189, -287) * mm, "radius": 2.5 * mm});
            skCircle(sketch, "E42.2.14.20", {"center": v(196, -280) * mm, "radius": 2.5 * mm});
            skCircle(sketch, "E42.0.14.21", {"center": v(189, -301) * mm, "radius": 2.5 * mm});
            skCircle(sketch, "E42.2.14.21", {"center": v(196, -294) * mm, "radius": 2.5 * mm});
            skCircle(sketch, "E42.0.14.22", {"center": v(189, -315) * mm, "radius": 2.5 * mm});
            skCircle(sketch, "E42.2.14.22", {"center": v(196, -308) * mm, "radius": 2.5 * mm});
            skCircle(sketch, "E42.0.15.20", {"center": v(203, -287) * mm, "radius": 2.5 * mm});
            skCircle(sketch, "E42.2.15.20", {"center": v(210, -280) * mm, "radius": 2.5 * mm});
            skCircle(sketch, "E42.0.15.21", {"center": v(203, -301) * mm, "radius": 2.5 * mm});
            skCircle(sketch, "E42.2.15.21", {"center": v(210, -294) * mm, "radius": 2.5 * mm});
            skCircle(sketch, "E42.0.15.22", {"center": v(203, -315) * mm, "radius": 2.5 * mm});
            skCircle(sketch, "E42.2.15.22", {"center": v(210, -308) * mm, "radius": 2.5 * mm});
            skCircle(sketch, "E42.0.16.20", {"center": v(217, -287) * mm, "radius": 2.5 * mm});
            skCircle(sketch, "E42.2.16.20", {"center": v(224, -280) * mm, "radius": 2.5 * mm});
            skCircle(sketch, "E42.0.16.21", {"center": v(217, -301) * mm, "radius": 2.5 * mm});
            skCircle(sketch, "E42.2.16.21", {"center": v(224, -294) * mm, "radius": 2.5 * mm});
            skCircle(sketch, "E42.0.16.22", {"center": v(217, -315) * mm, "radius": 2.5 * mm});
            skCircle(sketch, "E42.2.16.22", {"center": v(224, -308) * mm, "radius": 2.5 * mm});
            skCircle(sketch, "E42.0.17.20", {"center": v(231, -287) * mm, "radius": 2.5 * mm});
            skCircle(sketch, "E42.2.17.20", {"center": v(238, -280) * mm, "radius": 2.5 * mm});
            skCircle(sketch, "E42.0.17.21", {"center": v(231, -301) * mm, "radius": 2.5 * mm});
            skCircle(sketch, "E42.2.17.21", {"center": v(238, -294) * mm, "radius": 2.5 * mm});
            skCircle(sketch, "E42.0.17.22", {"center": v(231, -315) * mm, "radius": 2.5 * mm});
            skCircle(sketch, "E42.2.17.22", {"center": v(238, -308) * mm, "radius": 2.5 * mm});
            skCircle(sketch, "E42.0.18.20", {"center": v(245, -287) * mm, "radius": 2.5 * mm});
            skCircle(sketch, "E42.2.18.20", {"center": v(252, -280) * mm, "radius": 2.5 * mm});
            skCircle(sketch, "E42.0.18.21", {"center": v(245, -301) * mm, "radius": 2.5 * mm});
            skCircle(sketch, "E42.2.18.21", {"center": v(252, -294) * mm, "radius": 2.5 * mm});
            skCircle(sketch, "E42.0.18.22", {"center": v(245, -315) * mm, "radius": 2.5 * mm});
            skCircle(sketch, "E42.2.18.22", {"center": v(252, -308) * mm, "radius": 2.5 * mm});
            skCircle(sketch, "E42.0.19.20", {"center": v(259, -287) * mm, "radius": 2.5 * mm});
            skCircle(sketch, "E42.2.19.20", {"center": v(266, -280) * mm, "radius": 2.5 * mm});
            skCircle(sketch, "E42.0.19.21", {"center": v(259, -301) * mm, "radius": 2.5 * mm});
            skCircle(sketch, "E42.2.19.21", {"center": v(266, -294) * mm, "radius": 2.5 * mm});
            skCircle(sketch, "E42.0.19.22", {"center": v(259, -315) * mm, "radius": 2.5 * mm});
            skCircle(sketch, "E42.2.19.22", {"center": v(266, -308) * mm, "radius": 2.5 * mm});
            skCircle(sketch, "E42.0.20.20", {"center": v(273, -287) * mm, "radius": 2.5 * mm});
            skCircle(sketch, "E42.2.20.20", {"center": v(280, -280) * mm, "radius": 2.5 * mm});
            skCircle(sketch, "E42.0.20.21", {"center": v(273, -301) * mm, "radius": 2.5 * mm});
            skCircle(sketch, "E42.2.20.21", {"center": v(280, -294) * mm, "radius": 2.5 * mm});
            skCircle(sketch, "E42.0.20.22", {"center": v(273, -315) * mm, "radius": 2.5 * mm});
            skCircle(sketch, "E42.2.20.22", {"center": v(280, -308) * mm, "radius": 2.5 * mm});
            skCircle(sketch, "E42.0.21.20", {"center": v(287, -287) * mm, "radius": 2.5 * mm});
            skCircle(sketch, "E42.2.21.20", {"center": v(294, -280) * mm, "radius": 2.5 * mm});
            skCircle(sketch, "E42.0.21.21", {"center": v(287, -301) * mm, "radius": 2.5 * mm});
            skCircle(sketch, "E42.2.21.21", {"center": v(294, -294) * mm, "radius": 2.5 * mm});
            skCircle(sketch, "E42.0.21.22", {"center": v(287, -315) * mm, "radius": 2.5 * mm});
            skCircle(sketch, "E42.2.21.22", {"center": v(294, -308) * mm, "radius": 2.5 * mm});
            skCircle(sketch, "E42.0.22.20", {"center": v(301, -287) * mm, "radius": 2.5 * mm});
            skCircle(sketch, "E42.2.22.20", {"center": v(308, -280) * mm, "radius": 2.5 * mm});
            skCircle(sketch, "E42.0.22.21", {"center": v(301, -301) * mm, "radius": 2.5 * mm});
            skCircle(sketch, "E42.2.22.21", {"center": v(308, -294) * mm, "radius": 2.5 * mm});
            skCircle(sketch, "E42.0.22.22", {"center": v(301, -315) * mm, "radius": 2.5 * mm});
            skCircle(sketch, "E42.2.22.22", {"center": v(308, -308) * mm, "radius": 2.5 * mm});
            skCircle(sketch, "E42.0.23.20", {"center": v(315, -287) * mm, "radius": 2.5 * mm});
            skCircle(sketch, "E42.2.23.20", {"center": v(322, -280) * mm, "radius": 2.5 * mm});
            skCircle(sketch, "E42.0.23.21", {"center": v(315, -301) * mm, "radius": 2.5 * mm});
            skCircle(sketch, "E42.2.23.21", {"center": v(322, -294) * mm, "radius": 2.5 * mm});
            skCircle(sketch, "E42.0.23.22", {"center": v(315, -315) * mm, "radius": 2.5 * mm});
            skCircle(sketch, "E42.2.23.22", {"center": v(322, -308) * mm, "radius": 2.5 * mm});
            skCircle(sketch, "E42.0.24.20", {"center": v(329, -287) * mm, "radius": 2.5 * mm});
            skCircle(sketch, "E42.2.24.20", {"center": v(336, -280) * mm, "radius": 2.5 * mm});
            skCircle(sketch, "E42.0.24.21", {"center": v(329, -301) * mm, "radius": 2.5 * mm});
            skCircle(sketch, "E42.2.24.21", {"center": v(336, -294) * mm, "radius": 2.5 * mm});
            skCircle(sketch, "E42.0.24.22", {"center": v(329, -315) * mm, "radius": 2.5 * mm});
            skCircle(sketch, "E42.2.24.22", {"center": v(336, -308) * mm, "radius": 2.5 * mm});
            skCircle(sketch, "E42.0.25.20", {"center": v(343, -287) * mm, "radius": 2.5 * mm});
            skCircle(sketch, "E42.2.25.20", {"center": v(350, -280) * mm, "radius": 2.5 * mm});
            skCircle(sketch, "E42.0.25.21", {"center": v(343, -301) * mm, "radius": 2.5 * mm});
            skCircle(sketch, "E42.2.25.21", {"center": v(350, -294) * mm, "radius": 2.5 * mm});
            skCircle(sketch, "E42.0.25.22", {"center": v(343, -315) * mm, "radius": 2.5 * mm});
            skCircle(sketch, "E42.2.25.22", {"center": v(350, -308) * mm, "radius": 2.5 * mm});
            skCircle(sketch, "E42.0.26.20", {"center": v(357, -287) * mm, "radius": 2.5 * mm});
            skCircle(sketch, "E42.2.26.20", {"center": v(364, -280) * mm, "radius": 2.5 * mm});
            skCircle(sketch, "E42.0.26.21", {"center": v(357, -301) * mm, "radius": 2.5 * mm});
            skCircle(sketch, "E42.2.26.21", {"center": v(364, -294) * mm, "radius": 2.5 * mm});
            skCircle(sketch, "E42.0.26.22", {"center": v(357, -315) * mm, "radius": 2.5 * mm});
            skCircle(sketch, "E42.2.26.22", {"center": v(364, -308) * mm, "radius": 2.5 * mm});
            skCircle(sketch, "E42.0.27.20", {"center": v(371, -287) * mm, "radius": 2.5 * mm});
            skCircle(sketch, "E42.2.27.20", {"center": v(378, -280) * mm, "radius": 2.5 * mm});
            skCircle(sketch, "E42.0.27.21", {"center": v(371, -301) * mm, "radius": 2.5 * mm});
            skCircle(sketch, "E42.2.27.21", {"center": v(378, -294) * mm, "radius": 2.5 * mm});
            skCircle(sketch, "E42.0.27.22", {"center": v(371, -315) * mm, "radius": 2.5 * mm});
            skCircle(sketch, "E42.2.27.22", {"center": v(378, -308) * mm, "radius": 2.5 * mm});
            skCircle(sketch, "E42.0.28.20", {"center": v(385, -287) * mm, "radius": 2.5 * mm});
            skCircle(sketch, "E42.2.28.20", {"center": v(392, -280) * mm, "radius": 2.5 * mm});
            skCircle(sketch, "E42.0.28.21", {"center": v(385, -301) * mm, "radius": 2.5 * mm});
            skCircle(sketch, "E42.2.28.21", {"center": v(392, -294) * mm, "radius": 2.5 * mm});
            skCircle(sketch, "E42.0.28.22", {"center": v(385, -315) * mm, "radius": 2.5 * mm});
            skCircle(sketch, "E42.2.28.22", {"center": v(392, -308) * mm, "radius": 2.5 * mm});
            skCircle(sketch, "E42.0.29.20", {"center": v(399, -287) * mm, "radius": 2.5 * mm});
            skCircle(sketch, "E42.2.29.20", {"center": v(406, -280) * mm, "radius": 2.5 * mm});
            skCircle(sketch, "E42.0.29.21", {"center": v(399, -301) * mm, "radius": 2.5 * mm});
            skCircle(sketch, "E42.2.29.21", {"center": v(406, -294) * mm, "radius": 2.5 * mm});
            skCircle(sketch, "E42.0.29.22", {"center": v(399, -315) * mm, "radius": 2.5 * mm});
            skCircle(sketch, "E42.2.29.22", {"center": v(406, -308) * mm, "radius": 2.5 * mm});
            skCircle(sketch, "E42.0.30.20", {"center": v(413, -287) * mm, "radius": 2.5 * mm});
            skCircle(sketch, "E42.2.30.20", {"center": v(420, -280) * mm, "radius": 2.5 * mm});
            skCircle(sketch, "E42.0.30.21", {"center": v(413, -301) * mm, "radius": 2.5 * mm});
            skCircle(sketch, "E42.2.30.21", {"center": v(420, -294) * mm, "radius": 2.5 * mm});
            skCircle(sketch, "E42.0.30.22", {"center": v(413, -315) * mm, "radius": 2.5 * mm});
            skCircle(sketch, "E42.2.30.22", {"center": v(420, -308) * mm, "radius": 2.5 * mm});
            skCircle(sketch, "E42.0.31.20", {"center": v(427, -287) * mm, "radius": 2.5 * mm});
            skCircle(sketch, "E42.2.31.20", {"center": v(434, -280) * mm, "radius": 2.5 * mm});
            skCircle(sketch, "E42.0.31.21", {"center": v(427, -301) * mm, "radius": 2.5 * mm});
            skCircle(sketch, "E42.2.31.21", {"center": v(434, -294) * mm, "radius": 2.5 * mm});
            skCircle(sketch, "E42.0.31.22", {"center": v(427, -315) * mm, "radius": 2.5 * mm});
            skCircle(sketch, "E42.2.31.22", {"center": v(434, -308) * mm, "radius": 2.5 * mm});
            skCircle(sketch, "E42.0.32.20", {"center": v(441, -287) * mm, "radius": 2.5 * mm});
            skCircle(sketch, "E42.2.32.20", {"center": v(448, -280) * mm, "radius": 2.5 * mm});
            skCircle(sketch, "E42.0.32.21", {"center": v(441, -301) * mm, "radius": 2.5 * mm});
            skCircle(sketch, "E42.2.32.21", {"center": v(448, -294) * mm, "radius": 2.5 * mm});
            skCircle(sketch, "E42.0.32.22", {"center": v(441, -315) * mm, "radius": 2.5 * mm});
            skCircle(sketch, "E42.2.32.22", {"center": v(448, -308) * mm, "radius": 2.5 * mm});
            skCircle(sketch, "E42.0.33.20", {"center": v(455, -287) * mm, "radius": 2.5 * mm});
            skCircle(sketch, "E42.2.33.20", {"center": v(462, -280) * mm, "radius": 2.5 * mm});
            skCircle(sketch, "E42.0.33.21", {"center": v(455, -301) * mm, "radius": 2.5 * mm});
            skCircle(sketch, "E42.2.33.21", {"center": v(462, -294) * mm, "radius": 2.5 * mm});
            skCircle(sketch, "E42.0.33.22", {"center": v(455, -315) * mm, "radius": 2.5 * mm});
            skCircle(sketch, "E42.2.33.22", {"center": v(462, -308) * mm, "radius": 2.5 * mm});
            skCircle(sketch, "E42.0.34.20", {"center": v(469, -287) * mm, "radius": 2.5 * mm});
            skCircle(sketch, "E42.2.34.20", {"center": v(476, -280) * mm, "radius": 2.5 * mm});
            skCircle(sketch, "E42.0.34.21", {"center": v(469, -301) * mm, "radius": 2.5 * mm});
            skCircle(sketch, "E42.2.34.21", {"center": v(476, -294) * mm, "radius": 2.5 * mm});
            skCircle(sketch, "E42.0.34.22", {"center": v(469, -315) * mm, "radius": 2.5 * mm});
            skCircle(sketch, "E42.2.34.22", {"center": v(476, -308) * mm, "radius": 2.5 * mm});
            skSolve(sketch);
        }
        {
            var Q0;
            Q0 = qSketchRegion(id + "F6", true);
            extrude(context, id + "F7", {"entities" : qUnion([Q0]), "operationType" : NewBodyOperationType.REMOVE, "endBound" : BoundingType.THROUGH_ALL, "oppositeDirection" : true, "depth" : 25 * mm});
        }
        {
            var Q0;
            Q0=makeQuery(id+"F1.opExtrude","SWEPT_FACE",FACE,{"disambiguationData":[OSD([sQuery(id+"F0.wireOp",EDGE,"E3.MirrorCS")])]});
            var sketch = newSketch(context, id + "F8", { "sketchPlane" : qUnion([Q0])});
            skLineSegment(sketch, "E43.bottom", {"start": v(-320, 2) * mm, "end": v(-300, 2) * mm});
            skLineSegment(sketch, "E43.top", {"start": v(-315, -19.5) * mm, "end": v(-305, -19.5) * mm});
            skLineSegment(sketch, "E43.left", {"start": v(-320, 2) * mm, "end": v(-320, -14.5) * mm});
            skLineSegment(sketch, "E43.right", {"start": v(-300, 2) * mm, "end": v(-300, -14.5) * mm});
            skPoint(sketch, "E44.visualSharp", {"position": v(-320, -19.5) * mm});
            skArc(sketch, "E44.filletArc", {"start": v(-320, -14.5) * mm, "mid": v(-318.54, -18.04) * mm, "end": v(-315, -19.5) * mm});
            skPoint(sketch, "E45.visualSharp", {"position": v(-300, -19.5) * mm});
            skArc(sketch, "E45.filletArc", {"start": v(-305, -19.5) * mm, "mid": v(-301.46, -18.04) * mm, "end": v(-300, -14.5) * mm});
            skLineSegment(sketch, "E46", {"start": v(0, 0) * mm, "end": v(0, -38.01) * mm, "construction": true});
            skArc(sketch, "E47.MirrorCS", {"start": v(320, -14.5) * mm, "mid": v(318.54, -18.04) * mm, "end": v(315, -19.5) * mm});
            skArc(sketch, "E48.MirrorCS", {"start": v(305, -19.5) * mm, "mid": v(301.46, -18.04) * mm, "end": v(300, -14.5) * mm});
            skPoint(sketch, "E49.MirrorP", {"position": v(320, -19.5) * mm});
            skLineSegment(sketch, "E50.MirrorCS", {"start": v(320, 2) * mm, "end": v(320, -14.5) * mm});
            skLineSegment(sketch, "E51.MirrorCS", {"start": v(300, 2) * mm, "end": v(300, -14.5) * mm});
            skPoint(sketch, "E52.MirrorP", {"position": v(300, -19.5) * mm});
            skLineSegment(sketch, "E53.MirrorCS", {"start": v(320, 2) * mm, "end": v(300, 2) * mm});
            skLineSegment(sketch, "E54.MirrorCS", {"start": v(315, -19.5) * mm, "end": v(305, -19.5) * mm});
            skSolve(sketch);
        }
        {
            var Q0;
            Q0 = qSketchRegion(id + "F8", true);
            extrude(context, id + "F9", {"entities" : qUnion([Q0]), "oppositeDirection" : true, "depth" : 1.5 * mm});
        }
        {
            var Q0;
            Q0=makeQuery(id+"F3.boolean.opBoolean","MERGE",FACE,{"derivedFrom":[makeQuery(id+"F1.opExtrude","SWEPT_FACE",FACE,{"disambiguationData":[OSD([sQuery(id+"F0.wireOp",EDGE,"E0")])]}),makeQuery(id+"F3.opExtrude","SWEPT_FACE",FACE,{"disambiguationData":[OSD([sQuery(id+"F2.wireOp",EDGE,"E11.top")])]}),makeQuery(id+"F3.opExtrude","SWEPT_FACE",FACE,{"disambiguationData":[OSD([sQuery(id+"F2.wireOp",EDGE,"E12.top")])]})]});
            var sketch = newSketch(context, id + "F10", { "sketchPlane" : qUnion([Q0])});
            skLineSegment(sketch, "E55.bottom", {"start": v(521, 320) * mm, "end": v(491, 320) * mm});
            skLineSegment(sketch, "E55.top", {"start": v(521, 298) * mm, "end": v(501, 298) * mm});
            skLineSegment(sketch, "E55.left", {"start": v(521, 320) * mm, "end": v(521, 300) * mm});
            skLineSegment(sketch, "E55.right", {"start": v(496, 315) * mm, "end": v(496, 303) * mm});
            skLineSegment(sketch, "E56", {"start": v(521, 298) * mm, "end": v(522.5, 298) * mm});
            skLineSegment(sketch, "E57", {"start": v(522.5, 298) * mm, "end": v(522.5, 300) * mm});
            skLineSegment(sketch, "E58", {"start": v(522.5, 300) * mm, "end": v(521, 300) * mm});
            skPoint(sketch, "E59.newPointA", {"position": v(520.5, 320) * mm});
            skArc(sketch, "E59.filletArc", {"start": v(496, 315) * mm, "mid": v(494.54, 318.54) * mm, "end": v(491, 320) * mm});
            skPoint(sketch, "E60.visualSharp", {"position": v(496, 298) * mm});
            skArc(sketch, "E60.filletArc", {"start": v(496, 303) * mm, "mid": v(497.46, 299.46) * mm, "end": v(501, 298) * mm});
            skPoint(sketch, "E61.0.start.orphan", {"position": v(487.5, 320) * mm});
            skLineSegment(sketch, "E62", {"start": v(0, 0) * mm, "end": v(0, 91.72) * mm, "construction": true});
            skLineSegment(sketch, "E63", {"start": v(0, 0) * mm, "end": v(-144.07, 0) * mm, "construction": true});
            skLineSegment(sketch, "E64.MirrorCS", {"start": v(521, -298) * mm, "end": v(501, -298) * mm});
            skLineSegment(sketch, "E65.MirrorCS", {"start": v(521, -320) * mm, "end": v(521, -300) * mm});
            skLineSegment(sketch, "E66.MirrorCS", {"start": v(496, -315) * mm, "end": v(496, -303) * mm});
            skLineSegment(sketch, "E67.MirrorCS", {"start": v(521, -298) * mm, "end": v(522.5, -298) * mm});
            skLineSegment(sketch, "E68.MirrorCS", {"start": v(522.5, -298) * mm, "end": v(522.5, -300) * mm});
            skLineSegment(sketch, "E69.MirrorCS", {"start": v(522.5, -300) * mm, "end": v(521, -300) * mm});
            skArc(sketch, "E70.MirrorCS", {"start": v(496, -315) * mm, "mid": v(494.54, -318.54) * mm, "end": v(491, -320) * mm});
            skArc(sketch, "E71.MirrorCS", {"start": v(496, -303) * mm, "mid": v(497.46, -299.46) * mm, "end": v(501, -298) * mm});
            skLineSegment(sketch, "E72.MirrorCS", {"start": v(521, -320) * mm, "end": v(491, -320) * mm});
            skPoint(sketch, "E73.MirrorP", {"position": v(520.5, -320) * mm});
            skPoint(sketch, "E74.MirrorP", {"position": v(496, -298) * mm});
            skPoint(sketch, "E75.MirrorP", {"position": v(487.5, -320) * mm});
            skLineSegment(sketch, "E76.MirrorCS", {"start": v(-521, 298) * mm, "end": v(-522.5, 298) * mm});
            skLineSegment(sketch, "E77.MirrorCS", {"start": v(-522.5, 298) * mm, "end": v(-522.5, 300) * mm});
            skLineSegment(sketch, "E78.MirrorCS", {"start": v(-522.5, 300) * mm, "end": v(-521, 300) * mm});
            skLineSegment(sketch, "E79.MirrorCS", {"start": v(-521, -298) * mm, "end": v(-522.5, -298) * mm});
            skLineSegment(sketch, "E80.MirrorCS", {"start": v(-522.5, -298) * mm, "end": v(-522.5, -300) * mm});
            skLineSegment(sketch, "E81.MirrorCS", {"start": v(-522.5, -300) * mm, "end": v(-521, -300) * mm});
            skLineSegment(sketch, "E82.MirrorCS", {"start": v(-496, -315) * mm, "end": v(-496, -303) * mm});
            skLineSegment(sketch, "E83.MirrorCS", {"start": v(-496, 315) * mm, "end": v(-496, 303) * mm});
            skArc(sketch, "E84.MirrorCS", {"start": v(-496, 315) * mm, "mid": v(-494.54, 318.54) * mm, "end": v(-491, 320) * mm});
            skArc(sketch, "E85.MirrorCS", {"start": v(-496, 303) * mm, "mid": v(-497.46, 299.46) * mm, "end": v(-501, 298) * mm});
            skLineSegment(sketch, "E86.MirrorCS", {"start": v(-521, 298) * mm, "end": v(-501, 298) * mm});
            skArc(sketch, "E87.MirrorCS", {"start": v(-496, -303) * mm, "mid": v(-497.46, -299.46) * mm, "end": v(-501, -298) * mm});
            skLineSegment(sketch, "E88.MirrorCS", {"start": v(-521, 320) * mm, "end": v(-521, 300) * mm});
            skArc(sketch, "E89.MirrorCS", {"start": v(-496, -315) * mm, "mid": v(-494.54, -318.54) * mm, "end": v(-491, -320) * mm});
            skLineSegment(sketch, "E90.MirrorCS", {"start": v(-521, -320) * mm, "end": v(-521, -300) * mm});
            skLineSegment(sketch, "E91.MirrorCS", {"start": v(-521, -298) * mm, "end": v(-501, -298) * mm});
            skLineSegment(sketch, "E92.MirrorCS", {"start": v(-521, 320) * mm, "end": v(-491, 320) * mm});
            skLineSegment(sketch, "E93.MirrorCS", {"start": v(-521, -320) * mm, "end": v(-491, -320) * mm});
            skPoint(sketch, "E94.MirrorP", {"position": v(-487.5, 320) * mm});
            skPoint(sketch, "E95.MirrorP", {"position": v(-496, 298) * mm});
            skPoint(sketch, "E96.MirrorP", {"position": v(-520.5, 320) * mm});
            skPoint(sketch, "E97.MirrorP", {"position": v(-487.5, -320) * mm});
            skPoint(sketch, "E98.MirrorP", {"position": v(-496, -298) * mm});
            skPoint(sketch, "E99.MirrorP", {"position": v(-520.5, -320) * mm});
            skLineSegment(sketch, "E100", {"start": v(487.5, 325) * mm, "end": v(504.48, 341.98) * mm, "construction": true});
            skLineSegment(sketch, "E101.MirrorCS", {"start": v(460.5, 358.5) * mm, "end": v(460.5, 360) * mm});
            skLineSegment(sketch, "E102.MirrorCS", {"start": v(462.5, 360) * mm, "end": v(462.5, 358.5) * mm});
            skLineSegment(sketch, "E103.MirrorCS", {"start": v(460.5, 360) * mm, "end": v(462.5, 360) * mm});
            skLineSegment(sketch, "E104.MirrorCS", {"start": v(482.5, 358.5) * mm, "end": v(482.5, 328.5) * mm});
            skLineSegment(sketch, "E105.MirrorCS", {"start": v(460.5, 358.5) * mm, "end": v(460.5, 338.5) * mm});
            skLineSegment(sketch, "E106.MirrorCS", {"start": v(482.5, 358.5) * mm, "end": v(462.5, 358.5) * mm});
            skLineSegment(sketch, "E107.MirrorCS", {"start": v(477.5, 333.5) * mm, "end": v(465.5, 333.5) * mm});
            skArc(sketch, "E108.MirrorCS", {"start": v(477.5, 333.5) * mm, "mid": v(481.04, 332.04) * mm, "end": v(482.5, 328.5) * mm});
            skArc(sketch, "E109.MirrorCS", {"start": v(465.5, 333.5) * mm, "mid": v(461.96, 334.96) * mm, "end": v(460.5, 338.5) * mm});
            skPoint(sketch, "E110.MirrorP", {"position": v(482.5, 358) * mm});
            skPoint(sketch, "E111.MirrorP", {"position": v(460.5, 333.5) * mm});
            skPoint(sketch, "E112.MirrorP", {"position": v(482.5, 325) * mm});
            skLineSegment(sketch, "E113.MirrorCS", {"start": v(-460.5, 360) * mm, "end": v(-462.5, 360) * mm});
            skLineSegment(sketch, "E114.MirrorCS", {"start": v(-462.5, 360) * mm, "end": v(-462.5, 358.5) * mm});
            skLineSegment(sketch, "E115.MirrorCS", {"start": v(-460.5, 358.5) * mm, "end": v(-460.5, 360) * mm});
            skLineSegment(sketch, "E116.MirrorCS", {"start": v(-477.5, 333.5) * mm, "end": v(-465.5, 333.5) * mm});
            skArc(sketch, "E117.MirrorCS", {"start": v(-477.5, 333.5) * mm, "mid": v(-481.04, 332.04) * mm, "end": v(-482.5, 328.5) * mm});
            skArc(sketch, "E118.MirrorCS", {"start": v(-465.5, 333.5) * mm, "mid": v(-461.96, 334.96) * mm, "end": v(-460.5, 338.5) * mm});
            skLineSegment(sketch, "E119.MirrorCS", {"start": v(-482.5, 358.5) * mm, "end": v(-462.5, 358.5) * mm});
            skLineSegment(sketch, "E120.MirrorCS", {"start": v(-460.5, 358.5) * mm, "end": v(-460.5, 338.5) * mm});
            skLineSegment(sketch, "E121.MirrorCS", {"start": v(-482.5, 358.5) * mm, "end": v(-482.5, 328.5) * mm});
            skPoint(sketch, "E122.MirrorP", {"position": v(-482.5, 325) * mm});
            skPoint(sketch, "E123.MirrorP", {"position": v(-460.5, 333.5) * mm});
            skPoint(sketch, "E124.MirrorP", {"position": v(-482.5, 358) * mm});
            skLineSegment(sketch, "E125.MirrorCS", {"start": v(-460.5, -360) * mm, "end": v(-462.5, -360) * mm});
            skLineSegment(sketch, "E126.MirrorCS", {"start": v(-462.5, -360) * mm, "end": v(-462.5, -358.5) * mm});
            skLineSegment(sketch, "E127.MirrorCS", {"start": v(-460.5, -358.5) * mm, "end": v(-460.5, -360) * mm});
            skPoint(sketch, "E128.MirrorP", {"position": v(-482.5, -325) * mm});
            skPoint(sketch, "E129.MirrorP", {"position": v(-460.5, -333.5) * mm});
            skPoint(sketch, "E130.MirrorP", {"position": v(-482.5, -358) * mm});
            skArc(sketch, "E131.MirrorCS", {"start": v(-477.5, -333.5) * mm, "mid": v(-481.04, -332.04) * mm, "end": v(-482.5, -328.5) * mm});
            skArc(sketch, "E132.MirrorCS", {"start": v(-465.5, -333.5) * mm, "mid": v(-461.96, -334.96) * mm, "end": v(-460.5, -338.5) * mm});
            skLineSegment(sketch, "E133.MirrorCS", {"start": v(-482.5, -358.5) * mm, "end": v(-462.5, -358.5) * mm});
            skLineSegment(sketch, "E134.MirrorCS", {"start": v(-460.5, -358.5) * mm, "end": v(-460.5, -338.5) * mm});
            skLineSegment(sketch, "E135.MirrorCS", {"start": v(-482.5, -358.5) * mm, "end": v(-482.5, -328.5) * mm});
            skLineSegment(sketch, "E136.MirrorCS", {"start": v(-477.5, -333.5) * mm, "end": v(-465.5, -333.5) * mm});
            skLineSegment(sketch, "E137.MirrorCS", {"start": v(460.5, -360) * mm, "end": v(462.5, -360) * mm});
            skLineSegment(sketch, "E138.MirrorCS", {"start": v(462.5, -360) * mm, "end": v(462.5, -358.5) * mm});
            skLineSegment(sketch, "E139.MirrorCS", {"start": v(460.5, -358.5) * mm, "end": v(460.5, -360) * mm});
            skArc(sketch, "E140.MirrorCS", {"start": v(465.5, -333.5) * mm, "mid": v(461.96, -334.96) * mm, "end": v(460.5, -338.5) * mm});
            skLineSegment(sketch, "E141.MirrorCS", {"start": v(477.5, -333.5) * mm, "end": v(465.5, -333.5) * mm});
            skArc(sketch, "E142.MirrorCS", {"start": v(477.5, -333.5) * mm, "mid": v(481.04, -332.04) * mm, "end": v(482.5, -328.5) * mm});
            skPoint(sketch, "E143.MirrorP", {"position": v(482.5, -325) * mm});
            skLineSegment(sketch, "E144.MirrorCS", {"start": v(482.5, -358.5) * mm, "end": v(462.5, -358.5) * mm});
            skLineSegment(sketch, "E145.MirrorCS", {"start": v(460.5, -358.5) * mm, "end": v(460.5, -338.5) * mm});
            skPoint(sketch, "E146.MirrorP", {"position": v(460.5, -333.5) * mm});
            skLineSegment(sketch, "E147.MirrorCS", {"start": v(482.5, -358.5) * mm, "end": v(482.5, -328.5) * mm});
            skPoint(sketch, "E148.MirrorP", {"position": v(482.5, -358) * mm});
            skSolve(sketch);
        }
        {
            var Q0;
            Q0 = qSketchRegion(id + "F10", true);
            extrude(context, id + "F11", {"entities" : qUnion([Q0]), "operationType" : NewBodyOperationType.REMOVE, "oppositeDirection" : true, "depth" : 3 * mm});
        }
        {
            var Q0;
            Q0=makeQuery(id+"F3.boolean.opBoolean","MERGE",FACE,{"derivedFrom":[makeQuery(id+"F1.opExtrude","CAP_FACE",FACE,{"disambiguationData":[OSD([sQuery(id+"F0.wireOp",EDGE,"E0"),sQuery(id+"F0.wireOp",EDGE,"E1"),sQuery(id+"F0.wireOp",EDGE,"E3.MirrorCS"),sQuery(id+"F0.wireOp",EDGE,"E4.0"),sQuery(id+"F0.wireOp",EDGE,"E4.1"),sQuery(id+"F0.wireOp",EDGE,"E4.2"),sQuery(id+"F0.wireOp",EDGE,"E5"),sQuery(id+"F0.wireOp",EDGE,"E6"),sQuery(id+"F0.wireOp",EDGE,"E7.filletArc"),sQuery(id+"F0.wireOp",EDGE,"E8.filletArc"),sQuery(id+"F0.wireOp",EDGE,"E9.filletArc"),sQuery(id+"F0.wireOp",EDGE,"E10.filletArc")])],"isStart":true}),makeQuery(id+"F3.opExtrude","SWEPT_FACE",FACE,{"disambiguationData":[OSD([sQuery(id+"F2.wireOp",EDGE,"E11.left")])]})]});
            var sketch = newSketch(context, id + "F12", { "sketchPlane" : qUnion([Q0])});
            skLineSegment(sketch, "E149.bottom", {"start": v(-482.5, 2) * mm, "end": v(-462.5, 2) * mm});
            skLineSegment(sketch, "E149.top", {"start": v(-477.5, -19.5) * mm, "end": v(-467.5, -19.5) * mm});
            skLineSegment(sketch, "E149.left", {"start": v(-482.5, 2) * mm, "end": v(-482.5, -14.5) * mm});
            skLineSegment(sketch, "E149.right", {"start": v(-462.5, 2) * mm, "end": v(-462.5, -14.5) * mm});
            skLineSegment(sketch, "E150", {"start": v(0, 0) * mm, "end": v(0, 62.53) * mm, "construction": true});
            skPoint(sketch, "E151.visualSharp", {"position": v(-482.5, -19.5) * mm});
            skArc(sketch, "E151.filletArc", {"start": v(-482.5, -14.5) * mm, "mid": v(-481.04, -18.04) * mm, "end": v(-477.5, -19.5) * mm});
            skPoint(sketch, "E152.visualSharp", {"position": v(-462.5, -19.5) * mm});
            skArc(sketch, "E152.filletArc", {"start": v(-467.5, -19.5) * mm, "mid": v(-463.96, -18.04) * mm, "end": v(-462.5, -14.5) * mm});
            skPoint(sketch, "E153.MirrorP", {"position": v(482.5, -19.5) * mm});
            skPoint(sketch, "E154.MirrorP", {"position": v(462.5, -19.5) * mm});
            skLineSegment(sketch, "E155.MirrorCS", {"start": v(477.5, -19.5) * mm, "end": v(467.5, -19.5) * mm});
            skArc(sketch, "E156.MirrorCS", {"start": v(482.5, -14.5) * mm, "mid": v(481.04, -18.04) * mm, "end": v(477.5, -19.5) * mm});
            skArc(sketch, "E157.MirrorCS", {"start": v(467.5, -19.5) * mm, "mid": v(463.96, -18.04) * mm, "end": v(462.5, -14.5) * mm});
            skLineSegment(sketch, "E158.MirrorCS", {"start": v(482.5, 2) * mm, "end": v(462.5, 2) * mm});
            skLineSegment(sketch, "E159.MirrorCS", {"start": v(482.5, 2) * mm, "end": v(482.5, -14.5) * mm});
            skLineSegment(sketch, "E160.MirrorCS", {"start": v(462.5, 2) * mm, "end": v(462.5, -14.5) * mm});
            skSolve(sketch);
        }
        {
            var Q0;
            Q0 = qSketchRegion(id + "F12", true);
            extrude(context, id + "F13", {"entities" : qUnion([Q0]), "operationType" : NewBodyOperationType.ADD, "oppositeDirection" : true, "depth" : 1.5 * mm});
        }
        {
            var Q0;
            Q0=makeQuery(id+"F9.opExtrude","SWEPT_BODY",BODY,{"disambiguationData":[OSD([sQuery(id+"F8.wireOp",EDGE,"E47.MirrorCS"),sQuery(id+"F8.wireOp",EDGE,"E48.MirrorCS"),sQuery(id+"F8.wireOp",EDGE,"E50.MirrorCS"),sQuery(id+"F8.wireOp",EDGE,"E51.MirrorCS"),sQuery(id+"F8.wireOp",EDGE,"E53.MirrorCS"),sQuery(id+"F8.wireOp",EDGE,"E54.MirrorCS")])]});
            var Q1;
            Q1=qCreatedBy(makeId("Right.planeOp"),FACE);
            mirror(context, id + "F14", {"operationType" : NewBodyOperationType.ADD, "entities" : qUnion([Q0]), "mirrorPlane" : qUnion([Q1])});
        }
        {
            var Q0;
            Q0=makeQuery(id+"F9.opExtrude","SWEPT_BODY",BODY,{"disambiguationData":[OSD([sQuery(id+"F8.wireOp",EDGE,"E43.bottom"),sQuery(id+"F8.wireOp",EDGE,"E43.top"),sQuery(id+"F8.wireOp",EDGE,"E43.left"),sQuery(id+"F8.wireOp",EDGE,"E43.right"),sQuery(id+"F8.wireOp",EDGE,"E44.filletArc"),sQuery(id+"F8.wireOp",EDGE,"E45.filletArc")])]});
            var Q1;
            Q1=qCreatedBy(makeId("Right.planeOp"),FACE);
            mirror(context, id + "F15", {"operationType" : NewBodyOperationType.ADD, "entities" : qUnion([Q0]), "mirrorPlane" : qUnion([Q1])});
        }
        {
            var Q0;
            Q0=makeQuery(id+"F3.boolean.opBoolean","MERGE",FACE,{"derivedFrom":[makeQuery(id+"F1.opExtrude","CAP_FACE",FACE,{"disambiguationData":[OSD([sQuery(id+"F0.wireOp",EDGE,"E0"),sQuery(id+"F0.wireOp",EDGE,"E1"),sQuery(id+"F0.wireOp",EDGE,"E3.MirrorCS"),sQuery(id+"F0.wireOp",EDGE,"E4.0"),sQuery(id+"F0.wireOp",EDGE,"E4.1"),sQuery(id+"F0.wireOp",EDGE,"E4.2"),sQuery(id+"F0.wireOp",EDGE,"E5"),sQuery(id+"F0.wireOp",EDGE,"E6"),sQuery(id+"F0.wireOp",EDGE,"E7.filletArc"),sQuery(id+"F0.wireOp",EDGE,"E8.filletArc"),sQuery(id+"F0.wireOp",EDGE,"E9.filletArc"),sQuery(id+"F0.wireOp",EDGE,"E10.filletArc")])],"isStart":false}),makeQuery(id+"F3.opExtrude","SWEPT_FACE",FACE,{"disambiguationData":[OSD([sQuery(id+"F2.wireOp",EDGE,"E12.left")])]})]});
            var sketch = newSketch(context, id + "F16", { "sketchPlane" : qUnion([Q0])});
            skLineSegment(sketch, "E161.bottom", {"start": v(-482.5, 2) * mm, "end": v(-462.5, 2) * mm});
            skLineSegment(sketch, "E161.top", {"start": v(-477.5, -19.5) * mm, "end": v(-467.5, -19.5) * mm});
            skLineSegment(sketch, "E161.left", {"start": v(-482.5, 2) * mm, "end": v(-482.5, -14.5) * mm});
            skLineSegment(sketch, "E161.right", {"start": v(-462.5, 2) * mm, "end": v(-462.5, -14.5) * mm});
            skPoint(sketch, "E162.visualSharp", {"position": v(-482.5, -19.5) * mm});
            skArc(sketch, "E162.filletArc", {"start": v(-482.5, -14.5) * mm, "mid": v(-481.04, -18.04) * mm, "end": v(-477.5, -19.5) * mm});
            skPoint(sketch, "E163.visualSharp", {"position": v(-462.5, -19.5) * mm});
            skArc(sketch, "E163.filletArc", {"start": v(-467.5, -19.5) * mm, "mid": v(-463.96, -18.04) * mm, "end": v(-462.5, -14.5) * mm});
            skLineSegment(sketch, "E164", {"start": v(0, 0) * mm, "end": v(0, -47.44) * mm, "construction": true});
            skArc(sketch, "E165.MirrorCS", {"start": v(482.5, -14.5) * mm, "mid": v(481.04, -18.04) * mm, "end": v(477.5, -19.5) * mm});
            skArc(sketch, "E166.MirrorCS", {"start": v(467.5, -19.5) * mm, "mid": v(463.96, -18.04) * mm, "end": v(462.5, -14.5) * mm});
            skLineSegment(sketch, "E167.MirrorCS", {"start": v(477.5, -19.5) * mm, "end": v(467.5, -19.5) * mm});
            skLineSegment(sketch, "E168.MirrorCS", {"start": v(482.5, 2) * mm, "end": v(482.5, -14.5) * mm});
            skPoint(sketch, "E169.MirrorP", {"position": v(482.5, -19.5) * mm});
            skLineSegment(sketch, "E170.MirrorCS", {"start": v(482.5, 2) * mm, "end": v(462.5, 2) * mm});
            skPoint(sketch, "E171.MirrorP", {"position": v(462.5, -19.5) * mm});
            skLineSegment(sketch, "E172.MirrorCS", {"start": v(462.5, 2) * mm, "end": v(462.5, -14.5) * mm});
            skSolve(sketch);
        }
        {
            var Q0;
            Q0 = qSketchRegion(id + "F16", true);
            extrude(context, id + "F17", {"entities" : qUnion([Q0]), "oppositeDirection" : true, "depth" : 1.5 * mm});
        }
        {
            var Q0;
            Q0=makeQuery(id+"F13.boolean.opBoolean","MERGE",FACE,{"derivedFrom":[makeQuery(id+"F3.boolean.opBoolean","MERGE",FACE,{"derivedFrom":[makeQuery(id+"F1.opExtrude","CAP_FACE",FACE,{"disambiguationData":[OSD([sQuery(id+"F0.wireOp",EDGE,"E0"),sQuery(id+"F0.wireOp",EDGE,"E1"),sQuery(id+"F0.wireOp",EDGE,"E3.MirrorCS"),sQuery(id+"F0.wireOp",EDGE,"E4.0"),sQuery(id+"F0.wireOp",EDGE,"E4.1"),sQuery(id+"F0.wireOp",EDGE,"E4.2"),sQuery(id+"F0.wireOp",EDGE,"E5"),sQuery(id+"F0.wireOp",EDGE,"E6"),sQuery(id+"F0.wireOp",EDGE,"E7.filletArc"),sQuery(id+"F0.wireOp",EDGE,"E8.filletArc"),sQuery(id+"F0.wireOp",EDGE,"E9.filletArc"),sQuery(id+"F0.wireOp",EDGE,"E10.filletArc")])],"isStart":true}),makeQuery(id+"F3.opExtrude","SWEPT_FACE",FACE,{"disambiguationData":[OSD([sQuery(id+"F2.wireOp",EDGE,"E11.left")])]})]}),makeQuery(id+"F13.opExtrude","CAP_FACE",FACE,{"disambiguationData":[OSD([sQuery(id+"F12.wireOp",EDGE,"E149.bottom"),sQuery(id+"F12.wireOp",EDGE,"E149.top"),sQuery(id+"F12.wireOp",EDGE,"E149.left"),sQuery(id+"F12.wireOp",EDGE,"E149.right"),sQuery(id+"F12.wireOp",EDGE,"E151.filletArc"),sQuery(id+"F12.wireOp",EDGE,"E152.filletArc")])],"isStart":true}),makeQuery(id+"F13.opExtrude","CAP_FACE",FACE,{"disambiguationData":[OSD([sQuery(id+"F12.wireOp",EDGE,"E155.MirrorCS"),sQuery(id+"F12.wireOp",EDGE,"E156.MirrorCS"),sQuery(id+"F12.wireOp",EDGE,"E157.MirrorCS"),sQuery(id+"F12.wireOp",EDGE,"E158.MirrorCS"),sQuery(id+"F12.wireOp",EDGE,"E159.MirrorCS"),sQuery(id+"F12.wireOp",EDGE,"E160.MirrorCS")])],"isStart":true})]});
            var sketch = newSketch(context, id + "F18", { "sketchPlane" : qUnion([Q0])});
            skLineSegment(sketch, "E173", {"start": v(0, 0) * mm, "end": v(0, 58) * mm, "construction": true});
            skCircle(sketch, "E174", {"center": v(0, 29) * mm, "radius": 20 * mm});
            skCircle(sketch, "E175.1.0.0", {"center": v(75, 29) * mm, "radius": 20 * mm});
            skCircle(sketch, "E175.2.0.0", {"center": v(150, 29) * mm, "radius": 20 * mm});
            skCircle(sketch, "E175.3.0.0", {"center": v(225, 29) * mm, "radius": 20 * mm});
            skCircle(sketch, "E175.4.0.0", {"center": v(300, 29) * mm, "radius": 20 * mm});
            skCircle(sketch, "E175.5.0.0", {"center": v(375, 29) * mm, "radius": 20 * mm});
            skCircle(sketch, "E175.6.0.0", {"center": v(450, 29) * mm, "radius": 20 * mm});
            skLineSegment(sketch, "E175.direction1", {"start": v(0, 29) * mm, "end": v(75, 29) * mm, "construction": true});
            skCircle(sketch, "E176.MirrorC", {"center": v(-225, 29) * mm, "radius": 20 * mm});
            skLineSegment(sketch, "E177.MirrorCS", {"start": v(0, 29) * mm, "end": v(-75, 29) * mm, "construction": true});
            skCircle(sketch, "E178.MirrorC", {"center": v(-150, 29) * mm, "radius": 20 * mm});
            skCircle(sketch, "E179.MirrorC", {"center": v(-75, 29) * mm, "radius": 20 * mm});
            skCircle(sketch, "E180.MirrorC", {"center": v(-300, 29) * mm, "radius": 20 * mm});
            skCircle(sketch, "E181.MirrorC", {"center": v(-450, 29) * mm, "radius": 20 * mm});
            skCircle(sketch, "E182.MirrorC", {"center": v(-375, 29) * mm, "radius": 20 * mm});
            skSolve(sketch);
        }
        {
            var Q0;
            Q0 = qSketchRegion(id + "F18", true);
            extrude(context, id + "F19", {"entities" : qUnion([Q0]), "operationType" : NewBodyOperationType.REMOVE, "endBound" : BoundingType.THROUGH_ALL, "oppositeDirection" : true, "depth" : 25 * mm});
        }
        {
            var Q0;
            Q0=makeQuery(id+"F7.boolean.opBoolean","INTERSECT",EDGE,{"derivedFrom":[makeQuery(id+"F3.boolean.opBoolean","MERGE",FACE,{"derivedFrom":[makeQuery(id+"F1.opExtrude","SWEPT_FACE",FACE,{"disambiguationData":[OSD([sQuery(id+"F0.wireOp",EDGE,"E5")])]}),makeQuery(id+"F1.opExtrude","SWEPT_FACE",FACE,{"disambiguationData":[OSD([sQuery(id+"F0.wireOp",EDGE,"E6")])]}),makeQuery(id+"F3.opExtrude","SWEPT_FACE",FACE,{"disambiguationData":[OSD([sQuery(id+"F2.wireOp",EDGE,"E11.bottom")])]}),makeQuery(id+"F3.opExtrude","SWEPT_FACE",FACE,{"disambiguationData":[OSD([sQuery(id+"F2.wireOp",EDGE,"E12.bottom")])]})]}),makeQuery(id+"F7.opExtrude","SWEPT_FACE",FACE,{"disambiguationData":[OSD([sQuery(id+"F6.wireOp",EDGE,"E33.MirrorCS")])]})]});
            var Q1;
            Q1=makeQuery(id+"F7.boolean.opBoolean","INTERSECT",EDGE,{"derivedFrom":[makeQuery(id+"F3.boolean.opBoolean","MERGE",FACE,{"derivedFrom":[makeQuery(id+"F1.opExtrude","SWEPT_FACE",FACE,{"disambiguationData":[OSD([sQuery(id+"F0.wireOp",EDGE,"E5")])]}),makeQuery(id+"F1.opExtrude","SWEPT_FACE",FACE,{"disambiguationData":[OSD([sQuery(id+"F0.wireOp",EDGE,"E6")])]}),makeQuery(id+"F3.opExtrude","SWEPT_FACE",FACE,{"disambiguationData":[OSD([sQuery(id+"F2.wireOp",EDGE,"E11.bottom")])]}),makeQuery(id+"F3.opExtrude","SWEPT_FACE",FACE,{"disambiguationData":[OSD([sQuery(id+"F2.wireOp",EDGE,"E12.bottom")])]})]}),makeQuery(id+"F7.opExtrude","SWEPT_FACE",FACE,{"disambiguationData":[OSD([sQuery(id+"F6.wireOp",EDGE,"E35.MirrorCS")])]})]});
            var Q2;
            Q2=makeQuery(id+"F7.boolean.opBoolean","INTERSECT",EDGE,{"derivedFrom":[makeQuery(id+"F3.boolean.opBoolean","MERGE",FACE,{"derivedFrom":[makeQuery(id+"F1.opExtrude","SWEPT_FACE",FACE,{"disambiguationData":[OSD([sQuery(id+"F0.wireOp",EDGE,"E5")])]}),makeQuery(id+"F1.opExtrude","SWEPT_FACE",FACE,{"disambiguationData":[OSD([sQuery(id+"F0.wireOp",EDGE,"E6")])]}),makeQuery(id+"F3.opExtrude","SWEPT_FACE",FACE,{"disambiguationData":[OSD([sQuery(id+"F2.wireOp",EDGE,"E11.bottom")])]}),makeQuery(id+"F3.opExtrude","SWEPT_FACE",FACE,{"disambiguationData":[OSD([sQuery(id+"F2.wireOp",EDGE,"E12.bottom")])]})]}),makeQuery(id+"F7.opExtrude","SWEPT_FACE",FACE,{"disambiguationData":[OSD([sQuery(id+"F6.wireOp",EDGE,"E26.MirrorCS")])]})]});
            var Q3;
            Q3=makeQuery(id+"F7.boolean.opBoolean","INTERSECT",EDGE,{"derivedFrom":[makeQuery(id+"F3.boolean.opBoolean","MERGE",FACE,{"derivedFrom":[makeQuery(id+"F1.opExtrude","SWEPT_FACE",FACE,{"disambiguationData":[OSD([sQuery(id+"F0.wireOp",EDGE,"E5")])]}),makeQuery(id+"F1.opExtrude","SWEPT_FACE",FACE,{"disambiguationData":[OSD([sQuery(id+"F0.wireOp",EDGE,"E6")])]}),makeQuery(id+"F3.opExtrude","SWEPT_FACE",FACE,{"disambiguationData":[OSD([sQuery(id+"F2.wireOp",EDGE,"E11.bottom")])]}),makeQuery(id+"F3.opExtrude","SWEPT_FACE",FACE,{"disambiguationData":[OSD([sQuery(id+"F2.wireOp",EDGE,"E12.bottom")])]})]}),makeQuery(id+"F7.opExtrude","SWEPT_FACE",FACE,{"disambiguationData":[OSD([sQuery(id+"F6.wireOp",EDGE,"E28.MirrorCS")])]})]});
            var Q4;
            Q4=makeQuery(id+"F7.boolean.opBoolean","INTERSECT",EDGE,{"derivedFrom":[makeQuery(id+"F3.boolean.opBoolean","MERGE",FACE,{"derivedFrom":[makeQuery(id+"F1.opExtrude","SWEPT_FACE",FACE,{"disambiguationData":[OSD([sQuery(id+"F0.wireOp",EDGE,"E5")])]}),makeQuery(id+"F1.opExtrude","SWEPT_FACE",FACE,{"disambiguationData":[OSD([sQuery(id+"F0.wireOp",EDGE,"E6")])]}),makeQuery(id+"F3.opExtrude","SWEPT_FACE",FACE,{"disambiguationData":[OSD([sQuery(id+"F2.wireOp",EDGE,"E11.bottom")])]}),makeQuery(id+"F3.opExtrude","SWEPT_FACE",FACE,{"disambiguationData":[OSD([sQuery(id+"F2.wireOp",EDGE,"E12.bottom")])]})]}),makeQuery(id+"F7.opExtrude","SWEPT_FACE",FACE,{"disambiguationData":[OSD([sQuery(id+"F6.wireOp",EDGE,"E18.MirrorCS")])]})]});
            var Q5;
            Q5=makeQuery(id+"F7.boolean.opBoolean","INTERSECT",EDGE,{"derivedFrom":[makeQuery(id+"F3.boolean.opBoolean","MERGE",FACE,{"derivedFrom":[makeQuery(id+"F1.opExtrude","SWEPT_FACE",FACE,{"disambiguationData":[OSD([sQuery(id+"F0.wireOp",EDGE,"E5")])]}),makeQuery(id+"F1.opExtrude","SWEPT_FACE",FACE,{"disambiguationData":[OSD([sQuery(id+"F0.wireOp",EDGE,"E6")])]}),makeQuery(id+"F3.opExtrude","SWEPT_FACE",FACE,{"disambiguationData":[OSD([sQuery(id+"F2.wireOp",EDGE,"E11.bottom")])]}),makeQuery(id+"F3.opExtrude","SWEPT_FACE",FACE,{"disambiguationData":[OSD([sQuery(id+"F2.wireOp",EDGE,"E12.bottom")])]})]}),makeQuery(id+"F7.opExtrude","SWEPT_FACE",FACE,{"disambiguationData":[OSD([sQuery(id+"F6.wireOp",EDGE,"E20.MirrorCS")])]})]});
            var Q6;
            Q6=makeQuery(id+"F7.boolean.opBoolean","INTERSECT",EDGE,{"derivedFrom":[makeQuery(id+"F3.boolean.opBoolean","MERGE",FACE,{"derivedFrom":[makeQuery(id+"F1.opExtrude","SWEPT_FACE",FACE,{"disambiguationData":[OSD([sQuery(id+"F0.wireOp",EDGE,"E5")])]}),makeQuery(id+"F1.opExtrude","SWEPT_FACE",FACE,{"disambiguationData":[OSD([sQuery(id+"F0.wireOp",EDGE,"E6")])]}),makeQuery(id+"F3.opExtrude","SWEPT_FACE",FACE,{"disambiguationData":[OSD([sQuery(id+"F2.wireOp",EDGE,"E11.bottom")])]}),makeQuery(id+"F3.opExtrude","SWEPT_FACE",FACE,{"disambiguationData":[OSD([sQuery(id+"F2.wireOp",EDGE,"E12.bottom")])]})]}),makeQuery(id+"F7.opExtrude","SWEPT_FACE",FACE,{"disambiguationData":[OSD([sQuery(id+"F6.wireOp",EDGE,"E13.bottom")])]})]});
            var Q7;
            Q7=makeQuery(id+"F7.boolean.opBoolean","INTERSECT",EDGE,{"derivedFrom":[makeQuery(id+"F3.boolean.opBoolean","MERGE",FACE,{"derivedFrom":[makeQuery(id+"F1.opExtrude","SWEPT_FACE",FACE,{"disambiguationData":[OSD([sQuery(id+"F0.wireOp",EDGE,"E5")])]}),makeQuery(id+"F1.opExtrude","SWEPT_FACE",FACE,{"disambiguationData":[OSD([sQuery(id+"F0.wireOp",EDGE,"E6")])]}),makeQuery(id+"F3.opExtrude","SWEPT_FACE",FACE,{"disambiguationData":[OSD([sQuery(id+"F2.wireOp",EDGE,"E11.bottom")])]}),makeQuery(id+"F3.opExtrude","SWEPT_FACE",FACE,{"disambiguationData":[OSD([sQuery(id+"F2.wireOp",EDGE,"E12.bottom")])]})]}),makeQuery(id+"F7.opExtrude","SWEPT_FACE",FACE,{"disambiguationData":[OSD([sQuery(id+"F6.wireOp",EDGE,"E13.left")])]})]});
            fillet(context, id + "F20", {"entities" : qUnion([Q0, Q1, Q2, Q3, Q4, Q5, Q6, Q7]), "radius" : 5 * mm, "tangentPropagation" : true, "allowEdgeOverflow" : false});
        }
        {
            var Q0;
            Q0=makeQuery(id+"F15.boolean.opBoolean","MERGE",FACE,{"derivedFrom":[makeQuery(id+"F9.opExtrude","CAP_FACE",FACE,{"disambiguationData":[OSD([sQuery(id+"F8.wireOp",EDGE,"E43.bottom"),sQuery(id+"F8.wireOp",EDGE,"E43.top"),sQuery(id+"F8.wireOp",EDGE,"E43.left"),sQuery(id+"F8.wireOp",EDGE,"E43.right"),sQuery(id+"F8.wireOp",EDGE,"E44.filletArc"),sQuery(id+"F8.wireOp",EDGE,"E45.filletArc")])],"isStart":true}),makeQuery(id+"F14.boolean.opBoolean","MERGE",FACE,{"derivedFrom":[makeQuery(id+"F9.opExtrude","CAP_FACE",FACE,{"disambiguationData":[OSD([sQuery(id+"F8.wireOp",EDGE,"E47.MirrorCS"),sQuery(id+"F8.wireOp",EDGE,"E48.MirrorCS"),sQuery(id+"F8.wireOp",EDGE,"E50.MirrorCS"),sQuery(id+"F8.wireOp",EDGE,"E51.MirrorCS"),sQuery(id+"F8.wireOp",EDGE,"E53.MirrorCS"),sQuery(id+"F8.wireOp",EDGE,"E54.MirrorCS")])],"isStart":true}),makeQuery(id+"F1.opExtrude","SWEPT_FACE",FACE,{"disambiguationData":[OSD([sQuery(id+"F0.wireOp",EDGE,"E3.MirrorCS")])]})]})]});
            var sketch = newSketch(context, id + "F21", { "sketchPlane" : qUnion([Q0])});
            skLineSegment(sketch, "E183", {"start": v(0, 0) * mm, "end": v(0, 58) * mm, "construction": true});
            skCircle(sketch, "E184", {"center": v(0, 29) * mm, "radius": 20 * mm});
            skCircle(sketch, "E185.1.0.0", {"center": v(67, 29) * mm, "radius": 20 * mm});
            skCircle(sketch, "E185.2.0.0", {"center": v(134, 29) * mm, "radius": 20 * mm});
            skCircle(sketch, "E185.3.0.0", {"center": v(201, 29) * mm, "radius": 20 * mm});
            skCircle(sketch, "E185.4.0.0", {"center": v(268, 29) * mm, "radius": 20 * mm});
            skLineSegment(sketch, "E185.direction1", {"start": v(0, 29) * mm, "end": v(67, 29) * mm, "construction": true});
            skCircle(sketch, "E186.MirrorC", {"center": v(-201, 29) * mm, "radius": 20 * mm});
            skCircle(sketch, "E187.MirrorC", {"center": v(-134, 29) * mm, "radius": 20 * mm});
            skCircle(sketch, "E188.MirrorC", {"center": v(-67, 29) * mm, "radius": 20 * mm});
            skCircle(sketch, "E189.MirrorC", {"center": v(-268, 29) * mm, "radius": 20 * mm});
            skLineSegment(sketch, "E190.MirrorCS", {"start": v(0, 29) * mm, "end": v(-67, 29) * mm, "construction": true});
            skSolve(sketch);
        }
        {
            var Q0;
            Q0 = qSketchRegion(id + "F21", true);
            extrude(context, id + "F22", {"entities" : qUnion([Q0]), "operationType" : NewBodyOperationType.REMOVE, "endBound" : BoundingType.THROUGH_ALL, "oppositeDirection" : true, "depth" : 25 * mm});
        }
    });
